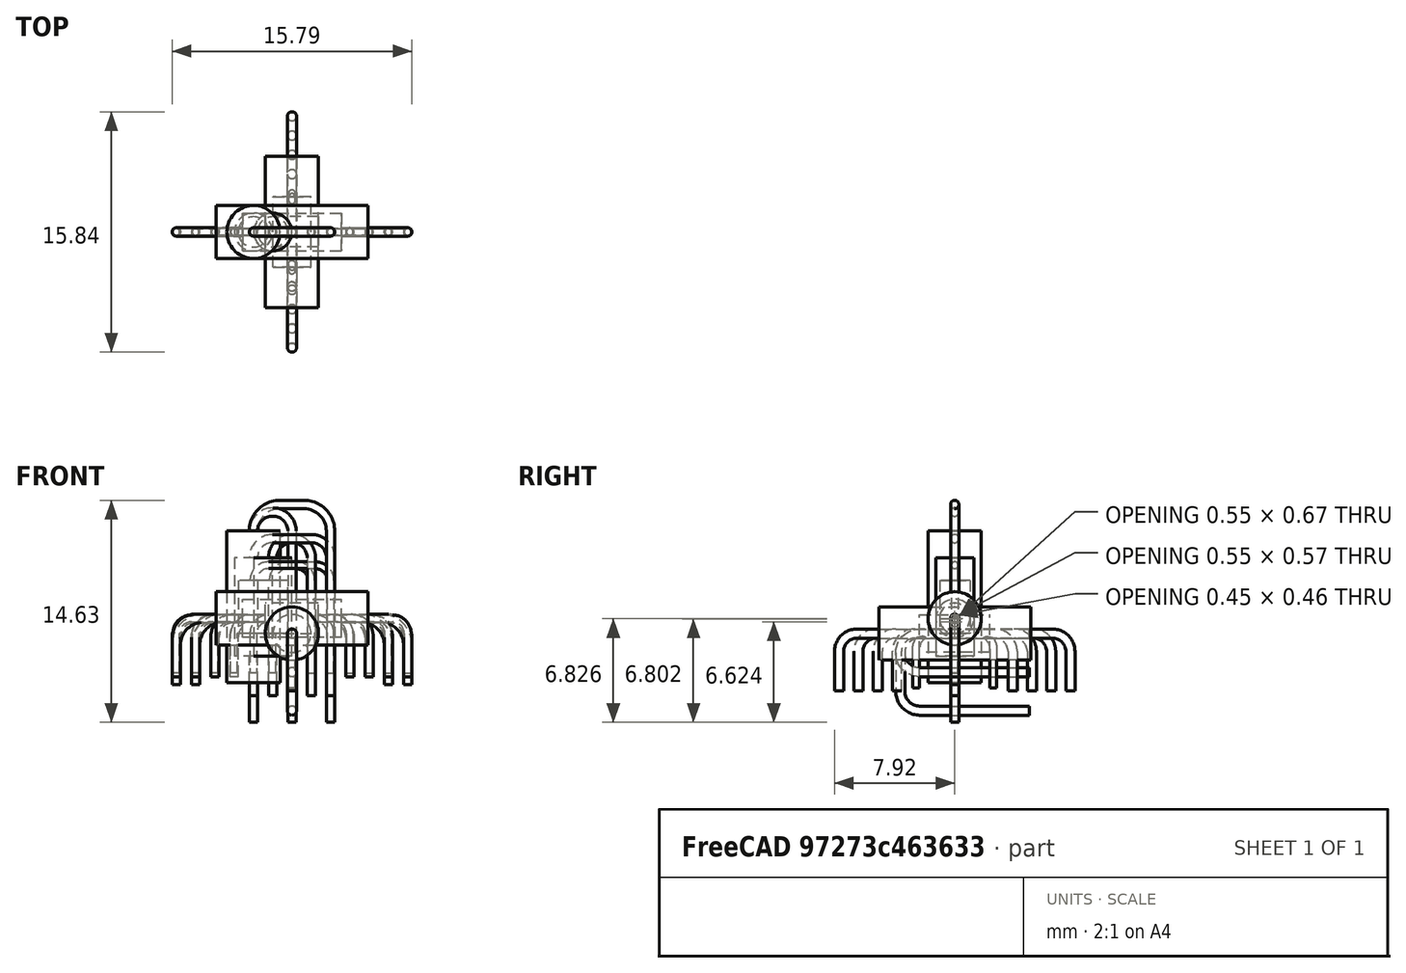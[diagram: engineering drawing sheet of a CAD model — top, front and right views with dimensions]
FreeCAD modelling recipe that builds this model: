
FCSTD DOCUMENT  (FreeCAD 0.19R17069 (Git))
Label: Generic Resistors
License: All rights reserved
LicenseURL: http://en.wikipedia.org/wiki/All_rights_reserved
objects: Sketcher::SketchObject×143, PartDesign::Body×94, PartDesign::AdditivePipe×49, PartDesign::Pad×45, Part::MultiFuse×43, App::DocumentObjectGroup×9, PartDesign::FeatureBase×1
note: 469 computed .brp shape members not serialized (recipe doc carries the construction recipe); baked Part::Feature solids carry a one-line shape summary decoded from their .brp

FEATURE [Sketcher::SketchObject] Sketch
  AttachmentOffset = pos=(0,0,0) rot=(0,0,1;-1.5708rad)
  MapMode = 5
  Placement = pos=(0,0,0) rot=(-0.57735,-0.57735,0.57735;4.18879rad)
  Support = -> [XZ_Plane]
  expr: Constraints[1] = 1.25
  sketch-geometry (1):
    g0: Circle CenterX=0 CenterY=0 CenterZ=0 NormalX=0 NormalY=0 NormalZ=1 AngleXU=0 Radius=1.25
  constraints (2):
    c: Coincident(g0,g-1)
    c: Radius(g0) = 1.25
FEATURE [PartDesign::Pad] Pad
  Length = 4.63
  Length2 = 100
  Midplane = true
  Placement = pos=(0,0,0) rot=(1,0,0;1.5708rad)
  Profile = -> Sketch
  Type = 0
  expr: Length = (4.06 + 5.2) / 2
FEATURE [PartDesign::Body] Body  label="Body_1/4W"
  Group = -> [Sketch,Pad]
  Origin = -> Origin
  Tip = -> Pad
FEATURE [Sketcher::SketchObject] Sketch002
  MapMode = 5
  Placement = pos=(0,0,0) rot=(0.57735,0.57735,0.57735;2.0944rad)
  Support = -> [YZ_Plane002]
  expr: Constraints[11] = (2.03 + 2.72) / 2 / 2
  expr: Constraints[10] = 3 * 2.54
  sketch-geometry (5):
    g0: LineSegment StartX=-2.6225 StartY=0 StartZ=0 EndX=2.6225 EndY=0 EndZ=0
    g1: LineSegment StartX=-3.81 StartY=-1.1875 StartZ=0 EndX=-3.81 EndY=-3.7875 EndZ=0
    g2: LineSegment StartX=3.81 StartY=-1.1875 StartZ=0 EndX=3.81 EndY=-3.7875 EndZ=0
    g3: ArcOfCircle CenterX=-2.6225 CenterY=-1.1875 CenterZ=0 NormalX=0 NormalY=0 NormalZ=1 AngleXU=0 Radius=1.1875 StartAngle=1.5708 EndAngle=3.14159
    g4: ArcOfCircle CenterX=2.6225 CenterY=-1.1875 CenterZ=0 NormalX=0 NormalY=0 NormalZ=1 AngleXU=0 Radius=1.1875 StartAngle=0 EndAngle=1.5708
  constraints (13):
    c: Vertical(g1)
    c: Vertical(g2)
    c: Equal(g2,g1)
    c: Tangent(g0,g3) = 1.5708
    c: Tangent(g1,g3) = -1.5708
    c: Tangent(g0,g4) = 1.5708
    c: Tangent(g2,g4) = 1.5708
    c: Symmetric(g0,g0,g-2)
    c: Equal(g4,g3)
    c: PointOnObject(g0,g-1)
    c: DistanceX(g1,g2) = 7.62
    c: DistanceY(g1,g0) = 1.1875
    c: DistanceY(g1,g1) = 2.6
FEATURE [Sketcher::SketchObject] Sketch003
  AttachmentOffset = pos=(0,0,0) rot=(0,0,1;-1.5708rad)
  MapMode = 5
  Placement = pos=(0,0,0) rot=(-0.57735,-0.57735,0.57735;4.18879rad)
  Support = -> [XZ_Plane002]
  expr: Constraints[1] = 0.3
  sketch-geometry (1):
    g0: Circle CenterX=0 CenterY=0 CenterZ=0 NormalX=0 NormalY=0 NormalZ=1 AngleXU=0 Radius=0.3
  constraints (2):
    c: Coincident(g0,g-1)
    c: Radius(g0) = 0.3
FEATURE [PartDesign::AdditivePipe] AdditivePipe
  AuxilleryCurvelinear = true
  AuxillerySpineTangent = false
  Binormal = (0,0,0)
  Mode = 0
  Placement = pos=(0,0,0) rot=(1,0,0;1.5708rad)
  Profile = -> Sketch003
  Refine = true
  Spine = -> Sketch002
  SpineTangent = false
  Transformation = 0
  Transition = 0
FEATURE [PartDesign::Body] Body002  label="Leads_P7.62"
  Group = -> [Sketch002,Sketch003,AdditivePipe]
  Origin = -> Origin002
  Tip = -> AdditivePipe
FEATURE [Sketcher::SketchObject] Sketch004
  MapMode = 5
  Placement = pos=(0,0,0) rot=(0.57735,0.57735,0.57735;2.0944rad)
  Support = -> [YZ_Plane003]
  expr: Constraints[11] = (2.03 + 2.72) / 2 / 2
  expr: Constraints[10] = 4 * 2.54
  sketch-geometry (5):
    g0: LineSegment StartX=-3.8925 StartY=-4.323e-13 StartZ=0 EndX=3.8925 EndY=-4.323e-13 EndZ=0
    g1: LineSegment StartX=-5.08 StartY=-1.1875 StartZ=0 EndX=-5.08 EndY=-3.7875 EndZ=0
    g2: LineSegment StartX=5.08 StartY=-1.1875 StartZ=0 EndX=5.08 EndY=-3.7875 EndZ=0
    g3: ArcOfCircle CenterX=-3.8925 CenterY=-1.1875 CenterZ=0 NormalX=0 NormalY=0 NormalZ=1 AngleXU=0 Radius=1.1875 StartAngle=1.5708 EndAngle=3.14159
    g4: ArcOfCircle CenterX=3.8925 CenterY=-1.1875 CenterZ=0 NormalX=0 NormalY=0 NormalZ=1 AngleXU=0 Radius=1.1875 StartAngle=-3.3777e-12 EndAngle=1.5708
  constraints (13):
    c: Vertical(g1)
    c: Vertical(g2)
    c: Equal(g2,g1)
    c: Tangent(g0,g3) = 1.5708
    c: Tangent(g1,g3) = -1.5708
    c: Tangent(g0,g4) = 1.5708
    c: Tangent(g2,g4) = 1.5708
    c: Symmetric(g0,g0,g-2)
    c: Equal(g4,g3)
    c: PointOnObject(g0,g-1)
    c: DistanceX(g1,g2) = 10.16
    c: DistanceY(g1,g0) = 1.1875
    c: DistanceY(g1,g1) = 2.6
FEATURE [Sketcher::SketchObject] Sketch005
  AttachmentOffset = pos=(0,0,0) rot=(0,0,1;-1.5708rad)
  MapMode = 5
  Placement = pos=(0,0,0) rot=(-0.57735,-0.57735,0.57735;4.18879rad)
  Support = -> [XZ_Plane003]
  expr: Constraints[1] = 0.3
  sketch-geometry (1):
    g0: Circle CenterX=0 CenterY=0 CenterZ=0 NormalX=0 NormalY=0 NormalZ=1 AngleXU=0 Radius=0.3
  constraints (2):
    c: Coincident(g0,g-1)
    c: Radius(g0) = 0.3
FEATURE [PartDesign::AdditivePipe] AdditivePipe001
  AuxilleryCurvelinear = true
  AuxillerySpineTangent = false
  Binormal = (0,0,0)
  Mode = 0
  Placement = pos=(0,0,0) rot=(1,0,0;1.5708rad)
  Profile = -> Sketch005
  Refine = true
  Spine = -> Sketch004
  SpineTangent = false
  Transformation = 0
  Transition = 0
FEATURE [PartDesign::Body] Body003  label="Leads_P10.16"
  Group = -> [Sketch004,Sketch005,AdditivePipe001]
  Origin = -> Origin003
  Tip = -> AdditivePipe001
FEATURE [Sketcher::SketchObject] Sketch006
  MapMode = 5
  Placement = pos=(0,0,0) rot=(0.57735,0.57735,0.57735;2.0944rad)
  Support = -> [YZ_Plane004]
  expr: Constraints[15] = (4.06 + 5.2) / 2 / 2
  expr: Constraints[7] = (4.06 + 5.2) / 2 / 2
  expr: Constraints[3] = 2.54 / 2
  sketch-geometry (7):
    g0: LineSegment StartX=4.915 StartY=0 StartZ=0 EndX=-2.315 EndY=0 EndZ=0
    g1: ArcOfCircle CenterX=-2.315 CenterY=-1.27 CenterZ=0 NormalX=0 NormalY=0 NormalZ=1 AngleXU=0 Radius=1.27 StartAngle=1.5708 EndAngle=4.71239
    g2: LineSegment StartX=-2.315 StartY=-2.54 StartZ=0 EndX=4.915 EndY=-2.54 EndZ=0
    g3: GeomPoint X=2.315 Y=0 Z=0
    g4: GeomPoint X=2.315 Y=-2.54 Z=0
    g5: GeomPoint X=-3.585 Y=-1.27 Z=0
    g6: GeomPoint X=-2.315 Y=0 Z=0
  constraints (17):
    c: PointOnObject(g0,g-1)
    c: PointOnObject(g0,g-1)
    c: Horizontal(g2)
    c: Radius(g1) = 1.27
    c: Tangent(g1,g0) = -1.5708
    c: Tangent(g2,g1) = -1.5708
    c: PointOnObject(g3,g0)
    c: DistanceX(g-1,g3) = 2.315
    c: DistanceX(g3,g0) = 2.6
    c: PointOnObject(g4,g2)
    c: DistanceX(g4,g2) = 2.6
    c: Vertical(g0,g2)
    c: PointOnObject(g5,g1)
    c: Horizontal(g1,g5)
    c: PointOnObject(g6,g0)
    c: DistanceX(g6,g-1) = 2.315
    c: DistanceX(g0,g6) = 0
FEATURE [Sketcher::SketchObject] Sketch007
  AttachmentOffset = pos=(0,0,0) rot=(0,0,1;-1.5708rad)
  MapMode = 5
  Placement = pos=(0,0,0) rot=(-0.57735,-0.57735,0.57735;4.18879rad)
  Support = -> [XZ_Plane004]
  expr: Constraints[1] = 0.3
  sketch-geometry (1):
    g0: Circle CenterX=0 CenterY=0 CenterZ=0 NormalX=0 NormalY=0 NormalZ=1 AngleXU=0 Radius=0.3
  constraints (2):
    c: Coincident(g0,g-1)
    c: Radius(g0) = 0.3
FEATURE [PartDesign::AdditivePipe] AdditivePipe002
  AuxilleryCurvelinear = true
  AuxillerySpineTangent = false
  Binormal = (0,0,0)
  Mode = 0
  Placement = pos=(0,0,0) rot=(1,0,0;1.5708rad)
  Profile = -> Sketch007
  Refine = true
  Spine = -> Sketch006
  SpineTangent = false
  Transformation = 0
  Transition = 0
FEATURE [PartDesign::Body] Body004  label="Leads_Vertical_P2.54"
  Group = -> [Sketch006,Sketch007,AdditivePipe002]
  Origin = -> Origin004
  Tip = -> AdditivePipe002
FEATURE [Sketcher::SketchObject] Sketch008
  MapMode = 5
  Placement = pos=(0,0,0) rot=(0.57735,0.57735,0.57735;2.0944rad)
  Support = -> [YZ_Plane005]
  expr: Constraints[18] = 1.27
  expr: Constraints[9] = (4.06 + 5.2) / 2 / 2
  expr: Constraints[3] = (4.06 + 5.2) / 2 / 2
  sketch-geometry (8):
    g0: LineSegment StartX=4.915 StartY=0 StartZ=0 EndX=-2.315 EndY=0 EndZ=0
    g1: LineSegment StartX=-2.315 StartY=-5.08 StartZ=0 EndX=4.915 EndY=-5.08 EndZ=0
    g2: GeomPoint X=2.315 Y=0 Z=0
    g3: GeomPoint X=2.315 Y=-5.08 Z=0
    g4: GeomPoint X=-2.315 Y=0 Z=0
    g5: LineSegment StartX=-3.585 StartY=-1.27 StartZ=0 EndX=-3.585 EndY=-3.81 EndZ=0
    g6: ArcOfCircle CenterX=-2.315 CenterY=-1.27 CenterZ=0 NormalX=0 NormalY=0 NormalZ=1 AngleXU=0 Radius=1.27 StartAngle=1.5708 EndAngle=3.14159
    g7: ArcOfCircle CenterX=-2.315 CenterY=-3.81 CenterZ=0 NormalX=0 NormalY=0 NormalZ=1 AngleXU=0 Radius=1.27 StartAngle=3.14159 EndAngle=4.71239
  constraints (20):
    c: PointOnObject(g0,g-1)
    c: Horizontal(g1)
    c: PointOnObject(g2,g0)
    c: DistanceX(g-1,g2) = 2.315
    c: DistanceX(g2,g0) = 2.6
    c: PointOnObject(g3,g1)
    c: DistanceX(g3,g1) = 2.6
    c: Vertical(g0,g1)
    c: PointOnObject(g4,g0)
    c: DistanceX(g4,g-1) = 2.315
    c: Vertical(g5)
    c: Tangent(g0,g6) = -1.5708
    c: Tangent(g5,g6) = -1.5708
    c: Tangent(g1,g7) = -1.5708
    c: Tangent(g5,g7) = -1.5708
    c: DistanceY(g1,g0) = 5.08
    c: PointOnObject(g0,g-1)
    c: Equal(g7,g6)
    c: Radius(g6) = 1.27
    c: DistanceX(g0,g4) = 0
FEATURE [Sketcher::SketchObject] Sketch009
  AttachmentOffset = pos=(0,0,0) rot=(0,0,1;-1.5708rad)
  MapMode = 5
  Placement = pos=(0,0,0) rot=(-0.57735,-0.57735,0.57735;4.18879rad)
  Support = -> [XZ_Plane005]
  expr: Constraints[1] = 0.3
  sketch-geometry (1):
    g0: Circle CenterX=0 CenterY=0 CenterZ=0 NormalX=0 NormalY=0 NormalZ=1 AngleXU=0 Radius=0.3
  constraints (2):
    c: Coincident(g0,g-1)
    c: Radius(g0) = 0.3
FEATURE [PartDesign::AdditivePipe] AdditivePipe003
  AuxilleryCurvelinear = true
  AuxillerySpineTangent = false
  Binormal = (0,0,0)
  Mode = 0
  Placement = pos=(0,0,0) rot=(1,0,0;1.5708rad)
  Profile = -> Sketch009
  Refine = true
  Spine = -> Sketch008
  SpineTangent = false
  Transformation = 0
  Transition = 0
FEATURE [PartDesign::Body] Body005  label="Leads_Vertical_P5.08"
  Group = -> [Sketch008,Sketch009,AdditivePipe003]
  Origin = -> Origin005
  Tip = -> AdditivePipe003
FEATURE [Sketcher::SketchObject] Sketch010
  AttachmentOffset = pos=(0,0,0) rot=(0,0,1;-1.5708rad)
  MapMode = 5
  Placement = pos=(0,0,0) rot=(-0.57735,-0.57735,0.57735;4.18879rad)
  Support = -> [XZ_Plane006]
  expr: Constraints[1] = 2 / 2
  sketch-geometry (1):
    g0: Circle CenterX=0 CenterY=0 CenterZ=0 NormalX=0 NormalY=0 NormalZ=1 AngleXU=0 Radius=1
  constraints (2):
    c: Coincident(g0,g-1)
    c: Radius(g0) = 1
FEATURE [PartDesign::Pad] Pad001
  Length = 3.5
  Length2 = 100
  Midplane = true
  Placement = pos=(0,0,0) rot=(1,0,0;1.5708rad)
  Profile = -> Sketch010
  Type = 0
  expr: Length = 3.5
FEATURE [PartDesign::Body] Body006  label="1/8W_Body"
  Group = -> [Sketch010,Pad001]
  Origin = -> Origin006
  Tip = -> Pad001
FEATURE [Sketcher::SketchObject] Sketch011
  AttachmentOffset = pos=(0,0,0) rot=(0,0,1;-1.5708rad)
  MapMode = 5
  Placement = pos=(0,0,0) rot=(-0.57735,-0.57735,0.57735;4.18879rad)
  Support = -> [XZ_Plane007]
  expr: Constraints[1] = 1.75
  sketch-geometry (1):
    g0: Circle CenterX=0 CenterY=0 CenterZ=0 NormalX=0 NormalY=0 NormalZ=1 AngleXU=0 Radius=1.75
  constraints (2):
    c: Coincident(g0,g-1)
    c: Radius(g0) = 1.75
FEATURE [PartDesign::Pad] Pad002
  Length = 10
  Length2 = 100
  Midplane = true
  Placement = pos=(0,0,0) rot=(1,0,0;1.5708rad)
  Profile = -> Sketch011
  Type = 0
  expr: Length = 10
FEATURE [PartDesign::Body] Body007  label="Body_1/2W"
  Group = -> [Sketch011,Pad002]
  Origin = -> Origin007
  Tip = -> Pad002
FEATURE [Sketcher::SketchObject] Sketch012
  MapMode = 5
  Placement = pos=(0,0,0) rot=(0.57735,0.57735,0.57735;2.0944rad)
  Support = -> [YZ_Plane008]
  expr: Constraints[11] = (2.03 + 2.72) / 2 / 2
  expr: Constraints[10] = 12.7
  sketch-geometry (5):
    g0: LineSegment StartX=-5.1625 StartY=-4.323e-13 StartZ=0 EndX=5.1625 EndY=-4.323e-13 EndZ=0
    g1: LineSegment StartX=-6.35 StartY=-1.1875 StartZ=0 EndX=-6.35 EndY=-3.7875 EndZ=0
    g2: LineSegment StartX=6.35 StartY=-1.1875 StartZ=0 EndX=6.35 EndY=-3.7875 EndZ=0
    g3: ArcOfCircle CenterX=-5.1625 CenterY=-1.1875 CenterZ=0 NormalX=0 NormalY=0 NormalZ=1 AngleXU=0 Radius=1.1875 StartAngle=1.5708 EndAngle=3.14159
    g4: ArcOfCircle CenterX=5.1625 CenterY=-1.1875 CenterZ=0 NormalX=0 NormalY=0 NormalZ=1 AngleXU=0 Radius=1.1875 StartAngle=-3.3777e-12 EndAngle=1.5708
  constraints (13):
    c: Vertical(g1)
    c: Vertical(g2)
    c: Equal(g2,g1)
    c: Tangent(g0,g3) = 1.5708
    c: Tangent(g1,g3) = -1.5708
    c: Tangent(g0,g4) = 1.5708
    c: Tangent(g2,g4) = 1.5708
    c: Symmetric(g0,g0,g-2)
    c: Equal(g4,g3)
    c: PointOnObject(g0,g-1)
    c: DistanceX(g1,g2) = 12.7
    c: DistanceY(g1,g0) = 1.1875
    c: DistanceY(g1,g1) = 2.6
FEATURE [Sketcher::SketchObject] Sketch013
  AttachmentOffset = pos=(0,0,0) rot=(0,0,1;-1.5708rad)
  MapMode = 5
  Placement = pos=(0,0,0) rot=(-0.57735,-0.57735,0.57735;4.18879rad)
  Support = -> [XZ_Plane008]
  expr: Constraints[1] = 0.3
  sketch-geometry (1):
    g0: Circle CenterX=0 CenterY=0 CenterZ=0 NormalX=0 NormalY=0 NormalZ=1 AngleXU=0 Radius=0.3
  constraints (2):
    c: Coincident(g0,g-1)
    c: Radius(g0) = 0.3
FEATURE [PartDesign::AdditivePipe] AdditivePipe004
  AuxilleryCurvelinear = true
  AuxillerySpineTangent = false
  Binormal = (0,0,0)
  Mode = 0
  Placement = pos=(0,0,0) rot=(1,0,0;1.5708rad)
  Profile = -> Sketch013
  Refine = true
  Spine = -> Sketch012
  SpineTangent = false
  Transformation = 0
  Transition = 0
FEATURE [PartDesign::Body] Body008  label="Leads_P12.7"
  Group = -> [Sketch012,Sketch013,AdditivePipe004]
  Origin = -> Origin008
  Tip = -> AdditivePipe004
FEATURE [Sketcher::SketchObject] Sketch014
  AttachmentOffset = pos=(0,0,0) rot=(0,0,1;-1.5708rad)
  MapMode = 5
  Placement = pos=(0,0,0) rot=(-0.57735,-0.57735,0.57735;4.18879rad)
  Support = -> [XZ_Plane009]
  expr: Constraints[1] = 0.3
  sketch-geometry (1):
    g0: Circle CenterX=0 CenterY=0 CenterZ=0 NormalX=0 NormalY=0 NormalZ=1 AngleXU=0 Radius=0.3
  constraints (2):
    c: Coincident(g0,g-1)
    c: Radius(g0) = 0.3
FEATURE [Sketcher::SketchObject] Sketch015
  MapMode = 5
  Placement = pos=(0,0,0) rot=(0.57735,0.57735,0.57735;2.0944rad)
  Support = -> [YZ_Plane009]
  expr: Constraints[11] = (2.03 + 2.72) / 2 / 2
  expr: Constraints[10] = 15.24
  sketch-geometry (5):
    g0: LineSegment StartX=-6.4325 StartY=-4.323e-13 StartZ=0 EndX=6.4325 EndY=-4.323e-13 EndZ=0
    g1: LineSegment StartX=-7.62 StartY=-1.1875 StartZ=0 EndX=-7.62 EndY=-3.7875 EndZ=0
    g2: LineSegment StartX=7.62 StartY=-1.1875 StartZ=0 EndX=7.62 EndY=-3.7875 EndZ=0
    g3: ArcOfCircle CenterX=-6.4325 CenterY=-1.1875 CenterZ=0 NormalX=0 NormalY=0 NormalZ=1 AngleXU=0 Radius=1.1875 StartAngle=1.5708 EndAngle=3.14159
    g4: ArcOfCircle CenterX=6.4325 CenterY=-1.1875 CenterZ=0 NormalX=0 NormalY=0 NormalZ=1 AngleXU=0 Radius=1.1875 StartAngle=-3.3777e-12 EndAngle=1.5708
  constraints (13):
    c: Vertical(g1)
    c: Vertical(g2)
    c: Equal(g2,g1)
    c: Tangent(g0,g3) = 1.5708
    c: Tangent(g1,g3) = -1.5708
    c: Tangent(g0,g4) = 1.5708
    c: Tangent(g2,g4) = 1.5708
    c: Symmetric(g0,g0,g-2)
    c: Equal(g4,g3)
    c: PointOnObject(g0,g-1)
    c: DistanceX(g1,g2) = 15.24
    c: DistanceY(g1,g0) = 1.1875
    c: DistanceY(g1,g1) = 2.6
FEATURE [Sketcher::SketchObject] Sketch018
  MapMode = 5
  Placement = pos=(0,0,0) rot=(0.57735,0.57735,0.57735;2.0944rad)
  Support = -> [YZ_Plane012]
  expr: Constraints[11] = 2 / 2
  expr: Constraints[10] = 4 * 2.54
  sketch-geometry (5):
    g0: LineSegment StartX=-4.08 StartY=0 StartZ=0 EndX=4.08 EndY=0 EndZ=0
    g1: LineSegment StartX=-5.08 StartY=-1 StartZ=0 EndX=-5.08 EndY=-3.6 EndZ=0
    g2: LineSegment StartX=5.08 StartY=-1 StartZ=0 EndX=5.08 EndY=-3.6 EndZ=0
    g3: ArcOfCircle CenterX=-4.08 CenterY=-1 CenterZ=0 NormalX=0 NormalY=0 NormalZ=1 AngleXU=0 Radius=1 StartAngle=1.5708 EndAngle=3.14159
    g4: ArcOfCircle CenterX=4.08 CenterY=-1 CenterZ=0 NormalX=0 NormalY=0 NormalZ=1 AngleXU=0 Radius=1 StartAngle=0 EndAngle=1.5708
  constraints (13):
    c: Vertical(g1)
    c: Vertical(g2)
    c: Equal(g2,g1)
    c: Tangent(g0,g3) = 1.5708
    c: Tangent(g1,g3) = -1.5708
    c: Tangent(g0,g4) = 1.5708
    c: Tangent(g2,g4) = 1.5708
    c: Symmetric(g0,g0,g-2)
    c: Equal(g4,g3)
    c: PointOnObject(g0,g-1)
    c: DistanceX(g1,g2) = 10.16
    c: DistanceY(g1,g0) = 1
    c: DistanceY(g1,g1) = 2.6
FEATURE [Sketcher::SketchObject] Sketch019
  AttachmentOffset = pos=(0,0,0) rot=(0,0,1;-1.5708rad)
  MapMode = 5
  Placement = pos=(0,0,0) rot=(-0.57735,-0.57735,0.57735;4.18879rad)
  Support = -> [XZ_Plane010]
  expr: Constraints[1] = 0.45 / 2
  sketch-geometry (1):
    g0: Circle CenterX=0 CenterY=0 CenterZ=0 NormalX=0 NormalY=0 NormalZ=1 AngleXU=0 Radius=0.225
  constraints (2):
    c: Coincident(g0,g-1)
    c: Radius(g0) = 0.225
FEATURE [PartDesign::AdditivePipe] AdditivePipe011
  AuxilleryCurvelinear = true
  AuxillerySpineTangent = false
  Binormal = (0,0,0)
  Mode = 0
  Placement = pos=(0,0,0) rot=(1,0,0;1.5708rad)
  Profile = -> Sketch019
  Refine = true
  Spine = -> Sketch018
  SpineTangent = false
  Transformation = 0
  Transition = 0
FEATURE [PartDesign::Body] Body012  label="1/8W_10.16_H"
  Group = -> [Sketch018,Sketch019,AdditivePipe011]
  Origin = -> Origin011
  Tip = -> AdditivePipe011
FEATURE [Sketcher::SketchObject] Sketch020
  MapMode = 5
  Placement = pos=(0,0,0) rot=(0.57735,0.57735,0.57735;2.0944rad)
  Support = -> [YZ_Plane011]
  expr: Constraints[24] = 2.54
  expr: Constraints[15] = 2 / 2
  expr: Constraints[10] = 3.5 / 2
  expr: Constraints[4] = 3.5 / 2
  sketch-geometry (9):
    g0: LineSegment StartX=4.35 StartY=0 StartZ=0 EndX=-1.75 EndY=1e-16 EndZ=0
    g1: LineSegment StartX=-1.75 StartY=-2.54 StartZ=0 EndX=4.35 EndY=-2.54 EndZ=0
    g2: GeomPoint X=1.75 Y=0 Z=0
    g3: GeomPoint X=1.75 Y=-2.54 Z=0
    g4: GeomPoint X=-2.75 Y=-1 Z=0
    g5: GeomPoint X=-1.75 Y=0 Z=0
    g6: ArcOfCircle CenterX=-1.75 CenterY=-1 CenterZ=0 NormalX=0 NormalY=0 NormalZ=1 AngleXU=0 Radius=1 StartAngle=1.5708 EndAngle=3.14159
    g7: LineSegment StartX=-2.75 StartY=-1 StartZ=0 EndX=-2.75 EndY=-1.54 EndZ=0
    g8: ArcOfCircle CenterX=-1.75 CenterY=-1.54 CenterZ=0 NormalX=0 NormalY=0 NormalZ=1 AngleXU=0 Radius=1 StartAngle=3.14159 EndAngle=4.71239
  constraints (25):
    c: PointOnObject(g0,g-1)
    c: PointOnObject(g0,g-1)
    c: Horizontal(g1)
    c: PointOnObject(g2,g0)
    c: DistanceX(g-1,g2) = 1.75
    c: DistanceX(g2,g0) = 2.6
    c: PointOnObject(g3,g1)
    c: DistanceX(g3,g1) = 2.6
    c: Vertical(g0,g1)
    c: PointOnObject(g5,g0)
    c: DistanceX(g5,g-1) = 1.75
    c: DistanceX(g0,g5) = 0
    c: Coincident(g6,g0)
    c: Coincident(g6,g4)
    c: Horizontal(g6,g4)
    c: Radius(g6) = 1
    c: Vertical(g6,g0)
    c: Coincident(g7,g4)
    c: Vertical(g7)
    c: Coincident(g8,g7)
    c: Coincident(g8,g1)
    c: Equal(g8,g6)
    c: Horizontal(g8,g7)
    c: Vertical(g8,g1)
    c: DistanceY(g1,g0) = 2.54
FEATURE [Sketcher::SketchObject] Sketch021
  AttachmentOffset = pos=(0,0,0) rot=(0,0,1;-1.5708rad)
  MapMode = 5
  Placement = pos=(0,0,0) rot=(-0.57735,-0.57735,0.57735;4.18879rad)
  Support = -> [XZ_Plane011]
  expr: Constraints[1] = 0.45 / 2
  sketch-geometry (1):
    g0: Circle CenterX=0 CenterY=0 CenterZ=0 NormalX=0 NormalY=0 NormalZ=1 AngleXU=0 Radius=0.225
  constraints (2):
    c: Coincident(g0,g-1)
    c: Radius(g0) = 0.225
FEATURE [PartDesign::AdditivePipe] AdditivePipe008
  AuxilleryCurvelinear = true
  AuxillerySpineTangent = false
  Binormal = (0,0,0)
  Mode = 0
  Placement = pos=(0,0,0) rot=(1,0,0;1.5708rad)
  Profile = -> Sketch021
  Refine = true
  Spine = -> Sketch020
  SpineTangent = false
  Transformation = 0
  Transition = 0
FEATURE [PartDesign::Body] Body010  label="1/8W_2.54_V"
  Group = -> [Sketch020,Sketch021,AdditivePipe008]
  Origin = -> Origin012
  Tip = -> AdditivePipe008
FEATURE [Sketcher::SketchObject] Sketch022
  MapMode = 5
  Placement = pos=(0,0,0) rot=(0.57735,0.57735,0.57735;2.0944rad)
  Support = -> [YZ_Plane013]
  expr: Constraints[18] = 2 / 2
  expr: Constraints[9] = 3.5 / 2
  expr: Constraints[3] = 3.5 / 2
  sketch-geometry (8):
    g0: LineSegment StartX=4.35 StartY=0 StartZ=0 EndX=-1.75 EndY=0 EndZ=0
    g1: LineSegment StartX=-1.75 StartY=-5.08 StartZ=0 EndX=4.35 EndY=-5.08 EndZ=0
    g2: GeomPoint X=1.75 Y=0 Z=0
    g3: GeomPoint X=1.75 Y=-5.08 Z=0
    g4: GeomPoint X=-1.75 Y=0 Z=0
    g5: LineSegment StartX=-2.75 StartY=-1 StartZ=0 EndX=-2.75 EndY=-4.08 EndZ=0
    g6: ArcOfCircle CenterX=-1.75 CenterY=-1 CenterZ=0 NormalX=0 NormalY=0 NormalZ=1 AngleXU=0 Radius=1 StartAngle=1.5708 EndAngle=3.14159
    g7: ArcOfCircle CenterX=-1.75 CenterY=-4.08 CenterZ=0 NormalX=0 NormalY=0 NormalZ=1 AngleXU=0 Radius=1 StartAngle=3.14159 EndAngle=4.71239
  constraints (20):
    c: PointOnObject(g0,g-1)
    c: Horizontal(g1)
    c: PointOnObject(g2,g0)
    c: DistanceX(g-1,g2) = 1.75
    c: DistanceX(g2,g0) = 2.6
    c: PointOnObject(g3,g1)
    c: DistanceX(g3,g1) = 2.6
    c: Vertical(g0,g1)
    c: PointOnObject(g4,g0)
    c: DistanceX(g4,g-1) = 1.75
    c: Vertical(g5)
    c: Tangent(g0,g6) = -1.5708
    c: Tangent(g5,g6) = -1.5708
    c: Tangent(g1,g7) = -1.5708
    c: Tangent(g5,g7) = -1.5708
    c: DistanceY(g1,g0) = 5.08
    c: PointOnObject(g0,g-1)
    c: Equal(g7,g6)
    c: Radius(g6) = 1
    c: DistanceX(g0,g4) = 0
FEATURE [Sketcher::SketchObject] Sketch023
  AttachmentOffset = pos=(0,0,0) rot=(0,0,1;-1.5708rad)
  MapMode = 5
  Placement = pos=(0,0,0) rot=(-0.57735,-0.57735,0.57735;4.18879rad)
  Support = -> [XZ_Plane013]
  expr: Constraints[1] = 0.45 / 2
  sketch-geometry (1):
    g0: Circle CenterX=0 CenterY=0 CenterZ=0 NormalX=0 NormalY=0 NormalZ=1 AngleXU=0 Radius=0.225
  constraints (2):
    c: Coincident(g0,g-1)
    c: Radius(g0) = 0.225
FEATURE [PartDesign::AdditivePipe] AdditivePipe007
  AuxilleryCurvelinear = true
  AuxillerySpineTangent = false
  Binormal = (0,0,0)
  Mode = 0
  Placement = pos=(0,0,0) rot=(1,0,0;1.5708rad)
  Profile = -> Sketch023
  Refine = true
  Spine = -> Sketch022
  SpineTangent = false
  Transformation = 0
  Transition = 0
FEATURE [PartDesign::Body] Body013  label="1/8W_5.08_V"
  Group = -> [Sketch022,Sketch023,AdditivePipe007]
  Origin = -> Origin013
  Tip = -> AdditivePipe007
FEATURE [Sketcher::SketchObject] Sketch024
  MapMode = 5
  Placement = pos=(0,0,0) rot=(0.57735,0.57735,0.57735;2.0944rad)
  Support = -> [YZ_Plane014]
  expr: Constraints[11] = 2 / 2
  expr: Constraints[10] = 12.7
  sketch-geometry (5):
    g0: LineSegment StartX=-5.35 StartY=0 StartZ=0 EndX=5.35 EndY=0 EndZ=0
    g1: LineSegment StartX=-6.35 StartY=-1 StartZ=0 EndX=-6.35 EndY=-3.6 EndZ=0
    g2: LineSegment StartX=6.35 StartY=-1 StartZ=0 EndX=6.35 EndY=-3.6 EndZ=0
    g3: ArcOfCircle CenterX=-5.35 CenterY=-1 CenterZ=0 NormalX=0 NormalY=0 NormalZ=1 AngleXU=0 Radius=1 StartAngle=1.5708 EndAngle=3.14159
    g4: ArcOfCircle CenterX=5.35 CenterY=-1 CenterZ=0 NormalX=0 NormalY=0 NormalZ=1 AngleXU=0 Radius=1 StartAngle=0 EndAngle=1.5708
  constraints (13):
    c: Vertical(g1)
    c: Vertical(g2)
    c: Equal(g2,g1)
    c: Tangent(g0,g3) = 1.5708
    c: Tangent(g1,g3) = -1.5708
    c: Tangent(g0,g4) = 1.5708
    c: Tangent(g2,g4) = 1.5708
    c: Symmetric(g0,g0,g-2)
    c: Equal(g4,g3)
    c: PointOnObject(g0,g-1)
    c: DistanceX(g1,g2) = 12.7
    c: DistanceY(g1,g0) = 1
    c: DistanceY(g1,g1) = 2.6
FEATURE [Sketcher::SketchObject] Sketch025
  AttachmentOffset = pos=(0,0,0) rot=(0,0,1;-1.5708rad)
  MapMode = 5
  Placement = pos=(0,0,0) rot=(-0.57735,-0.57735,0.57735;4.18879rad)
  Support = -> [XZ_Plane014]
  expr: Constraints[1] = 0.45 / 2
  sketch-geometry (1):
    g0: Circle CenterX=0 CenterY=0 CenterZ=0 NormalX=0 NormalY=0 NormalZ=1 AngleXU=0 Radius=0.225
  constraints (2):
    c: Coincident(g0,g-1)
    c: Radius(g0) = 0.225
FEATURE [PartDesign::AdditivePipe] AdditivePipe010
  AuxilleryCurvelinear = true
  AuxillerySpineTangent = false
  Binormal = (0,0,0)
  Mode = 0
  Placement = pos=(0,0,0) rot=(1,0,0;1.5708rad)
  Profile = -> Sketch025
  Refine = true
  Spine = -> Sketch024
  SpineTangent = false
  Transformation = 0
  Transition = 0
FEATURE [PartDesign::Body] Body014  label="1/8W_12.70_H"
  Group = -> [Sketch024,Sketch025,AdditivePipe010]
  Origin = -> Origin014
  Tip = -> AdditivePipe010
FEATURE [Sketcher::SketchObject] Sketch026
  AttachmentOffset = pos=(0,0,0) rot=(0,0,1;-1.5708rad)
  MapMode = 5
  Placement = pos=(0,0,0) rot=(-0.57735,-0.57735,0.57735;4.18879rad)
  Support = -> [XZ_Plane015]
  expr: Constraints[1] = 0.45 / 2
  sketch-geometry (1):
    g0: Circle CenterX=0 CenterY=0 CenterZ=0 NormalX=0 NormalY=0 NormalZ=1 AngleXU=0 Radius=0.225
  constraints (2):
    c: Coincident(g0,g-1)
    c: Radius(g0) = 0.225
FEATURE [Sketcher::SketchObject] Sketch027
  MapMode = 5
  Placement = pos=(0,0,0) rot=(0.57735,0.57735,0.57735;2.0944rad)
  Support = -> [YZ_Plane015]
  expr: Constraints[11] = 2 / 2
  expr: Constraints[10] = 15.24
  sketch-geometry (5):
    g0: LineSegment StartX=-6.62 StartY=0 StartZ=0 EndX=6.62 EndY=0 EndZ=0
    g1: LineSegment StartX=-7.62 StartY=-1 StartZ=0 EndX=-7.62 EndY=-3.6 EndZ=0
    g2: LineSegment StartX=7.62 StartY=-1 StartZ=0 EndX=7.62 EndY=-3.6 EndZ=0
    g3: ArcOfCircle CenterX=-6.62 CenterY=-1 CenterZ=0 NormalX=0 NormalY=0 NormalZ=1 AngleXU=0 Radius=1 StartAngle=1.5708 EndAngle=3.14159
    g4: ArcOfCircle CenterX=6.62 CenterY=-1 CenterZ=0 NormalX=0 NormalY=0 NormalZ=1 AngleXU=0 Radius=1 StartAngle=0 EndAngle=1.5708
  constraints (13):
    c: Vertical(g1)
    c: Vertical(g2)
    c: Equal(g2,g1)
    c: Tangent(g0,g3) = 1.5708
    c: Tangent(g1,g3) = -1.5708
    c: Tangent(g0,g4) = 1.5708
    c: Tangent(g2,g4) = 1.5708
    c: Symmetric(g0,g0,g-2)
    c: Equal(g4,g3)
    c: PointOnObject(g0,g-1)
    c: DistanceX(g1,g2) = 15.24
    c: DistanceY(g1,g0) = 1
    c: DistanceY(g1,g1) = 2.6
FEATURE [PartDesign::AdditivePipe] AdditivePipe009
  AuxilleryCurvelinear = true
  AuxillerySpineTangent = false
  Binormal = (0,0,0)
  Mode = 0
  Placement = pos=(0,0,0) rot=(1,0,0;1.5708rad)
  Profile = -> Sketch026
  Refine = true
  Spine = -> Sketch027
  SpineTangent = false
  Transformation = 0
  Transition = 0
FEATURE [PartDesign::Body] Body015  label="1/8W_15.24_H"
  Group = -> [Sketch027,Sketch026,AdditivePipe009]
  Origin = -> Origin015
  Tip = -> AdditivePipe009
FEATURE [Sketcher::SketchObject] Sketch028
  MapMode = 5
  Placement = pos=(0,0,0) rot=(0.57735,0.57735,0.57735;2.0944rad)
  Support = -> [YZ_Plane016]
  expr: Constraints[11] = 2 / 2
  expr: Constraints[10] = 3 * 2.54
  sketch-geometry (5):
    g0: LineSegment StartX=-2.81 StartY=0 StartZ=0 EndX=2.81 EndY=0 EndZ=0
    g1: LineSegment StartX=-3.81 StartY=-1 StartZ=0 EndX=-3.81 EndY=-3.6 EndZ=0
    g2: LineSegment StartX=3.81 StartY=-1 StartZ=0 EndX=3.81 EndY=-3.6 EndZ=0
    g3: ArcOfCircle CenterX=-2.81 CenterY=-1 CenterZ=0 NormalX=0 NormalY=0 NormalZ=1 AngleXU=0 Radius=1 StartAngle=1.5708 EndAngle=3.14159
    g4: ArcOfCircle CenterX=2.81 CenterY=-1 CenterZ=0 NormalX=0 NormalY=0 NormalZ=1 AngleXU=0 Radius=1 StartAngle=0 EndAngle=1.5708
  constraints (13):
    c: Vertical(g1)
    c: Vertical(g2)
    c: Equal(g2,g1)
    c: Tangent(g0,g3) = 1.5708
    c: Tangent(g1,g3) = -1.5708
    c: Tangent(g0,g4) = 1.5708
    c: Tangent(g2,g4) = 1.5708
    c: Symmetric(g0,g0,g-2)
    c: Equal(g4,g3)
    c: PointOnObject(g0,g-1)
    c: DistanceX(g1,g2) = 7.62
    c: DistanceY(g1,g0) = 1
    c: DistanceY(g1,g1) = 2.6
FEATURE [Sketcher::SketchObject] Sketch029
  AttachmentOffset = pos=(0,0,0) rot=(0,0,1;-1.5708rad)
  MapMode = 5
  Placement = pos=(0,0,0) rot=(-0.57735,-0.57735,0.57735;4.18879rad)
  Support = -> [XZ_Plane016]
  expr: Constraints[1] = 0.45 / 2
  sketch-geometry (1):
    g0: Circle CenterX=0 CenterY=0 CenterZ=0 NormalX=0 NormalY=0 NormalZ=1 AngleXU=0 Radius=0.225
  constraints (2):
    c: Coincident(g0,g-1)
    c: Radius(g0) = 0.225
FEATURE [PartDesign::AdditivePipe] AdditivePipe012
  AuxilleryCurvelinear = true
  AuxillerySpineTangent = false
  Binormal = (0,0,0)
  Mode = 0
  Placement = pos=(0,0,0) rot=(1,0,0;1.5708rad)
  Profile = -> Sketch029
  Refine = true
  Spine = -> Sketch028
  SpineTangent = false
  Transformation = 0
  Transition = 0
FEATURE [PartDesign::Body] Body016  label="1/8W_7.62_H"
  Group = -> [Sketch028,Sketch029,AdditivePipe012]
  Origin = -> Origin016
  Tip = -> AdditivePipe012
FEATURE [Sketcher::SketchObject] Sketch030
  AttachmentOffset = pos=(0,0,0) rot=(0,0,1;-1.5708rad)
  MapMode = 5
  Placement = pos=(0,0,0) rot=(-0.57735,-0.57735,0.57735;4.18879rad)
  Support = -> [XZ_Plane017]
  expr: Constraints[1] = 0.45 / 2
  sketch-geometry (1):
    g0: Circle CenterX=0 CenterY=0 CenterZ=0 NormalX=0 NormalY=0 NormalZ=1 AngleXU=0 Radius=0.225
  constraints (2):
    c: Coincident(g0,g-1)
    c: Radius(g0) = 0.225
FEATURE [Sketcher::SketchObject] Sketch031
  MapMode = 5
  Placement = pos=(0,0,0) rot=(0.57735,0.57735,0.57735;2.0944rad)
  Support = -> [YZ_Plane017]
  expr: Constraints[11] = 2 / 2
  expr: Constraints[10] = 5.08
  sketch-geometry (5):
    g0: LineSegment StartX=-1.54 StartY=-1e-16 StartZ=0 EndX=1.54 EndY=-1e-16 EndZ=0
    g1: LineSegment StartX=-2.54 StartY=-1 StartZ=0 EndX=-2.54 EndY=-3.6 EndZ=0
    g2: LineSegment StartX=2.54 StartY=-1 StartZ=0 EndX=2.54 EndY=-3.6 EndZ=0
    g3: ArcOfCircle CenterX=-1.54 CenterY=-1 CenterZ=0 NormalX=0 NormalY=0 NormalZ=1 AngleXU=0 Radius=1 StartAngle=1.5708 EndAngle=3.14159
    g4: ArcOfCircle CenterX=1.54 CenterY=-1 CenterZ=0 NormalX=0 NormalY=0 NormalZ=1 AngleXU=0 Radius=1 StartAngle=7e-16 EndAngle=1.5708
  constraints (13):
    c: Vertical(g1)
    c: Vertical(g2)
    c: Equal(g2,g1)
    c: Tangent(g0,g3) = 1.5708
    c: Tangent(g1,g3) = -1.5708
    c: Tangent(g0,g4) = 1.5708
    c: Tangent(g2,g4) = 1.5708
    c: Symmetric(g0,g0,g-2)
    c: Equal(g4,g3)
    c: PointOnObject(g0,g-1)
    c: DistanceX(g1,g2) = 5.08
    c: DistanceY(g1,g0) = 1
    c: DistanceY(g1,g1) = 2.6
FEATURE [PartDesign::AdditivePipe] AdditivePipe013
  AuxilleryCurvelinear = true
  AuxillerySpineTangent = false
  Binormal = (0,0,0)
  Mode = 0
  Placement = pos=(0,0,0) rot=(1,0,0;1.5708rad)
  Profile = -> Sketch030
  Refine = true
  Spine = -> Sketch031
  SpineTangent = false
  Transformation = 0
  Transition = 0
FEATURE [PartDesign::Body] Body017  label="1/8W_5.08_H"
  Group = -> [Sketch031,Sketch030,AdditivePipe013]
  Origin = -> Origin017
  Tip = -> AdditivePipe013
FEATURE [PartDesign::FeatureBase] BaseFeature
  BaseFeature = -> Body017
FEATURE [PartDesign::AdditivePipe] AdditivePipe005
  AuxilleryCurvelinear = true
  AuxillerySpineTangent = false
  BaseFeature = -> BaseFeature
  Binormal = (0,0,0)
  Mode = 0
  Profile = -> Sketch014
  Refine = true
  Spine = -> Sketch015
  SpineTangent = false
  Transformation = 0
  Transition = 0
FEATURE [PartDesign::Body] Body009  label="Leads_P15.24"
  BaseFeature = -> Body017
  Group = -> [BaseFeature,Sketch015,Sketch014,AdditivePipe005]
  Origin = -> Origin009
  Tip = -> AdditivePipe005
FEATURE [App::DocumentObjectGroup] Group001  label="Old"
  Group = -> [Body,Body002,Body003,Body004,Body005,Body007,Body008,Body009]
FEATURE [Sketcher::SketchObject] Sketch032
  AttachmentOffset = pos=(0,0,0) rot=(0,0,1;-1.5708rad)
  MapMode = 5
  Placement = pos=(0,0,0) rot=(-0.57735,-0.57735,0.57735;4.18879rad)
  Support = -> [XZ_Plane018]
  expr: Constraints[1] = 2 / 2
  sketch-geometry (1):
    g0: Circle CenterX=0 CenterY=0 CenterZ=0 NormalX=0 NormalY=0 NormalZ=1 AngleXU=0 Radius=1
  constraints (2):
    c: Coincident(g0,g-1)
    c: Radius(g0) = 1
FEATURE [PartDesign::Pad] Pad003
  Length = 3.5
  Length2 = 100
  Midplane = true
  Placement = pos=(0,0,0) rot=(1,0,0;1.5708rad)
  Profile = -> Sketch032
  Type = 0
  expr: Length = 3.5
FEATURE [PartDesign::Body] Body018  label="1/8W_Body001"
  Group = -> [Sketch032,Pad003]
  Origin = -> Origin018
  Tip = -> Pad003
FEATURE [Sketcher::SketchObject] Sketch033
  AttachmentOffset = pos=(0,0,0) rot=(0,0,1;-1.5708rad)
  MapMode = 5
  Placement = pos=(0,0,0) rot=(-0.57735,-0.57735,0.57735;4.18879rad)
  Support = -> [XZ_Plane019]
  expr: Constraints[1] = 2 / 2
  sketch-geometry (1):
    g0: Circle CenterX=0 CenterY=0 CenterZ=0 NormalX=0 NormalY=0 NormalZ=1 AngleXU=0 Radius=1
  constraints (2):
    c: Coincident(g0,g-1)
    c: Radius(g0) = 1
FEATURE [PartDesign::Pad] Pad004
  Length = 3.5
  Length2 = 100
  Midplane = true
  Placement = pos=(0,0,0) rot=(1,0,0;1.5708rad)
  Profile = -> Sketch033
  Type = 0
  expr: Length = 3.5
FEATURE [PartDesign::Body] Body019  label="1/8W_Body002"
  Group = -> [Sketch033,Pad004]
  Origin = -> Origin019
  Tip = -> Pad004
FEATURE [Sketcher::SketchObject] Sketch034
  AttachmentOffset = pos=(0,0,0) rot=(0,0,1;-1.5708rad)
  MapMode = 5
  Placement = pos=(0,0,0) rot=(-0.57735,-0.57735,0.57735;4.18879rad)
  Support = -> [XZ_Plane020]
  expr: Constraints[1] = 2 / 2
  sketch-geometry (1):
    g0: Circle CenterX=0 CenterY=0 CenterZ=0 NormalX=0 NormalY=0 NormalZ=1 AngleXU=0 Radius=1
  constraints (2):
    c: Coincident(g0,g-1)
    c: Radius(g0) = 1
FEATURE [PartDesign::Pad] Pad005
  Length = 3.5
  Length2 = 100
  Midplane = true
  Placement = pos=(0,0,0) rot=(1,0,0;1.5708rad)
  Profile = -> Sketch034
  Type = 0
  expr: Length = 3.5
FEATURE [PartDesign::Body] Body020  label="1/8W_Body003"
  Group = -> [Sketch034,Pad005]
  Origin = -> Origin020
  Tip = -> Pad005
FEATURE [Sketcher::SketchObject] Sketch035
  AttachmentOffset = pos=(0,0,0) rot=(0,0,1;-1.5708rad)
  MapMode = 5
  Placement = pos=(0,0,0) rot=(-0.57735,-0.57735,0.57735;4.18879rad)
  Support = -> [XZ_Plane021]
  expr: Constraints[1] = 2 / 2
  sketch-geometry (1):
    g0: Circle CenterX=0 CenterY=0 CenterZ=0 NormalX=0 NormalY=0 NormalZ=1 AngleXU=0 Radius=1
  constraints (2):
    c: Coincident(g0,g-1)
    c: Radius(g0) = 1
FEATURE [PartDesign::Pad] Pad006
  Length = 3.5
  Length2 = 100
  Midplane = true
  Placement = pos=(0,0,0) rot=(1,0,0;1.5708rad)
  Profile = -> Sketch035
  Type = 0
  expr: Length = 3.5
FEATURE [PartDesign::Body] Body021  label="1/8W_Body004"
  Group = -> [Sketch035,Pad006]
  Origin = -> Origin021
  Tip = -> Pad006
FEATURE [Sketcher::SketchObject] Sketch036
  AttachmentOffset = pos=(0,0,0) rot=(0,0,1;-1.5708rad)
  MapMode = 5
  Placement = pos=(0,0,0) rot=(-0.57735,-0.57735,0.57735;4.18879rad)
  Support = -> [XZ_Plane022]
  expr: Constraints[1] = 2 / 2
  sketch-geometry (1):
    g0: Circle CenterX=0 CenterY=0 CenterZ=0 NormalX=0 NormalY=0 NormalZ=1 AngleXU=0 Radius=1
  constraints (2):
    c: Coincident(g0,g-1)
    c: Radius(g0) = 1
FEATURE [PartDesign::Pad] Pad007
  Length = 3.5
  Length2 = 100
  Midplane = true
  Placement = pos=(0,0,0) rot=(1,0,0;1.5708rad)
  Profile = -> Sketch036
  Type = 0
  expr: Length = 3.5
FEATURE [PartDesign::Body] Body022  label="1/8W_Body005"
  Group = -> [Sketch036,Pad007]
  Origin = -> Origin022
  Tip = -> Pad007
FEATURE [Sketcher::SketchObject] Sketch037
  AttachmentOffset = pos=(0,0,0) rot=(0,0,1;-1.5708rad)
  MapMode = 5
  Placement = pos=(0,0,0) rot=(-0.57735,-0.57735,0.57735;4.18879rad)
  Support = -> [XZ_Plane023]
  expr: Constraints[1] = 2 / 2
  sketch-geometry (1):
    g0: Circle CenterX=0 CenterY=0 CenterZ=0 NormalX=0 NormalY=0 NormalZ=1 AngleXU=0 Radius=1
  constraints (2):
    c: Coincident(g0,g-1)
    c: Radius(g0) = 1
FEATURE [PartDesign::Pad] Pad008
  Length = 3.5
  Length2 = 100
  Midplane = true
  Placement = pos=(0,0,0) rot=(1,0,0;1.5708rad)
  Profile = -> Sketch037
  Type = 0
  expr: Length = 3.5
FEATURE [PartDesign::Body] Body023  label="1/8W_Body006"
  Group = -> [Sketch037,Pad008]
  Origin = -> Origin023
  Tip = -> Pad008
FEATURE [Part::MultiFuse] Fusion  label="R_MF12_P2.54_V"
  Placement = pos=(-1.27,1e-15,1.75) rot=(0.57735,0.57735,-0.57735;4.18879rad)
  Shapes = -> [Body006,Body010]
FEATURE [Part::MultiFuse] Fusion001  label="R_MF12_P5.08_V"
  Placement = pos=(-2.54,-1e-16,1.75) rot=(0.57735,0.57735,-0.57735;4.18879rad)
  Shapes = -> [Body018,Body013]
FEATURE [Part::MultiFuse] Fusion002  label="R_MF12_P5.08_H"
  Placement = pos=(0,0,1) rot=(0,0,1;1.5708rad)
  Shapes = -> [Body017,Body019]
FEATURE [Part::MultiFuse] Fusion003  label="R_MF12_P7.62_H"
  Placement = pos=(0,0,1) rot=(0,0,1;4.71239rad)
  Shapes = -> [Body020,Body016]
FEATURE [Part::MultiFuse] Fusion004  label="R_MF12_P10.16_H"
  Placement = pos=(0,0,1) rot=(0,0,1;4.71239rad)
  Shapes = -> [Body021,Body012]
FEATURE [Part::MultiFuse] Fusion005  label="R_MF12_P12.70_H"
  Placement = pos=(0,0,1) rot=(0,0,-1;4.71239rad)
  Shapes = -> [Body022,Body014]
FEATURE [Part::MultiFuse] Fusion006  label="R_MF12_P15.24_H"
  Placement = pos=(0,0,1) rot=(0,0,1;4.71239rad)
  Shapes = -> [Body023,Body015]
FEATURE [App::DocumentObjectGroup] Group  label="1/8W_MF"
  Group = -> [Fusion,Fusion001,Fusion002,Fusion003,Fusion004,Fusion005,Fusion006]
FEATURE [Sketcher::SketchObject] Sketch038
  MapMode = 5
  Placement = pos=(0,0,0) rot=(0.57735,0.57735,0.57735;2.0944rad)
  Support = -> [YZ_Plane026]
  expr: Constraints[11] = 2 / 2
  expr: Constraints[10] = 4 * 2.54
  sketch-geometry (5):
    g0: LineSegment StartX=-4.08 StartY=0 StartZ=0 EndX=4.08 EndY=0 EndZ=0
    g1: LineSegment StartX=-5.08 StartY=-1 StartZ=0 EndX=-5.08 EndY=-3.6 EndZ=0
    g2: LineSegment StartX=5.08 StartY=-1 StartZ=0 EndX=5.08 EndY=-3.6 EndZ=0
    g3: ArcOfCircle CenterX=-4.08 CenterY=-1 CenterZ=0 NormalX=0 NormalY=0 NormalZ=1 AngleXU=0 Radius=1 StartAngle=1.5708 EndAngle=3.14159
    g4: ArcOfCircle CenterX=4.08 CenterY=-1 CenterZ=0 NormalX=0 NormalY=0 NormalZ=1 AngleXU=0 Radius=1 StartAngle=0 EndAngle=1.5708
  constraints (13):
    c: Vertical(g1)
    c: Vertical(g2)
    c: Equal(g2,g1)
    c: Tangent(g0,g3) = 1.5708
    c: Tangent(g1,g3) = -1.5708
    c: Tangent(g0,g4) = 1.5708
    c: Tangent(g2,g4) = 1.5708
    c: Symmetric(g0,g0,g-2)
    c: Equal(g4,g3)
    c: PointOnObject(g0,g-1)
    c: DistanceX(g1,g2) = 10.16
    c: DistanceY(g1,g0) = 1
    c: DistanceY(g1,g1) = 2.6
FEATURE [Sketcher::SketchObject] Sketch039
  AttachmentOffset = pos=(0,0,0) rot=(0,0,1;-1.5708rad)
  MapMode = 5
  Placement = pos=(0,0,0) rot=(-0.57735,-0.57735,0.57735;4.18879rad)
  Support = -> [XZ_Plane026]
  expr: Constraints[1] = 0.45 / 2
  sketch-geometry (1):
    g0: Circle CenterX=0 CenterY=0 CenterZ=0 NormalX=0 NormalY=0 NormalZ=1 AngleXU=0 Radius=0.225
  constraints (2):
    c: Coincident(g0,g-1)
    c: Radius(g0) = 0.225
FEATURE [Sketcher::SketchObject] Sketch040
  MapMode = 5
  Placement = pos=(0,0,0) rot=(0.57735,0.57735,0.57735;2.0944rad)
  Support = -> [YZ_Plane027]
  expr: Constraints[24] = 2.54
  expr: Constraints[15] = 2 / 2
  expr: Constraints[10] = 3.5 / 2
  expr: Constraints[4] = 3.5 / 2
  sketch-geometry (9):
    g0: LineSegment StartX=4.35 StartY=0 StartZ=0 EndX=-1.75 EndY=1e-16 EndZ=0
    g1: LineSegment StartX=-1.75 StartY=-2.54 StartZ=0 EndX=4.35 EndY=-2.54 EndZ=0
    g2: GeomPoint X=1.75 Y=0 Z=0
    g3: GeomPoint X=1.75 Y=-2.54 Z=0
    g4: GeomPoint X=-2.75 Y=-1 Z=0
    g5: GeomPoint X=-1.75 Y=0 Z=0
    g6: ArcOfCircle CenterX=-1.75 CenterY=-1 CenterZ=0 NormalX=0 NormalY=0 NormalZ=1 AngleXU=0 Radius=1 StartAngle=1.5708 EndAngle=3.14159
    g7: LineSegment StartX=-2.75 StartY=-1 StartZ=0 EndX=-2.75 EndY=-1.54 EndZ=0
    g8: ArcOfCircle CenterX=-1.75 CenterY=-1.54 CenterZ=0 NormalX=0 NormalY=0 NormalZ=1 AngleXU=0 Radius=1 StartAngle=3.14159 EndAngle=4.71239
  constraints (25):
    c: PointOnObject(g0,g-1)
    c: PointOnObject(g0,g-1)
    c: Horizontal(g1)
    c: PointOnObject(g2,g0)
    c: DistanceX(g-1,g2) = 1.75
    c: DistanceX(g2,g0) = 2.6
    c: PointOnObject(g3,g1)
    c: DistanceX(g3,g1) = 2.6
    c: Vertical(g0,g1)
    c: PointOnObject(g5,g0)
    c: DistanceX(g5,g-1) = 1.75
    c: DistanceX(g0,g5) = 0
    c: Coincident(g6,g0)
    c: Coincident(g6,g4)
    c: Horizontal(g6,g4)
    c: Radius(g6) = 1
    c: Vertical(g6,g0)
    c: Coincident(g7,g4)
    c: Vertical(g7)
    c: Coincident(g8,g7)
    c: Coincident(g8,g1)
    c: Equal(g8,g6)
    c: Horizontal(g8,g7)
    c: Vertical(g8,g1)
    c: DistanceY(g1,g0) = 2.54
FEATURE [Sketcher::SketchObject] Sketch041
  AttachmentOffset = pos=(0,0,0) rot=(0,0,1;-1.5708rad)
  MapMode = 5
  Placement = pos=(0,0,0) rot=(-0.57735,-0.57735,0.57735;4.18879rad)
  Support = -> [XZ_Plane025]
  expr: Constraints[1] = 2 / 2
  sketch-geometry (1):
    g0: Circle CenterX=0 CenterY=0 CenterZ=0 NormalX=0 NormalY=0 NormalZ=1 AngleXU=0 Radius=1
  constraints (2):
    c: Coincident(g0,g-1)
    c: Radius(g0) = 1
FEATURE [PartDesign::Pad] Pad014
  Length = 3.5
  Length2 = 100
  Midplane = true
  Placement = pos=(0,0,0) rot=(1,0,0;1.5708rad)
  Profile = -> Sketch041
  Type = 0
  expr: Length = 3.5
FEATURE [PartDesign::Body] Body026  label="1/8W_Body007"
  Group = -> [Sketch041,Pad014]
  Origin = -> Origin024
  Tip = -> Pad014
FEATURE [PartDesign::AdditivePipe] AdditivePipe014
  AuxilleryCurvelinear = true
  AuxillerySpineTangent = false
  Binormal = (0,0,0)
  Mode = 0
  Placement = pos=(0,0,0) rot=(1,0,0;1.5708rad)
  Profile = -> Sketch039
  Refine = true
  Spine = -> Sketch038
  SpineTangent = false
  Transformation = 0
  Transition = 0
FEATURE [PartDesign::Body] Body025  label="1/8W_10.16_H001"
  Group = -> [Sketch038,Sketch039,AdditivePipe014]
  Origin = -> Origin032
  Tip = -> AdditivePipe014
FEATURE [Sketcher::SketchObject] Sketch042
  AttachmentOffset = pos=(0,0,0) rot=(0,0,1;-1.5708rad)
  MapMode = 5
  Placement = pos=(0,0,0) rot=(-0.57735,-0.57735,0.57735;4.18879rad)
  Support = -> [XZ_Plane024]
  expr: Constraints[1] = 0.45 / 2
  sketch-geometry (1):
    g0: Circle CenterX=0 CenterY=0 CenterZ=0 NormalX=0 NormalY=0 NormalZ=1 AngleXU=0 Radius=0.225
  constraints (2):
    c: Coincident(g0,g-1)
    c: Radius(g0) = 0.225
FEATURE [Sketcher::SketchObject] Sketch043
  AttachmentOffset = pos=(0,0,0) rot=(0,0,1;-1.5708rad)
  MapMode = 5
  Placement = pos=(0,0,0) rot=(-0.57735,-0.57735,0.57735;4.18879rad)
  Support = -> [XZ_Plane028]
  expr: Constraints[1] = 0.45 / 2
  sketch-geometry (1):
    g0: Circle CenterX=0 CenterY=0 CenterZ=0 NormalX=0 NormalY=0 NormalZ=1 AngleXU=0 Radius=0.225
  constraints (2):
    c: Coincident(g0,g-1)
    c: Radius(g0) = 0.225
FEATURE [Sketcher::SketchObject] Sketch044
  AttachmentOffset = pos=(0,0,0) rot=(0,0,1;-1.5708rad)
  MapMode = 5
  Placement = pos=(0,0,0) rot=(-0.57735,-0.57735,0.57735;4.18879rad)
  Support = -> [XZ_Plane032]
  expr: Constraints[1] = 2 / 2
  sketch-geometry (1):
    g0: Circle CenterX=0 CenterY=0 CenterZ=0 NormalX=0 NormalY=0 NormalZ=1 AngleXU=0 Radius=1
  constraints (2):
    c: Coincident(g0,g-1)
    c: Radius(g0) = 1
FEATURE [PartDesign::Pad] Pad015
  Length = 3.5
  Length2 = 100
  Midplane = true
  Placement = pos=(0,0,0) rot=(1,0,0;1.5708rad)
  Profile = -> Sketch044
  Type = 0
  expr: Length = 3.5
FEATURE [Sketcher::SketchObject] Sketch045
  AttachmentOffset = pos=(0,0,0) rot=(0,0,1;-1.5708rad)
  MapMode = 5
  Placement = pos=(0,0,0) rot=(-0.57735,-0.57735,0.57735;4.18879rad)
  Support = -> [XZ_Plane027]
  expr: Constraints[1] = 0.45 / 2
  sketch-geometry (1):
    g0: Circle CenterX=0 CenterY=0 CenterZ=0 NormalX=0 NormalY=0 NormalZ=1 AngleXU=0 Radius=0.225
  constraints (2):
    c: Coincident(g0,g-1)
    c: Radius(g0) = 0.225
FEATURE [PartDesign::AdditivePipe] AdditivePipe015
  AuxilleryCurvelinear = true
  AuxillerySpineTangent = false
  Binormal = (0,0,0)
  Mode = 0
  Placement = pos=(0,0,0) rot=(1,0,0;1.5708rad)
  Profile = -> Sketch045
  Refine = true
  Spine = -> Sketch040
  SpineTangent = false
  Transformation = 0
  Transition = 0
FEATURE [PartDesign::Body] Body024  label="1/8W_2.54_V001"
  Group = -> [Sketch040,Sketch045,AdditivePipe015]
  Origin = -> Origin031
  Tip = -> AdditivePipe015
FEATURE [Part::MultiFuse] Fusion007  label="R_CF12_P2.54_V"
  Placement = pos=(-1.27,1e-15,1.75) rot=(0.57735,0.57735,-0.57735;4.18879rad)
  Shapes = -> [Body026,Body024]
FEATURE [Sketcher::SketchObject] Sketch046
  MapMode = 5
  Placement = pos=(0,0,0) rot=(0.57735,0.57735,0.57735;2.0944rad)
  Support = -> [YZ_Plane025]
  expr: Constraints[18] = 2 / 2
  expr: Constraints[9] = 3.5 / 2
  expr: Constraints[3] = 3.5 / 2
  sketch-geometry (8):
    g0: LineSegment StartX=4.35 StartY=0 StartZ=0 EndX=-1.75 EndY=0 EndZ=0
    g1: LineSegment StartX=-1.75 StartY=-5.08 StartZ=0 EndX=4.35 EndY=-5.08 EndZ=0
    g2: GeomPoint X=1.75 Y=0 Z=0
    g3: GeomPoint X=1.75 Y=-5.08 Z=0
    g4: GeomPoint X=-1.75 Y=0 Z=0
    g5: LineSegment StartX=-2.75 StartY=-1 StartZ=0 EndX=-2.75 EndY=-4.08 EndZ=0
    g6: ArcOfCircle CenterX=-1.75 CenterY=-1 CenterZ=0 NormalX=0 NormalY=0 NormalZ=1 AngleXU=0 Radius=1 StartAngle=1.5708 EndAngle=3.14159
    g7: ArcOfCircle CenterX=-1.75 CenterY=-4.08 CenterZ=0 NormalX=0 NormalY=0 NormalZ=1 AngleXU=0 Radius=1 StartAngle=3.14159 EndAngle=4.71239
  constraints (20):
    c: PointOnObject(g0,g-1)
    c: Horizontal(g1)
    c: PointOnObject(g2,g0)
    c: DistanceX(g-1,g2) = 1.75
    c: DistanceX(g2,g0) = 2.6
    c: PointOnObject(g3,g1)
    c: DistanceX(g3,g1) = 2.6
    c: Vertical(g0,g1)
    c: PointOnObject(g4,g0)
    c: DistanceX(g4,g-1) = 1.75
    c: Vertical(g5)
    c: Tangent(g0,g6) = -1.5708
    c: Tangent(g5,g6) = -1.5708
    c: Tangent(g1,g7) = -1.5708
    c: Tangent(g5,g7) = -1.5708
    c: DistanceY(g1,g0) = 5.08
    c: PointOnObject(g0,g-1)
    c: Equal(g7,g6)
    c: Radius(g6) = 1
    c: DistanceX(g0,g4) = 0
FEATURE [PartDesign::AdditivePipe] AdditivePipe018
  AuxilleryCurvelinear = true
  AuxillerySpineTangent = false
  Binormal = (0,0,0)
  Mode = 0
  Placement = pos=(0,0,0) rot=(1,0,0;1.5708rad)
  Profile = -> Sketch042
  Refine = true
  Spine = -> Sketch046
  SpineTangent = false
  Transformation = 0
  Transition = 0
FEATURE [PartDesign::Body] Body030  label="1/8W_5.08_V001"
  Group = -> [Sketch046,Sketch042,AdditivePipe018]
  Origin = -> Origin033
  Tip = -> AdditivePipe018
FEATURE [Sketcher::SketchObject] Sketch047
  MapMode = 5
  Placement = pos=(0,0,0) rot=(0.57735,0.57735,0.57735;2.0944rad)
  Support = -> [YZ_Plane028]
  expr: Constraints[11] = 2 / 2
  expr: Constraints[10] = 12.7
  sketch-geometry (5):
    g0: LineSegment StartX=-5.35 StartY=0 StartZ=0 EndX=5.35 EndY=0 EndZ=0
    g1: LineSegment StartX=-6.35 StartY=-1 StartZ=0 EndX=-6.35 EndY=-3.6 EndZ=0
    g2: LineSegment StartX=6.35 StartY=-1 StartZ=0 EndX=6.35 EndY=-3.6 EndZ=0
    g3: ArcOfCircle CenterX=-5.35 CenterY=-1 CenterZ=0 NormalX=0 NormalY=0 NormalZ=1 AngleXU=0 Radius=1 StartAngle=1.5708 EndAngle=3.14159
    g4: ArcOfCircle CenterX=5.35 CenterY=-1 CenterZ=0 NormalX=0 NormalY=0 NormalZ=1 AngleXU=0 Radius=1 StartAngle=0 EndAngle=1.5708
  constraints (13):
    c: Vertical(g1)
    c: Vertical(g2)
    c: Equal(g2,g1)
    c: Tangent(g0,g3) = 1.5708
    c: Tangent(g1,g3) = -1.5708
    c: Tangent(g0,g4) = 1.5708
    c: Tangent(g2,g4) = 1.5708
    c: Symmetric(g0,g0,g-2)
    c: Equal(g4,g3)
    c: PointOnObject(g0,g-1)
    c: DistanceX(g1,g2) = 12.7
    c: DistanceY(g1,g0) = 1
    c: DistanceY(g1,g1) = 2.6
FEATURE [Sketcher::SketchObject] Sketch048
  MapMode = 5
  Placement = pos=(0,0,0) rot=(0.57735,0.57735,0.57735;2.0944rad)
  Support = -> [YZ_Plane029]
  expr: Constraints[11] = 2 / 2
  expr: Constraints[10] = 15.24
  sketch-geometry (5):
    g0: LineSegment StartX=-6.62 StartY=0 StartZ=0 EndX=6.62 EndY=0 EndZ=0
    g1: LineSegment StartX=-7.62 StartY=-1 StartZ=0 EndX=-7.62 EndY=-3.6 EndZ=0
    g2: LineSegment StartX=7.62 StartY=-1 StartZ=0 EndX=7.62 EndY=-3.6 EndZ=0
    g3: ArcOfCircle CenterX=-6.62 CenterY=-1 CenterZ=0 NormalX=0 NormalY=0 NormalZ=1 AngleXU=0 Radius=1 StartAngle=1.5708 EndAngle=3.14159
    g4: ArcOfCircle CenterX=6.62 CenterY=-1 CenterZ=0 NormalX=0 NormalY=0 NormalZ=1 AngleXU=0 Radius=1 StartAngle=0 EndAngle=1.5708
  constraints (13):
    c: Vertical(g1)
    c: Vertical(g2)
    c: Equal(g2,g1)
    c: Tangent(g0,g3) = 1.5708
    c: Tangent(g1,g3) = -1.5708
    c: Tangent(g0,g4) = 1.5708
    c: Tangent(g2,g4) = 1.5708
    c: Symmetric(g0,g0,g-2)
    c: Equal(g4,g3)
    c: PointOnObject(g0,g-1)
    c: DistanceX(g1,g2) = 15.24
    c: DistanceY(g1,g0) = 1
    c: DistanceY(g1,g1) = 2.6
FEATURE [PartDesign::AdditivePipe] AdditivePipe016
  AuxilleryCurvelinear = true
  AuxillerySpineTangent = false
  Binormal = (0,0,0)
  Mode = 0
  Placement = pos=(0,0,0) rot=(1,0,0;1.5708rad)
  Profile = -> Sketch043
  Refine = true
  Spine = -> Sketch048
  SpineTangent = false
  Transformation = 0
  Transition = 0
FEATURE [PartDesign::Body] Body029  label="1/8W_15.24_H001"
  Group = -> [Sketch048,Sketch043,AdditivePipe016]
  Origin = -> Origin037
  Tip = -> AdditivePipe016
FEATURE [Sketcher::SketchObject] Sketch049
  AttachmentOffset = pos=(0,0,0) rot=(0,0,1;-1.5708rad)
  MapMode = 5
  Placement = pos=(0,0,0) rot=(-0.57735,-0.57735,0.57735;4.18879rad)
  Support = -> [XZ_Plane029]
  expr: Constraints[1] = 0.45 / 2
  sketch-geometry (1):
    g0: Circle CenterX=0 CenterY=0 CenterZ=0 NormalX=0 NormalY=0 NormalZ=1 AngleXU=0 Radius=0.225
  constraints (2):
    c: Coincident(g0,g-1)
    c: Radius(g0) = 0.225
FEATURE [PartDesign::AdditivePipe] AdditivePipe017
  AuxilleryCurvelinear = true
  AuxillerySpineTangent = false
  Binormal = (0,0,0)
  Mode = 0
  Placement = pos=(0,0,0) rot=(1,0,0;1.5708rad)
  Profile = -> Sketch049
  Refine = true
  Spine = -> Sketch047
  SpineTangent = false
  Transformation = 0
  Transition = 0
FEATURE [PartDesign::Body] Body028  label="1/8W_12.70_H001"
  Group = -> [Sketch047,Sketch049,AdditivePipe017]
  Origin = -> Origin034
  Tip = -> AdditivePipe017
FEATURE [Sketcher::SketchObject] Sketch050
  AttachmentOffset = pos=(0,0,0) rot=(0,0,1;-1.5708rad)
  MapMode = 5
  Placement = pos=(0,0,0) rot=(-0.57735,-0.57735,0.57735;4.18879rad)
  Support = -> [XZ_Plane034]
  expr: Constraints[1] = 2 / 2
  sketch-geometry (1):
    g0: Circle CenterX=0 CenterY=0 CenterZ=0 NormalX=0 NormalY=0 NormalZ=1 AngleXU=0 Radius=1
  constraints (2):
    c: Coincident(g0,g-1)
    c: Radius(g0) = 1
FEATURE [PartDesign::Pad] Pad012
  Length = 3.5
  Length2 = 100
  Midplane = true
  Placement = pos=(0,0,0) rot=(1,0,0;1.5708rad)
  Profile = -> Sketch050
  Type = 0
  expr: Length = 3.5
FEATURE [Sketcher::SketchObject] Sketch051
  AttachmentOffset = pos=(0,0,0) rot=(0,0,1;-1.5708rad)
  MapMode = 5
  Placement = pos=(0,0,0) rot=(-0.57735,-0.57735,0.57735;4.18879rad)
  Support = -> [XZ_Plane036]
  expr: Constraints[1] = 2 / 2
  sketch-geometry (1):
    g0: Circle CenterX=0 CenterY=0 CenterZ=0 NormalX=0 NormalY=0 NormalZ=1 AngleXU=0 Radius=1
  constraints (2):
    c: Coincident(g0,g-1)
    c: Radius(g0) = 1
FEATURE [PartDesign::Pad] Pad011
  Length = 3.5
  Length2 = 100
  Midplane = true
  Placement = pos=(0,0,0) rot=(1,0,0;1.5708rad)
  Profile = -> Sketch051
  Type = 0
  expr: Length = 3.5
FEATURE [Sketcher::SketchObject] Sketch052
  AttachmentOffset = pos=(0,0,0) rot=(0,0,1;-1.5708rad)
  MapMode = 5
  Placement = pos=(0,0,0) rot=(-0.57735,-0.57735,0.57735;4.18879rad)
  Support = -> [XZ_Plane030]
  expr: Constraints[1] = 0.45 / 2
  sketch-geometry (1):
    g0: Circle CenterX=0 CenterY=0 CenterZ=0 NormalX=0 NormalY=0 NormalZ=1 AngleXU=0 Radius=0.225
  constraints (2):
    c: Coincident(g0,g-1)
    c: Radius(g0) = 0.225
FEATURE [Sketcher::SketchObject] Sketch053
  AttachmentOffset = pos=(0,0,0) rot=(0,0,1;-1.5708rad)
  MapMode = 5
  Placement = pos=(0,0,0) rot=(-0.57735,-0.57735,0.57735;4.18879rad)
  Support = -> [XZ_Plane033]
  expr: Constraints[1] = 2 / 2
  sketch-geometry (1):
    g0: Circle CenterX=0 CenterY=0 CenterZ=0 NormalX=0 NormalY=0 NormalZ=1 AngleXU=0 Radius=1
  constraints (2):
    c: Coincident(g0,g-1)
    c: Radius(g0) = 1
FEATURE [PartDesign::Pad] Pad013
  Length = 3.5
  Length2 = 100
  Midplane = true
  Placement = pos=(0,0,0) rot=(1,0,0;1.5708rad)
  Profile = -> Sketch053
  Type = 0
  expr: Length = 3.5
FEATURE [Sketcher::SketchObject] Sketch054
  AttachmentOffset = pos=(0,0,0) rot=(0,0,1;-1.5708rad)
  MapMode = 5
  Placement = pos=(0,0,0) rot=(-0.57735,-0.57735,0.57735;4.18879rad)
  Support = -> [XZ_Plane037]
  expr: Constraints[1] = 2 / 2
  sketch-geometry (1):
    g0: Circle CenterX=0 CenterY=0 CenterZ=0 NormalX=0 NormalY=0 NormalZ=1 AngleXU=0 Radius=1
  constraints (2):
    c: Coincident(g0,g-1)
    c: Radius(g0) = 1
FEATURE [PartDesign::Pad] Pad009
  Length = 3.5
  Length2 = 100
  Midplane = true
  Placement = pos=(0,0,0) rot=(1,0,0;1.5708rad)
  Profile = -> Sketch054
  Type = 0
  expr: Length = 3.5
FEATURE [Sketcher::SketchObject] Sketch055
  AttachmentOffset = pos=(0,0,0) rot=(0,0,1;-1.5708rad)
  MapMode = 5
  Placement = pos=(0,0,0) rot=(-0.57735,-0.57735,0.57735;4.18879rad)
  Support = -> [XZ_Plane035]
  expr: Constraints[1] = 2 / 2
  sketch-geometry (1):
    g0: Circle CenterX=0 CenterY=0 CenterZ=0 NormalX=0 NormalY=0 NormalZ=1 AngleXU=0 Radius=1
  constraints (2):
    c: Coincident(g0,g-1)
    c: Radius(g0) = 1
FEATURE [PartDesign::Pad] Pad010
  Length = 3.5
  Length2 = 100
  Midplane = true
  Placement = pos=(0,0,0) rot=(1,0,0;1.5708rad)
  Profile = -> Sketch055
  Type = 0
  expr: Length = 3.5
FEATURE [PartDesign::Body] Body027  label="1/8W_Body008"
  Group = -> [Sketch055,Pad010]
  Origin = -> Origin030
  Tip = -> Pad010
FEATURE [Sketcher::SketchObject] Sketch056
  AttachmentOffset = pos=(0,0,0) rot=(0,0,1;-1.5708rad)
  MapMode = 5
  Placement = pos=(0,0,0) rot=(-0.57735,-0.57735,0.57735;4.18879rad)
  Support = -> [XZ_Plane031]
  expr: Constraints[1] = 0.45 / 2
  sketch-geometry (1):
    g0: Circle CenterX=0 CenterY=0 CenterZ=0 NormalX=0 NormalY=0 NormalZ=1 AngleXU=0 Radius=0.225
  constraints (2):
    c: Coincident(g0,g-1)
    c: Radius(g0) = 0.225
FEATURE [Sketcher::SketchObject] Sketch057
  MapMode = 5
  Placement = pos=(0,0,0) rot=(0.57735,0.57735,0.57735;2.0944rad)
  Support = -> [YZ_Plane031]
  expr: Constraints[11] = 2 / 2
  expr: Constraints[10] = 5.08
  sketch-geometry (5):
    g0: LineSegment StartX=-1.54 StartY=-1e-16 StartZ=0 EndX=1.54 EndY=-1e-16 EndZ=0
    g1: LineSegment StartX=-2.54 StartY=-1 StartZ=0 EndX=-2.54 EndY=-3.6 EndZ=0
    g2: LineSegment StartX=2.54 StartY=-1 StartZ=0 EndX=2.54 EndY=-3.6 EndZ=0
    g3: ArcOfCircle CenterX=-1.54 CenterY=-1 CenterZ=0 NormalX=0 NormalY=0 NormalZ=1 AngleXU=0 Radius=1 StartAngle=1.5708 EndAngle=3.14159
    g4: ArcOfCircle CenterX=1.54 CenterY=-1 CenterZ=0 NormalX=0 NormalY=0 NormalZ=1 AngleXU=0 Radius=1 StartAngle=7e-16 EndAngle=1.5708
  constraints (13):
    c: Vertical(g1)
    c: Vertical(g2)
    c: Equal(g2,g1)
    c: Tangent(g0,g3) = 1.5708
    c: Tangent(g1,g3) = -1.5708
    c: Tangent(g0,g4) = 1.5708
    c: Tangent(g2,g4) = 1.5708
    c: Symmetric(g0,g0,g-2)
    c: Equal(g4,g3)
    c: PointOnObject(g0,g-1)
    c: DistanceX(g1,g2) = 5.08
    c: DistanceY(g1,g0) = 1
    c: DistanceY(g1,g1) = 2.6
FEATURE [PartDesign::AdditivePipe] AdditivePipe020
  AuxilleryCurvelinear = true
  AuxillerySpineTangent = false
  Binormal = (0,0,0)
  Mode = 0
  Placement = pos=(0,0,0) rot=(1,0,0;1.5708rad)
  Profile = -> Sketch052
  Refine = true
  Spine = -> Sketch057
  SpineTangent = false
  Transformation = 0
  Transition = 0
FEATURE [Sketcher::SketchObject] Sketch058
  MapMode = 5
  Placement = pos=(0,0,0) rot=(0.57735,0.57735,0.57735;2.0944rad)
  Support = -> [YZ_Plane033]
  expr: Constraints[11] = 2 / 2
  expr: Constraints[10] = 3 * 2.54
  sketch-geometry (5):
    g0: LineSegment StartX=-2.81 StartY=0 StartZ=0 EndX=2.81 EndY=0 EndZ=0
    g1: LineSegment StartX=-3.81 StartY=-1 StartZ=0 EndX=-3.81 EndY=-3.6 EndZ=0
    g2: LineSegment StartX=3.81 StartY=-1 StartZ=0 EndX=3.81 EndY=-3.6 EndZ=0
    g3: ArcOfCircle CenterX=-2.81 CenterY=-1 CenterZ=0 NormalX=0 NormalY=0 NormalZ=1 AngleXU=0 Radius=1 StartAngle=1.5708 EndAngle=3.14159
    g4: ArcOfCircle CenterX=2.81 CenterY=-1 CenterZ=0 NormalX=0 NormalY=0 NormalZ=1 AngleXU=0 Radius=1 StartAngle=0 EndAngle=1.5708
  constraints (13):
    c: Vertical(g1)
    c: Vertical(g2)
    c: Equal(g2,g1)
    c: Tangent(g0,g3) = 1.5708
    c: Tangent(g1,g3) = -1.5708
    c: Tangent(g0,g4) = 1.5708
    c: Tangent(g2,g4) = 1.5708
    c: Symmetric(g0,g0,g-2)
    c: Equal(g4,g3)
    c: PointOnObject(g0,g-1)
    c: DistanceX(g1,g2) = 7.62
    c: DistanceY(g1,g0) = 1
    c: DistanceY(g1,g1) = 2.6
FEATURE [PartDesign::AdditivePipe] AdditivePipe019
  AuxilleryCurvelinear = true
  AuxillerySpineTangent = false
  Binormal = (0,0,0)
  Mode = 0
  Placement = pos=(0,0,0) rot=(1,0,0;1.5708rad)
  Profile = -> Sketch056
  Refine = true
  Spine = -> Sketch058
  SpineTangent = false
  Transformation = 0
  Transition = 0
FEATURE [PartDesign::Body] Body031  label="1/8W_Body009"
  Group = -> [Sketch051,Pad011]
  Origin = -> Origin025
  Tip = -> Pad011
FEATURE [PartDesign::Body] Body032  label="1/8W_5.08_H001"
  Group = -> [Sketch057,Sketch052,AdditivePipe020]
  Origin = -> Origin035
  Tip = -> AdditivePipe020
FEATURE [PartDesign::Body] Body033  label="1/8W_Body010"
  Group = -> [Sketch050,Pad012]
  Origin = -> Origin028
  Tip = -> Pad012
FEATURE [PartDesign::Body] Body034  label="1/8W_Body011"
  Group = -> [Sketch044,Pad015]
  Origin = -> Origin027
  Tip = -> Pad015
FEATURE [Part::MultiFuse] Fusion010  label="R_CF12_P5.08_V"
  Placement = pos=(-2.54,0,1.75) rot=(0.57735,0.57735,-0.57735;4.18879rad)
  Shapes = -> [Body034,Body030]
FEATURE [PartDesign::Body] Body035  label="1/8W_Body012"
  Group = -> [Sketch053,Pad013]
  Origin = -> Origin029
  Tip = -> Pad013
FEATURE [Part::MultiFuse] Fusion008  label="R_CF12_P5.08_H"
  Placement = pos=(0,0,1) rot=(0,0,1;1.5708rad)
  Shapes = -> [Body032,Body035]
FEATURE [PartDesign::Body] Body036  label="1/8W_7.62_H001"
  Group = -> [Sketch058,Sketch056,AdditivePipe019]
  Origin = -> Origin036
  Tip = -> AdditivePipe019
FEATURE [Part::MultiFuse] Fusion009  label="R_CF12_P7.62_H"
  Placement = pos=(0,0,1) rot=(0,0,-1;1.5708rad)
  Shapes = -> [Body033,Body036]
FEATURE [PartDesign::Body] Body037  label="1/8W_Body013"
  Group = -> [Sketch054,Pad009]
  Origin = -> Origin026
  Tip = -> Pad009
FEATURE [Part::MultiFuse] Fusion011  label="R_CF12_P15.24_H"
  Placement = pos=(0,0,1) rot=(0,0,-1;1.5708rad)
  Shapes = -> [Body037,Body029]
FEATURE [Part::MultiFuse] Fusion012  label="R_CF12_P12.70_H"
  Placement = pos=(0,0,1) rot=(0,0,1;1.5708rad)
  Shapes = -> [Body031,Body028]
FEATURE [Part::MultiFuse] Fusion013  label="R_CF12_P10.16_H"
  Placement = pos=(0,0,1) rot=(0,0,-1;1.5708rad)
  Shapes = -> [Body027,Body025]
FEATURE [App::DocumentObjectGroup] Group002  label="1/8W_CF"
  Group = -> [Fusion007,Fusion010,Fusion008,Fusion009,Fusion013,Fusion012,Fusion011]
FEATURE [Sketcher::SketchObject] Sketch059
  MapMode = 5
  Placement = pos=(0,0,0) rot=(0.57735,0.57735,0.57735;2.0944rad)
  Support = -> [YZ_Plane040]
  expr: Constraints[11] = 2.5 / 2
  expr: Constraints[10] = 4 * 2.54
  sketch-geometry (5):
    g0: LineSegment StartX=-3.83 StartY=-4e-16 StartZ=0 EndX=3.83 EndY=-1.3e-15 EndZ=0
    g1: LineSegment StartX=-5.08 StartY=-1.25 StartZ=0 EndX=-5.08 EndY=-3.85 EndZ=0
    g2: LineSegment StartX=5.08 StartY=-1.25 StartZ=0 EndX=5.08 EndY=-3.85 EndZ=0
    g3: ArcOfCircle CenterX=-3.83 CenterY=-1.25 CenterZ=0 NormalX=0 NormalY=0 NormalZ=1 AngleXU=0 Radius=1.25 StartAngle=1.5708 EndAngle=3.14159
    g4: ArcOfCircle CenterX=3.83 CenterY=-1.25 CenterZ=0 NormalX=0 NormalY=0 NormalZ=1 AngleXU=0 Radius=1.25 StartAngle=0 EndAngle=1.5708
  constraints (13):
    c: Vertical(g1)
    c: Vertical(g2)
    c: Equal(g2,g1)
    c: Tangent(g0,g3) = 1.5708
    c: Tangent(g1,g3) = -1.5708
    c: Tangent(g0,g4) = 1.5708
    c: Tangent(g2,g4) = 1.5708
    c: Symmetric(g0,g0,g-2)
    c: Equal(g4,g3)
    c: PointOnObject(g0,g-1)
    c: DistanceX(g1,g2) = 10.16
    c: DistanceY(g1,g0) = 1.25
    c: DistanceY(g1,g1) = 2.6
FEATURE [Sketcher::SketchObject] Sketch060
  AttachmentOffset = pos=(0,0,0) rot=(0,0,1;-1.5708rad)
  MapMode = 5
  Placement = pos=(0,0,0) rot=(-0.57735,-0.57735,0.57735;4.18879rad)
  Support = -> [XZ_Plane040]
  expr: Constraints[1] = 0.55 / 2
  sketch-geometry (1):
    g0: Circle CenterX=0 CenterY=0 CenterZ=0 NormalX=0 NormalY=0 NormalZ=1 AngleXU=0 Radius=0.275
  constraints (2):
    c: Coincident(g0,g-1)
    c: Radius(g0) = 0.275
FEATURE [Sketcher::SketchObject] Sketch061
  MapMode = 5
  Placement = pos=(0,0,0) rot=(0.57735,0.57735,0.57735;2.0944rad)
  Support = -> [YZ_Plane041]
  expr: Constraints[24] = 2.54
  expr: Constraints[15] = 2.5 / 2
  expr: Constraints[10] = 6.5 / 2
  expr: Constraints[4] = 6.5 / 2
  sketch-geometry (9):
    g0: LineSegment StartX=5.85 StartY=0 StartZ=0 EndX=-3.25 EndY=0 EndZ=0
    g1: LineSegment StartX=-3.25 StartY=-2.54 StartZ=0 EndX=5.85 EndY=-2.54 EndZ=0
    g2: GeomPoint X=3.25 Y=0 Z=0
    g3: GeomPoint X=3.25 Y=-2.54 Z=0
    g4: GeomPoint X=-4.5 Y=-1.25 Z=0
    g5: GeomPoint X=-3.25 Y=0 Z=0
    g6: ArcOfCircle CenterX=-3.25 CenterY=-1.25 CenterZ=0 NormalX=0 NormalY=0 NormalZ=1 AngleXU=0 Radius=1.25 StartAngle=1.5708 EndAngle=3.14159
    g7: LineSegment StartX=-4.5 StartY=-1.25 StartZ=0 EndX=-4.5 EndY=-1.29 EndZ=0
    g8: ArcOfCircle CenterX=-3.25 CenterY=-1.29 CenterZ=0 NormalX=0 NormalY=0 NormalZ=1 AngleXU=0 Radius=1.25 StartAngle=3.14159 EndAngle=4.71239
  constraints (25):
    c: PointOnObject(g0,g-1)
    c: PointOnObject(g0,g-1)
    c: Horizontal(g1)
    c: PointOnObject(g2,g0)
    c: DistanceX(g-1,g2) = 3.25
    c: DistanceX(g2,g0) = 2.6
    c: PointOnObject(g3,g1)
    c: DistanceX(g3,g1) = 2.6
    c: Vertical(g0,g1)
    c: PointOnObject(g5,g0)
    c: DistanceX(g5,g-1) = 3.25
    c: DistanceX(g0,g5) = 0
    c: Coincident(g6,g0)
    c: Coincident(g6,g4)
    c: Horizontal(g6,g4)
    c: Radius(g6) = 1.25
    c: Vertical(g6,g0)
    c: Coincident(g7,g4)
    c: Vertical(g7)
    c: Coincident(g8,g7)
    c: Coincident(g8,g1)
    c: Equal(g8,g6)
    c: Horizontal(g8,g7)
    c: Vertical(g8,g1)
    c: DistanceY(g1,g0) = 2.54
FEATURE [Sketcher::SketchObject] Sketch062
  AttachmentOffset = pos=(0,0,0) rot=(0,0,1;-1.5708rad)
  MapMode = 5
  Placement = pos=(0,0,0) rot=(-0.57735,-0.57735,0.57735;4.18879rad)
  Support = -> [XZ_Plane039]
  expr: Constraints[1] = 2.5 / 2
  sketch-geometry (1):
    g0: Circle CenterX=0 CenterY=0 CenterZ=0 NormalX=0 NormalY=0 NormalZ=1 AngleXU=0 Radius=1.25
  constraints (2):
    c: Coincident(g0,g-1)
    c: Radius(g0) = 1.25
FEATURE [PartDesign::Pad] Pad021
  Length = 6.5
  Length2 = 100
  Midplane = true
  Placement = pos=(0,0,0) rot=(1,0,0;1.5708rad)
  Profile = -> Sketch062
  Type = 0
  expr: Length = 6.5
FEATURE [PartDesign::Body] Body040  label="1/8W_Body014"
  Group = -> [Sketch062,Pad021]
  Origin = -> Origin038
  Tip = -> Pad021
FEATURE [PartDesign::AdditivePipe] AdditivePipe021
  AuxilleryCurvelinear = true
  AuxillerySpineTangent = false
  Binormal = (0,0,0)
  Mode = 0
  Placement = pos=(0,0,0) rot=(1,0,0;1.5708rad)
  Profile = -> Sketch060
  Refine = true
  Spine = -> Sketch059
  SpineTangent = false
  Transformation = 0
  Transition = 0
FEATURE [PartDesign::Body] Body039  label="1/8W_10.16_H002"
  Group = -> [Sketch059,Sketch060,AdditivePipe021]
  Origin = -> Origin046
  Tip = -> AdditivePipe021
FEATURE [Sketcher::SketchObject] Sketch063
  AttachmentOffset = pos=(0,0,0) rot=(0,0,1;-1.5708rad)
  MapMode = 5
  Placement = pos=(0,0,0) rot=(-0.57735,-0.57735,0.57735;4.18879rad)
  Support = -> [XZ_Plane038]
  expr: Constraints[1] = 0.55 / 2
  sketch-geometry (1):
    g0: Circle CenterX=0 CenterY=0 CenterZ=0 NormalX=0 NormalY=0 NormalZ=1 AngleXU=0 Radius=0.275
  constraints (2):
    c: Coincident(g0,g-1)
    c: Radius(g0) = 0.275
FEATURE [Sketcher::SketchObject] Sketch064
  AttachmentOffset = pos=(0,0,0) rot=(0,0,1;-1.5708rad)
  MapMode = 5
  Placement = pos=(0,0,0) rot=(-0.57735,-0.57735,0.57735;4.18879rad)
  Support = -> [XZ_Plane042]
  expr: Constraints[1] = 0.55 / 2
  sketch-geometry (1):
    g0: Circle CenterX=0 CenterY=0 CenterZ=0 NormalX=0 NormalY=0 NormalZ=1 AngleXU=0 Radius=0.275
  constraints (2):
    c: Coincident(g0,g-1)
    c: Radius(g0) = 0.275
FEATURE [Sketcher::SketchObject] Sketch065
  AttachmentOffset = pos=(0,0,0) rot=(0,0,1;-1.5708rad)
  MapMode = 5
  Placement = pos=(0,0,0) rot=(-0.57735,-0.57735,0.57735;4.18879rad)
  Support = -> [XZ_Plane046]
  expr: Constraints[1] = 2.5 / 2
  sketch-geometry (1):
    g0: Circle CenterX=0 CenterY=0 CenterZ=0 NormalX=0 NormalY=0 NormalZ=1 AngleXU=0 Radius=1.25
  constraints (2):
    c: Coincident(g0,g-1)
    c: Radius(g0) = 1.25
FEATURE [PartDesign::Pad] Pad022
  Length = 6.5
  Length2 = 100
  Midplane = true
  Placement = pos=(0,0,0) rot=(1,0,0;1.5708rad)
  Profile = -> Sketch065
  Type = 0
  expr: Length = 6.5
FEATURE [Sketcher::SketchObject] Sketch066
  AttachmentOffset = pos=(0,0,0) rot=(0,0,1;-1.5708rad)
  MapMode = 5
  Placement = pos=(0,0,0) rot=(-0.57735,-0.57735,0.57735;4.18879rad)
  Support = -> [XZ_Plane041]
  expr: Constraints[1] = 0.55 / 2
  sketch-geometry (1):
    g0: Circle CenterX=0 CenterY=0 CenterZ=0 NormalX=0 NormalY=0 NormalZ=1 AngleXU=0 Radius=0.275
  constraints (2):
    c: Coincident(g0,g-1)
    c: Radius(g0) = 0.275
FEATURE [PartDesign::AdditivePipe] AdditivePipe022
  AuxilleryCurvelinear = true
  AuxillerySpineTangent = false
  Binormal = (0,0,0)
  Mode = 0
  Placement = pos=(0,0,0) rot=(1,0,0;1.5708rad)
  Profile = -> Sketch066
  Refine = true
  Spine = -> Sketch061
  SpineTangent = false
  Transformation = 0
  Transition = 0
FEATURE [PartDesign::Body] Body038  label="1/8W_2.54_V002"
  Group = -> [Sketch061,Sketch066,AdditivePipe022]
  Origin = -> Origin045
  Tip = -> AdditivePipe022
FEATURE [Part::MultiFuse] Fusion014  label="R_MF25_P2.54_V"
  Placement = pos=(-1.27,1e-15,1.75) rot=(0.57735,0.57735,-0.57735;4.18879rad)
  Shapes = -> [Body040,Body038]
FEATURE [Sketcher::SketchObject] Sketch067
  MapMode = 5
  Placement = pos=(0,0,0) rot=(0.57735,0.57735,0.57735;2.0944rad)
  Support = -> [YZ_Plane039]
  expr: Constraints[18] = 2.5 / 2
  expr: Constraints[9] = 6.5 / 2
  expr: Constraints[3] = 6.5 / 2
  sketch-geometry (8):
    g0: LineSegment StartX=5.85 StartY=0 StartZ=0 EndX=-3.25 EndY=-5.28144e-11 EndZ=0
    g1: LineSegment StartX=-3.25 StartY=-5.08 StartZ=0 EndX=5.85 EndY=-5.08 EndZ=0
    g2: GeomPoint X=3.25 Y=0 Z=0
    g3: GeomPoint X=3.25 Y=-5.08 Z=0
    g4: GeomPoint X=-3.25 Y=0 Z=0
    g5: LineSegment StartX=-4.5 StartY=-1.25 StartZ=0 EndX=-4.5 EndY=-3.83 EndZ=0
    g6: ArcOfCircle CenterX=-3.25 CenterY=-1.25 CenterZ=0 NormalX=0 NormalY=0 NormalZ=1 AngleXU=0 Radius=1.25 StartAngle=1.5708 EndAngle=3.14159
    g7: ArcOfCircle CenterX=-3.25 CenterY=-3.83 CenterZ=0 NormalX=0 NormalY=0 NormalZ=1 AngleXU=0 Radius=1.25 StartAngle=3.14159 EndAngle=4.71239
  constraints (20):
    c: PointOnObject(g0,g-1)
    c: Horizontal(g1)
    c: PointOnObject(g2,g0)
    c: DistanceX(g-1,g2) = 3.25
    c: DistanceX(g2,g0) = 2.6
    c: PointOnObject(g3,g1)
    c: DistanceX(g3,g1) = 2.6
    c: Vertical(g0,g1)
    c: PointOnObject(g4,g0)
    c: DistanceX(g4,g-1) = 3.25
    c: Vertical(g5)
    c: Tangent(g0,g6) = -1.5708
    c: Tangent(g5,g6) = -1.5708
    c: Tangent(g1,g7) = -1.5708
    c: Tangent(g5,g7) = -1.5708
    c: DistanceY(g1,g0) = 5.08
    c: PointOnObject(g0,g-1)
    c: Equal(g7,g6)
    c: Radius(g6) = 1.25
    c: DistanceX(g0,g4) = 0
FEATURE [PartDesign::AdditivePipe] AdditivePipe025
  AuxilleryCurvelinear = true
  AuxillerySpineTangent = false
  Binormal = (0,0,0)
  Mode = 0
  Placement = pos=(0,0,0) rot=(1,0,0;1.5708rad)
  Profile = -> Sketch063
  Refine = true
  Spine = -> Sketch067
  SpineTangent = false
  Transformation = 0
  Transition = 0
FEATURE [PartDesign::Body] Body044  label="1/8W_5.08_V002"
  Group = -> [Sketch067,Sketch063,AdditivePipe025]
  Origin = -> Origin047
  Tip = -> AdditivePipe025
FEATURE [Sketcher::SketchObject] Sketch068
  MapMode = 5
  Placement = pos=(0,0,0) rot=(0.57735,0.57735,0.57735;2.0944rad)
  Support = -> [YZ_Plane042]
  expr: Constraints[11] = 2.5 / 2
  expr: Constraints[10] = 12.7
  sketch-geometry (5):
    g0: LineSegment StartX=-5.1 StartY=-2e-16 StartZ=0 EndX=5.1 EndY=-7e-16 EndZ=0
    g1: LineSegment StartX=-6.35 StartY=-1.25 StartZ=0 EndX=-6.35 EndY=-3.85 EndZ=0
    g2: LineSegment StartX=6.35 StartY=-1.25 StartZ=0 EndX=6.35 EndY=-3.85 EndZ=0
    g3: ArcOfCircle CenterX=-5.1 CenterY=-1.25 CenterZ=0 NormalX=0 NormalY=0 NormalZ=1 AngleXU=0 Radius=1.25 StartAngle=1.5708 EndAngle=3.14159
    g4: ArcOfCircle CenterX=5.1 CenterY=-1.25 CenterZ=0 NormalX=0 NormalY=0 NormalZ=1 AngleXU=0 Radius=1.25 StartAngle=0 EndAngle=1.5708
  constraints (13):
    c: Vertical(g1)
    c: Vertical(g2)
    c: Equal(g2,g1)
    c: Tangent(g0,g3) = 1.5708
    c: Tangent(g1,g3) = -1.5708
    c: Tangent(g0,g4) = 1.5708
    c: Tangent(g2,g4) = 1.5708
    c: Symmetric(g0,g0,g-2)
    c: Equal(g4,g3)
    c: PointOnObject(g0,g-1)
    c: DistanceX(g1,g2) = 12.7
    c: DistanceY(g1,g0) = 1.25
    c: DistanceY(g1,g1) = 2.6
FEATURE [Sketcher::SketchObject] Sketch069
  MapMode = 5
  Placement = pos=(0,0,0) rot=(0.57735,0.57735,0.57735;2.0944rad)
  Support = -> [YZ_Plane043]
  expr: Constraints[11] = 2.5 / 2
  expr: Constraints[10] = 15.24
  sketch-geometry (5):
    g0: LineSegment StartX=-6.37 StartY=0 StartZ=0 EndX=6.37 EndY=-4e-16 EndZ=0
    g1: LineSegment StartX=-7.62 StartY=-1.25 StartZ=0 EndX=-7.62 EndY=-3.85 EndZ=0
    g2: LineSegment StartX=7.62 StartY=-1.25 StartZ=0 EndX=7.62 EndY=-3.85 EndZ=0
    g3: ArcOfCircle CenterX=-6.37 CenterY=-1.25 CenterZ=0 NormalX=0 NormalY=0 NormalZ=1 AngleXU=0 Radius=1.25 StartAngle=1.5708 EndAngle=3.14159
    g4: ArcOfCircle CenterX=6.37 CenterY=-1.25 CenterZ=0 NormalX=0 NormalY=0 NormalZ=1 AngleXU=0 Radius=1.25 StartAngle=0 EndAngle=1.5708
  constraints (13):
    c: Vertical(g1)
    c: Vertical(g2)
    c: Equal(g2,g1)
    c: Tangent(g0,g3) = 1.5708
    c: Tangent(g1,g3) = -1.5708
    c: Tangent(g0,g4) = 1.5708
    c: Tangent(g2,g4) = 1.5708
    c: Symmetric(g0,g0,g-2)
    c: Equal(g4,g3)
    c: PointOnObject(g0,g-1)
    c: DistanceX(g1,g2) = 15.24
    c: DistanceY(g1,g0) = 1.25
    c: DistanceY(g1,g1) = 2.6
FEATURE [PartDesign::AdditivePipe] AdditivePipe023
  AuxilleryCurvelinear = true
  AuxillerySpineTangent = false
  Binormal = (0,0,0)
  Mode = 0
  Placement = pos=(0,0,0) rot=(1,0,0;1.5708rad)
  Profile = -> Sketch064
  Refine = true
  Spine = -> Sketch069
  SpineTangent = false
  Transformation = 0
  Transition = 0
FEATURE [PartDesign::Body] Body043  label="1/8W_15.24_H002"
  Group = -> [Sketch069,Sketch064,AdditivePipe023]
  Origin = -> Origin051
  Tip = -> AdditivePipe023
FEATURE [Sketcher::SketchObject] Sketch070
  AttachmentOffset = pos=(0,0,0) rot=(0,0,1;-1.5708rad)
  MapMode = 5
  Placement = pos=(0,0,0) rot=(-0.57735,-0.57735,0.57735;4.18879rad)
  Support = -> [XZ_Plane043]
  expr: Constraints[1] = 0.55 / 2
  sketch-geometry (1):
    g0: Circle CenterX=0 CenterY=0 CenterZ=0 NormalX=0 NormalY=0 NormalZ=1 AngleXU=0 Radius=0.275
  constraints (2):
    c: Coincident(g0,g-1)
    c: Radius(g0) = 0.275
FEATURE [PartDesign::AdditivePipe] AdditivePipe024
  AuxilleryCurvelinear = true
  AuxillerySpineTangent = false
  Binormal = (0,0,0)
  Mode = 0
  Placement = pos=(0,0,0) rot=(1,0,0;1.5708rad)
  Profile = -> Sketch070
  Refine = true
  Spine = -> Sketch068
  SpineTangent = false
  Transformation = 0
  Transition = 0
FEATURE [PartDesign::Body] Body042  label="1/8W_12.70_H002"
  Group = -> [Sketch068,Sketch070,AdditivePipe024]
  Origin = -> Origin048
  Tip = -> AdditivePipe024
FEATURE [Sketcher::SketchObject] Sketch071
  AttachmentOffset = pos=(0,0,0) rot=(0,0,1;-1.5708rad)
  MapMode = 5
  Placement = pos=(0,0,0) rot=(-0.57735,-0.57735,0.57735;4.18879rad)
  Support = -> [XZ_Plane048]
  expr: Constraints[1] = 2.5 / 2
  sketch-geometry (1):
    g0: Circle CenterX=0 CenterY=0 CenterZ=0 NormalX=0 NormalY=0 NormalZ=1 AngleXU=0 Radius=1.25
  constraints (2):
    c: Coincident(g0,g-1)
    c: Radius(g0) = 1.25
FEATURE [PartDesign::Pad] Pad019
  Length = 6.5
  Length2 = 100
  Midplane = true
  Placement = pos=(0,0,0) rot=(1,0,0;1.5708rad)
  Profile = -> Sketch071
  Type = 0
  expr: Length = 6.5
FEATURE [Sketcher::SketchObject] Sketch072
  AttachmentOffset = pos=(0,0,0) rot=(0,0,1;-1.5708rad)
  MapMode = 5
  Placement = pos=(0,0,0) rot=(-0.57735,-0.57735,0.57735;4.18879rad)
  Support = -> [XZ_Plane050]
  expr: Constraints[1] = 2.5 / 2
  sketch-geometry (1):
    g0: Circle CenterX=0 CenterY=0 CenterZ=0 NormalX=0 NormalY=0 NormalZ=1 AngleXU=0 Radius=1.25
  constraints (2):
    c: Coincident(g0,g-1)
    c: Radius(g0) = 1.25
FEATURE [PartDesign::Pad] Pad018
  Length = 6.5
  Length2 = 100
  Midplane = true
  Placement = pos=(0,0,0) rot=(1,0,0;1.5708rad)
  Profile = -> Sketch072
  Type = 0
  expr: Length = 6.5
FEATURE [Sketcher::SketchObject] Sketch075
  AttachmentOffset = pos=(0,0,0) rot=(0,0,1;-1.5708rad)
  MapMode = 5
  Placement = pos=(0,0,0) rot=(-0.57735,-0.57735,0.57735;4.18879rad)
  Support = -> [XZ_Plane051]
  expr: Constraints[1] = 2.5 / 2
  sketch-geometry (1):
    g0: Circle CenterX=0 CenterY=0 CenterZ=0 NormalX=0 NormalY=0 NormalZ=1 AngleXU=0 Radius=1.25
  constraints (2):
    c: Coincident(g0,g-1)
    c: Radius(g0) = 1.25
FEATURE [PartDesign::Pad] Pad016
  Length = 6.5
  Length2 = 100
  Midplane = true
  Placement = pos=(0,0,0) rot=(1,0,0;1.5708rad)
  Profile = -> Sketch075
  Type = 0
  expr: Length = 6.5
FEATURE [Sketcher::SketchObject] Sketch076
  AttachmentOffset = pos=(0,0,0) rot=(0,0,1;-1.5708rad)
  MapMode = 5
  Placement = pos=(0,0,0) rot=(-0.57735,-0.57735,0.57735;4.18879rad)
  Support = -> [XZ_Plane049]
  expr: Constraints[1] = 2.5 / 2
  sketch-geometry (1):
    g0: Circle CenterX=0 CenterY=0 CenterZ=0 NormalX=0 NormalY=0 NormalZ=1 AngleXU=0 Radius=1.25
  constraints (2):
    c: Coincident(g0,g-1)
    c: Radius(g0) = 1.25
FEATURE [PartDesign::Pad] Pad017
  Length = 6.5
  Length2 = 100
  Midplane = true
  Placement = pos=(0,0,0) rot=(1,0,0;1.5708rad)
  Profile = -> Sketch076
  Type = 0
  expr: Length = 6.5
FEATURE [PartDesign::Body] Body041  label="1/8W_Body015"
  Group = -> [Sketch076,Pad017]
  Origin = -> Origin044
  Tip = -> Pad017
FEATURE [Sketcher::SketchObject] Sketch077
  AttachmentOffset = pos=(0,0,0) rot=(0,0,1;-1.5708rad)
  MapMode = 5
  Placement = pos=(0,0,0) rot=(-0.57735,-0.57735,0.57735;4.18879rad)
  Support = -> [XZ_Plane045]
  expr: Constraints[1] = 0.55 / 2
  sketch-geometry (1):
    g0: Circle CenterX=0 CenterY=0 CenterZ=0 NormalX=0 NormalY=0 NormalZ=1 AngleXU=0 Radius=0.275
  constraints (2):
    c: Coincident(g0,g-1)
    c: Radius(g0) = 0.275
FEATURE [Sketcher::SketchObject] Sketch079
  MapMode = 5
  Placement = pos=(0,0,0) rot=(0.57735,0.57735,0.57735;2.0944rad)
  Support = -> [YZ_Plane047]
  expr: Constraints[11] = 2.5 / 2
  expr: Constraints[10] = 3 * 2.54
  sketch-geometry (5):
    g0: LineSegment StartX=-2.56 StartY=-9e-16 StartZ=0 EndX=2.56 EndY=-2.4e-15 EndZ=0
    g1: LineSegment StartX=-3.81 StartY=-1.25 StartZ=0 EndX=-3.81 EndY=-3.85 EndZ=0
    g2: LineSegment StartX=3.81 StartY=-1.25 StartZ=0 EndX=3.81 EndY=-3.85 EndZ=0
    g3: ArcOfCircle CenterX=-2.56 CenterY=-1.25 CenterZ=0 NormalX=0 NormalY=0 NormalZ=1 AngleXU=0 Radius=1.25 StartAngle=1.5708 EndAngle=3.14159
    g4: ArcOfCircle CenterX=2.56 CenterY=-1.25 CenterZ=0 NormalX=0 NormalY=0 NormalZ=1 AngleXU=0 Radius=1.25 StartAngle=0 EndAngle=1.5708
  constraints (13):
    c: Vertical(g1)
    c: Vertical(g2)
    c: Equal(g2,g1)
    c: Tangent(g0,g3) = 1.5708
    c: Tangent(g1,g3) = -1.5708
    c: Tangent(g0,g4) = 1.5708
    c: Tangent(g2,g4) = 1.5708
    c: Symmetric(g0,g0,g-2)
    c: Equal(g4,g3)
    c: PointOnObject(g0,g-1)
    c: DistanceX(g1,g2) = 7.62
    c: DistanceY(g1,g0) = 1.25
    c: DistanceY(g1,g1) = 2.6
FEATURE [PartDesign::AdditivePipe] AdditivePipe026
  AuxilleryCurvelinear = true
  AuxillerySpineTangent = false
  Binormal = (0,0,0)
  Mode = 0
  Placement = pos=(0,0,0) rot=(1,0,0;1.5708rad)
  Profile = -> Sketch077
  Refine = true
  Spine = -> Sketch079
  SpineTangent = false
  Transformation = 0
  Transition = 0
FEATURE [PartDesign::Body] Body045  label="1/8W_Body016"
  Group = -> [Sketch072,Pad018]
  Origin = -> Origin039
  Tip = -> Pad018
FEATURE [PartDesign::Body] Body047  label="1/8W_Body017"
  Group = -> [Sketch071,Pad019]
  Origin = -> Origin042
  Tip = -> Pad019
FEATURE [PartDesign::Body] Body048  label="1/8W_Body018"
  Group = -> [Sketch065,Pad022]
  Origin = -> Origin041
  Tip = -> Pad022
FEATURE [Part::MultiFuse] Fusion017  label="R_MF25_P5.08_V"
  Placement = pos=(-2.54,0,1.75) rot=(0.57735,0.57735,-0.57735;4.18879rad)
  Shapes = -> [Body048,Body044]
FEATURE [PartDesign::Body] Body050  label="1/8W_7.62_H002"
  Group = -> [Sketch079,Sketch077,AdditivePipe026]
  Origin = -> Origin050
  Tip = -> AdditivePipe026
FEATURE [Part::MultiFuse] Fusion016  label="R_MF25_P7.62_H"
  Placement = pos=(0,0,1) rot=(0,0,-1;1.5708rad)
  Shapes = -> [Body047,Body050]
FEATURE [PartDesign::Body] Body051  label="1/8W_Body020"
  Group = -> [Sketch075,Pad016]
  Origin = -> Origin040
  Tip = -> Pad016
FEATURE [Part::MultiFuse] Fusion018  label="R_MF25_P15.24_H"
  Placement = pos=(0,0,1) rot=(0,0,-1;1.5708rad)
  Shapes = -> [Body051,Body043]
FEATURE [Part::MultiFuse] Fusion019  label="R_MF25_P12.70_H"
  Placement = pos=(0,0,1) rot=(0,0,1;1.5708rad)
  Shapes = -> [Body045,Body042]
FEATURE [Part::MultiFuse] Fusion020  label="R_MF25_P10.16_H"
  Placement = pos=(0,0,1) rot=(0,0,-1;1.5708rad)
  Shapes = -> [Body041,Body039]
FEATURE [App::DocumentObjectGroup] Group003  label="1/4W_MF"
  Group = -> [Fusion014,Fusion017,Fusion016,Fusion020,Fusion019,Fusion018]
FEATURE [Sketcher::SketchObject] Sketch080
  MapMode = 5
  Placement = pos=(0,0,0) rot=(0.57735,0.57735,0.57735;2.0944rad)
  Support = -> [YZ_Plane055]
  expr: Constraints[11] = 2.5 / 2
  expr: Constraints[10] = 3 * 2.54
  sketch-geometry (5):
    g0: LineSegment StartX=-2.56 StartY=-9e-16 StartZ=0 EndX=2.56 EndY=-2.4e-15 EndZ=0
    g1: LineSegment StartX=-3.81 StartY=-1.25 StartZ=0 EndX=-3.81 EndY=-3.85 EndZ=0
    g2: LineSegment StartX=3.81 StartY=-1.25 StartZ=0 EndX=3.81 EndY=-3.85 EndZ=0
    g3: ArcOfCircle CenterX=-2.56 CenterY=-1.25 CenterZ=0 NormalX=0 NormalY=0 NormalZ=1 AngleXU=0 Radius=1.25 StartAngle=1.5708 EndAngle=3.14159
    g4: ArcOfCircle CenterX=2.56 CenterY=-1.25 CenterZ=0 NormalX=0 NormalY=0 NormalZ=1 AngleXU=0 Radius=1.25 StartAngle=0 EndAngle=1.5708
  constraints (13):
    c: Vertical(g1)
    c: Vertical(g2)
    c: Equal(g2,g1)
    c: Tangent(g0,g3) = 1.5708
    c: Tangent(g1,g3) = -1.5708
    c: Tangent(g0,g4) = 1.5708
    c: Tangent(g2,g4) = 1.5708
    c: Symmetric(g0,g0,g-2)
    c: Equal(g4,g3)
    c: PointOnObject(g0,g-1)
    c: DistanceX(g1,g2) = 7.62
    c: DistanceY(g1,g0) = 1.25
    c: DistanceY(g1,g1) = 2.6
FEATURE [Sketcher::SketchObject] Sketch081
  MapMode = 5
  Placement = pos=(0,0,0) rot=(0.57735,0.57735,0.57735;2.0944rad)
  Support = -> [YZ_Plane054]
  expr: Constraints[24] = 2.54
  expr: Constraints[15] = 2.5 / 2
  expr: Constraints[10] = 6.5 / 2
  expr: Constraints[4] = 6.5 / 2
  sketch-geometry (9):
    g0: LineSegment StartX=5.85 StartY=0 StartZ=0 EndX=-3.25 EndY=0 EndZ=0
    g1: LineSegment StartX=-3.25 StartY=-2.54 StartZ=0 EndX=5.85 EndY=-2.54 EndZ=0
    g2: GeomPoint X=3.25 Y=0 Z=0
    g3: GeomPoint X=3.25 Y=-2.54 Z=0
    g4: GeomPoint X=-4.5 Y=-1.25 Z=0
    g5: GeomPoint X=-3.25 Y=0 Z=0
    g6: ArcOfCircle CenterX=-3.25 CenterY=-1.25 CenterZ=0 NormalX=0 NormalY=0 NormalZ=1 AngleXU=0 Radius=1.25 StartAngle=1.5708 EndAngle=3.14159
    g7: LineSegment StartX=-4.5 StartY=-1.25 StartZ=0 EndX=-4.5 EndY=-1.29 EndZ=0
    g8: ArcOfCircle CenterX=-3.25 CenterY=-1.29 CenterZ=0 NormalX=0 NormalY=0 NormalZ=1 AngleXU=0 Radius=1.25 StartAngle=3.14159 EndAngle=4.71239
  constraints (25):
    c: PointOnObject(g0,g-1)
    c: PointOnObject(g0,g-1)
    c: Horizontal(g1)
    c: PointOnObject(g2,g0)
    c: DistanceX(g-1,g2) = 3.25
    c: DistanceX(g2,g0) = 2.6
    c: PointOnObject(g3,g1)
    c: DistanceX(g3,g1) = 2.6
    c: Vertical(g0,g1)
    c: PointOnObject(g5,g0)
    c: DistanceX(g5,g-1) = 3.25
    c: DistanceX(g0,g5) = 0
    c: Coincident(g6,g0)
    c: Coincident(g6,g4)
    c: Horizontal(g6,g4)
    c: Radius(g6) = 1.25
    c: Vertical(g6,g0)
    c: Coincident(g7,g4)
    c: Vertical(g7)
    c: Coincident(g8,g7)
    c: Coincident(g8,g1)
    c: Equal(g8,g6)
    c: Horizontal(g8,g7)
    c: Vertical(g8,g1)
    c: DistanceY(g1,g0) = 2.54
FEATURE [Sketcher::SketchObject] Sketch082
  AttachmentOffset = pos=(0,0,0) rot=(0,0,1;-1.5708rad)
  MapMode = 5
  Placement = pos=(0,0,0) rot=(-0.57735,-0.57735,0.57735;4.18879rad)
  Support = -> [XZ_Plane056]
  expr: Constraints[1] = 0.55 / 2
  sketch-geometry (1):
    g0: Circle CenterX=0 CenterY=0 CenterZ=0 NormalX=0 NormalY=0 NormalZ=1 AngleXU=0 Radius=0.275
  constraints (2):
    c: Coincident(g0,g-1)
    c: Radius(g0) = 0.275
FEATURE [PartDesign::AdditivePipe] AdditivePipe027
  AuxilleryCurvelinear = true
  AuxillerySpineTangent = false
  Binormal = (0,0,0)
  Mode = 0
  Placement = pos=(0,0,0) rot=(1,0,0;1.5708rad)
  Profile = -> Sketch082
  Refine = true
  Spine = -> Sketch081
  SpineTangent = false
  Transformation = 0
  Transition = 0
FEATURE [Sketcher::SketchObject] Sketch083
  MapMode = 5
  Placement = pos=(0,0,0) rot=(0.57735,0.57735,0.57735;2.0944rad)
  Support = -> [YZ_Plane059]
  expr: Constraints[11] = 2.5 / 2
  expr: Constraints[10] = 15.24
  sketch-geometry (5):
    g0: LineSegment StartX=-6.37 StartY=0 StartZ=0 EndX=6.37 EndY=-4e-16 EndZ=0
    g1: LineSegment StartX=-7.62 StartY=-1.25 StartZ=0 EndX=-7.62 EndY=-3.85 EndZ=0
    g2: LineSegment StartX=7.62 StartY=-1.25 StartZ=0 EndX=7.62 EndY=-3.85 EndZ=0
    g3: ArcOfCircle CenterX=-6.37 CenterY=-1.25 CenterZ=0 NormalX=0 NormalY=0 NormalZ=1 AngleXU=0 Radius=1.25 StartAngle=1.5708 EndAngle=3.14159
    g4: ArcOfCircle CenterX=6.37 CenterY=-1.25 CenterZ=0 NormalX=0 NormalY=0 NormalZ=1 AngleXU=0 Radius=1.25 StartAngle=0 EndAngle=1.5708
  constraints (13):
    c: Vertical(g1)
    c: Vertical(g2)
    c: Equal(g2,g1)
    c: Tangent(g0,g3) = 1.5708
    c: Tangent(g1,g3) = -1.5708
    c: Tangent(g0,g4) = 1.5708
    c: Tangent(g2,g4) = 1.5708
    c: Symmetric(g0,g0,g-2)
    c: Equal(g4,g3)
    c: PointOnObject(g0,g-1)
    c: DistanceX(g1,g2) = 15.24
    c: DistanceY(g1,g0) = 1.25
    c: DistanceY(g1,g1) = 2.6
FEATURE [Sketcher::SketchObject] Sketch084
  MapMode = 5
  Placement = pos=(0,0,0) rot=(0.57735,0.57735,0.57735;2.0944rad)
  Support = -> [YZ_Plane057]
  expr: Constraints[11] = 2.5 / 2
  expr: Constraints[10] = 12.7
  sketch-geometry (5):
    g0: LineSegment StartX=-5.1 StartY=-2e-16 StartZ=0 EndX=5.1 EndY=-7e-16 EndZ=0
    g1: LineSegment StartX=-6.35 StartY=-1.25 StartZ=0 EndX=-6.35 EndY=-3.85 EndZ=0
    g2: LineSegment StartX=6.35 StartY=-1.25 StartZ=0 EndX=6.35 EndY=-3.85 EndZ=0
    g3: ArcOfCircle CenterX=-5.1 CenterY=-1.25 CenterZ=0 NormalX=0 NormalY=0 NormalZ=1 AngleXU=0 Radius=1.25 StartAngle=1.5708 EndAngle=3.14159
    g4: ArcOfCircle CenterX=5.1 CenterY=-1.25 CenterZ=0 NormalX=0 NormalY=0 NormalZ=1 AngleXU=0 Radius=1.25 StartAngle=0 EndAngle=1.5708
  constraints (13):
    c: Vertical(g1)
    c: Vertical(g2)
    c: Equal(g2,g1)
    c: Tangent(g0,g3) = 1.5708
    c: Tangent(g1,g3) = -1.5708
    c: Tangent(g0,g4) = 1.5708
    c: Tangent(g2,g4) = 1.5708
    c: Symmetric(g0,g0,g-2)
    c: Equal(g4,g3)
    c: PointOnObject(g0,g-1)
    c: DistanceX(g1,g2) = 12.7
    c: DistanceY(g1,g0) = 1.25
    c: DistanceY(g1,g1) = 2.6
FEATURE [Sketcher::SketchObject] Sketch085
  AttachmentOffset = pos=(0,0,0) rot=(0,0,1;-1.5708rad)
  MapMode = 5
  Placement = pos=(0,0,0) rot=(-0.57735,-0.57735,0.57735;4.18879rad)
  Support = -> [XZ_Plane053]
  expr: Constraints[1] = 0.55 / 2
  sketch-geometry (1):
    g0: Circle CenterX=0 CenterY=0 CenterZ=0 NormalX=0 NormalY=0 NormalZ=1 AngleXU=0 Radius=0.275
  constraints (2):
    c: Coincident(g0,g-1)
    c: Radius(g0) = 0.275
FEATURE [Sketcher::SketchObject] Sketch086
  AttachmentOffset = pos=(0,0,0) rot=(0,0,1;-1.5708rad)
  MapMode = 5
  Placement = pos=(0,0,0) rot=(-0.57735,-0.57735,0.57735;4.18879rad)
  Support = -> [XZ_Plane052]
  expr: Constraints[1] = 2.5 / 2
  sketch-geometry (1):
    g0: Circle CenterX=0 CenterY=0 CenterZ=0 NormalX=0 NormalY=0 NormalZ=1 AngleXU=0 Radius=1.25
  constraints (2):
    c: Coincident(g0,g-1)
    c: Radius(g0) = 1.25
FEATURE [PartDesign::Pad] Pad027
  Length = 6.5
  Length2 = 100
  Midplane = true
  Placement = pos=(0,0,0) rot=(1,0,0;1.5708rad)
  Profile = -> Sketch086
  Type = 0
  expr: Length = 6.5
FEATURE [Sketcher::SketchObject] Sketch087
  AttachmentOffset = pos=(0,0,0) rot=(0,0,1;-1.5708rad)
  MapMode = 5
  Placement = pos=(0,0,0) rot=(-0.57735,-0.57735,0.57735;4.18879rad)
  Support = -> [XZ_Plane059]
  expr: Constraints[1] = 0.55 / 2
  sketch-geometry (1):
    g0: Circle CenterX=0 CenterY=0 CenterZ=0 NormalX=0 NormalY=0 NormalZ=1 AngleXU=0 Radius=0.275
  constraints (2):
    c: Coincident(g0,g-1)
    c: Radius(g0) = 0.275
FEATURE [Sketcher::SketchObject] Sketch088
  MapMode = 5
  Placement = pos=(0,0,0) rot=(0.57735,0.57735,0.57735;2.0944rad)
  Support = -> [YZ_Plane060]
  expr: Constraints[11] = 2.5 / 2
  expr: Constraints[10] = 4 * 2.54
  sketch-geometry (5):
    g0: LineSegment StartX=-3.83 StartY=0 StartZ=0 EndX=3.83 EndY=-1.3e-15 EndZ=0
    g1: LineSegment StartX=-5.08 StartY=-1.25 StartZ=0 EndX=-5.08 EndY=-3.85 EndZ=0
    g2: LineSegment StartX=5.08 StartY=-1.25 StartZ=0 EndX=5.08 EndY=-3.85 EndZ=0
    g3: ArcOfCircle CenterX=-3.83 CenterY=-1.25 CenterZ=0 NormalX=0 NormalY=0 NormalZ=1 AngleXU=0 Radius=1.25 StartAngle=1.5708 EndAngle=3.14159
    g4: ArcOfCircle CenterX=3.83 CenterY=-1.25 CenterZ=0 NormalX=0 NormalY=0 NormalZ=1 AngleXU=0 Radius=1.25 StartAngle=0 EndAngle=1.5708
  constraints (13):
    c: Vertical(g1)
    c: Vertical(g2)
    c: Equal(g2,g1)
    c: Tangent(g0,g3) = 1.5708
    c: Tangent(g1,g3) = -1.5708
    c: Tangent(g0,g4) = 1.5708
    c: Tangent(g2,g4) = 1.5708
    c: Symmetric(g0,g0,g-2)
    c: Equal(g4,g3)
    c: PointOnObject(g0,g-1)
    c: DistanceX(g1,g2) = 10.16
    c: DistanceY(g1,g0) = 1.25
    c: DistanceY(g1,g1) = 2.6
FEATURE [PartDesign::AdditivePipe] AdditivePipe030
  AuxilleryCurvelinear = true
  AuxillerySpineTangent = false
  Binormal = (0,0,0)
  Mode = 0
  Placement = pos=(0,0,0) rot=(1,0,0;1.5708rad)
  Profile = -> Sketch087
  Refine = true
  Spine = -> Sketch088
  SpineTangent = false
  Transformation = 0
  Transition = 0
FEATURE [Sketcher::SketchObject] Sketch089
  AttachmentOffset = pos=(0,0,0) rot=(0,0,1;-1.5708rad)
  MapMode = 5
  Placement = pos=(0,0,0) rot=(-0.57735,-0.57735,0.57735;4.18879rad)
  Support = -> [XZ_Plane061]
  expr: Constraints[1] = 2.5 / 2
  sketch-geometry (1):
    g0: Circle CenterX=0 CenterY=0 CenterZ=0 NormalX=0 NormalY=0 NormalZ=1 AngleXU=0 Radius=1.25
  constraints (2):
    c: Coincident(g0,g-1)
    c: Radius(g0) = 1.25
FEATURE [PartDesign::Pad] Pad023
  Length = 6.5
  Length2 = 100
  Midplane = true
  Placement = pos=(0,0,0) rot=(1,0,0;1.5708rad)
  Profile = -> Sketch089
  Type = 0
  expr: Length = 6.5
FEATURE [Sketcher::SketchObject] Sketch090
  AttachmentOffset = pos=(0,0,0) rot=(0,0,1;-1.5708rad)
  MapMode = 5
  Placement = pos=(0,0,0) rot=(-0.57735,-0.57735,0.57735;4.18879rad)
  Support = -> [XZ_Plane057]
  expr: Constraints[1] = 0.55 / 2
  sketch-geometry (1):
    g0: Circle CenterX=0 CenterY=0 CenterZ=0 NormalX=0 NormalY=0 NormalZ=1 AngleXU=0 Radius=0.275
  constraints (2):
    c: Coincident(g0,g-1)
    c: Radius(g0) = 0.275
FEATURE [PartDesign::AdditivePipe] AdditivePipe031
  AuxilleryCurvelinear = true
  AuxillerySpineTangent = false
  Binormal = (0,0,0)
  Mode = 0
  Placement = pos=(0,0,0) rot=(1,0,0;1.5708rad)
  Profile = -> Sketch090
  Refine = true
  Spine = -> Sketch083
  SpineTangent = false
  Transformation = 0
  Transition = 0
FEATURE [PartDesign::Body] Body054  label="1/8W_15.24_H003"
  Group = -> [Sketch083,Sketch090,AdditivePipe031]
  Origin = -> Origin063
  Tip = -> AdditivePipe031
FEATURE [Sketcher::SketchObject] Sketch091
  MapMode = 5
  Placement = pos=(0,0,0) rot=(0.57735,0.57735,0.57735;2.0944rad)
  Support = -> [YZ_Plane053]
  expr: Constraints[18] = 2.5 / 2
  expr: Constraints[9] = 6.5 / 2
  expr: Constraints[3] = 6.5 / 2
  sketch-geometry (8):
    g0: LineSegment StartX=5.85 StartY=0 StartZ=0 EndX=-3.25 EndY=0 EndZ=0
    g1: LineSegment StartX=-3.25 StartY=-5.08 StartZ=0 EndX=5.85 EndY=-5.08 EndZ=0
    g2: GeomPoint X=3.25 Y=0 Z=0
    g3: GeomPoint X=3.25 Y=-5.08 Z=0
    g4: GeomPoint X=-3.25 Y=0 Z=0
    g5: LineSegment StartX=-4.5 StartY=-1.25 StartZ=0 EndX=-4.5 EndY=-3.83 EndZ=0
    g6: ArcOfCircle CenterX=-3.25 CenterY=-1.25 CenterZ=0 NormalX=0 NormalY=0 NormalZ=1 AngleXU=0 Radius=1.25 StartAngle=1.5708 EndAngle=3.14159
    g7: ArcOfCircle CenterX=-3.25 CenterY=-3.83 CenterZ=0 NormalX=0 NormalY=0 NormalZ=1 AngleXU=0 Radius=1.25 StartAngle=3.14159 EndAngle=4.71239
  constraints (20):
    c: PointOnObject(g0,g-1)
    c: Horizontal(g1)
    c: PointOnObject(g2,g0)
    c: DistanceX(g-1,g2) = 3.25
    c: DistanceX(g2,g0) = 2.6
    c: PointOnObject(g3,g1)
    c: DistanceX(g3,g1) = 2.6
    c: Vertical(g0,g1)
    c: PointOnObject(g4,g0)
    c: DistanceX(g4,g-1) = 3.25
    c: Vertical(g5)
    c: Tangent(g0,g6) = -1.5708
    c: Tangent(g5,g6) = -1.5708
    c: Tangent(g1,g7) = -1.5708
    c: Tangent(g5,g7) = -1.5708
    c: DistanceY(g1,g0) = 5.08
    c: PointOnObject(g0,g-1)
    c: Equal(g7,g6)
    c: Radius(g6) = 1.25
    c: DistanceX(g0,g4) = 0
FEATURE [PartDesign::AdditivePipe] AdditivePipe032
  AuxilleryCurvelinear = true
  AuxillerySpineTangent = false
  Binormal = (0,0,0)
  Mode = 0
  Placement = pos=(0,0,0) rot=(1,0,0;1.5708rad)
  Profile = -> Sketch085
  Refine = true
  Spine = -> Sketch091
  SpineTangent = false
  Transformation = 0
  Transition = 0
FEATURE [PartDesign::Body] Body052  label="1/8W_5.08_V003"
  Group = -> [Sketch091,Sketch085,AdditivePipe032]
  Origin = -> Origin058
  Tip = -> AdditivePipe032
FEATURE [Sketcher::SketchObject] Sketch092
  AttachmentOffset = pos=(0,0,0) rot=(0,0,1;-1.5708rad)
  MapMode = 5
  Placement = pos=(0,0,0) rot=(-0.57735,-0.57735,0.57735;4.18879rad)
  Support = -> [XZ_Plane055]
  expr: Constraints[1] = 2.5 / 2
  sketch-geometry (1):
    g0: Circle CenterX=0 CenterY=0 CenterZ=0 NormalX=0 NormalY=0 NormalZ=1 AngleXU=0 Radius=1.25
  constraints (2):
    c: Coincident(g0,g-1)
    c: Radius(g0) = 1.25
FEATURE [PartDesign::Pad] Pad028
  Length = 6.5
  Length2 = 100
  Midplane = true
  Placement = pos=(0,0,0) rot=(1,0,0;1.5708rad)
  Profile = -> Sketch092
  Type = 0
  expr: Length = 6.5
FEATURE [Sketcher::SketchObject] Sketch093
  AttachmentOffset = pos=(0,0,0) rot=(0,0,1;-1.5708rad)
  MapMode = 5
  Placement = pos=(0,0,0) rot=(-0.57735,-0.57735,0.57735;4.18879rad)
  Support = -> [XZ_Plane063]
  expr: Constraints[1] = 2.5 / 2
  sketch-geometry (1):
    g0: Circle CenterX=0 CenterY=0 CenterZ=0 NormalX=0 NormalY=0 NormalZ=1 AngleXU=0 Radius=1.25
  constraints (2):
    c: Coincident(g0,g-1)
    c: Radius(g0) = 1.25
FEATURE [PartDesign::Pad] Pad025
  Length = 6.5
  Length2 = 100
  Midplane = true
  Placement = pos=(0,0,0) rot=(1,0,0;1.5708rad)
  Profile = -> Sketch093
  Type = 0
  expr: Length = 6.5
FEATURE [Sketcher::SketchObject] Sketch094
  AttachmentOffset = pos=(0,0,0) rot=(0,0,1;-1.5708rad)
  MapMode = 5
  Placement = pos=(0,0,0) rot=(-0.57735,-0.57735,0.57735;4.18879rad)
  Support = -> [XZ_Plane060]
  expr: Constraints[1] = 0.55 / 2
  sketch-geometry (1):
    g0: Circle CenterX=0 CenterY=0 CenterZ=0 NormalX=0 NormalY=0 NormalZ=1 AngleXU=0 Radius=0.275
  constraints (2):
    c: Coincident(g0,g-1)
    c: Radius(g0) = 0.275
FEATURE [PartDesign::AdditivePipe] AdditivePipe029
  AuxilleryCurvelinear = true
  AuxillerySpineTangent = false
  Binormal = (0,0,0)
  Mode = 0
  Placement = pos=(0,0,0) rot=(1,0,0;1.5708rad)
  Profile = -> Sketch094
  Refine = true
  Spine = -> Sketch080
  SpineTangent = false
  Transformation = 0
  Transition = 0
FEATURE [Sketcher::SketchObject] Sketch095
  AttachmentOffset = pos=(0,0,0) rot=(0,0,1;-1.5708rad)
  MapMode = 5
  Placement = pos=(0,0,0) rot=(-0.57735,-0.57735,0.57735;4.18879rad)
  Support = -> [XZ_Plane062]
  expr: Constraints[1] = 2.5 / 2
  sketch-geometry (1):
    g0: Circle CenterX=0 CenterY=0 CenterZ=0 NormalX=0 NormalY=0 NormalZ=1 AngleXU=0 Radius=1.25
  constraints (2):
    c: Coincident(g0,g-1)
    c: Radius(g0) = 1.25
FEATURE [PartDesign::Pad] Pad024
  Length = 6.5
  Length2 = 100
  Midplane = true
  Placement = pos=(0,0,0) rot=(1,0,0;1.5708rad)
  Profile = -> Sketch095
  Type = 0
  expr: Length = 6.5
FEATURE [Sketcher::SketchObject] Sketch096
  AttachmentOffset = pos=(0,0,0) rot=(0,0,1;-1.5708rad)
  MapMode = 5
  Placement = pos=(0,0,0) rot=(-0.57735,-0.57735,0.57735;4.18879rad)
  Support = -> [XZ_Plane054]
  expr: Constraints[1] = 0.55 / 2
  sketch-geometry (1):
    g0: Circle CenterX=0 CenterY=0 CenterZ=0 NormalX=0 NormalY=0 NormalZ=1 AngleXU=0 Radius=0.275
  constraints (2):
    c: Coincident(g0,g-1)
    c: Radius(g0) = 0.275
FEATURE [PartDesign::AdditivePipe] AdditivePipe028
  AuxilleryCurvelinear = true
  AuxillerySpineTangent = false
  Binormal = (0,0,0)
  Mode = 0
  Placement = pos=(0,0,0) rot=(1,0,0;1.5708rad)
  Profile = -> Sketch096
  Refine = true
  Spine = -> Sketch084
  SpineTangent = false
  Transformation = 0
  Transition = 0
FEATURE [PartDesign::Body] Body053  label="1/8W_12.70_H003"
  Group = -> [Sketch084,Sketch096,AdditivePipe028]
  Origin = -> Origin059
  Tip = -> AdditivePipe028
FEATURE [Sketcher::SketchObject] Sketch097
  AttachmentOffset = pos=(0,0,0) rot=(0,0,1;-1.5708rad)
  MapMode = 5
  Placement = pos=(0,0,0) rot=(-0.57735,-0.57735,0.57735;4.18879rad)
  Support = -> [XZ_Plane058]
  expr: Constraints[1] = 2.5 / 2
  sketch-geometry (1):
    g0: Circle CenterX=0 CenterY=0 CenterZ=0 NormalX=0 NormalY=0 NormalZ=1 AngleXU=0 Radius=1.25
  constraints (2):
    c: Coincident(g0,g-1)
    c: Radius(g0) = 1.25
FEATURE [PartDesign::Pad] Pad026
  Length = 6.5
  Length2 = 100
  Midplane = true
  Placement = pos=(0,0,0) rot=(1,0,0;1.5708rad)
  Profile = -> Sketch097
  Type = 0
  expr: Length = 6.5
FEATURE [PartDesign::Body] Body055  label="1/8W_Body021"
  Group = -> [Sketch093,Pad025]
  Origin = -> Origin053
  Tip = -> Pad025
FEATURE [Part::MultiFuse] Fusion022  label="R_CF25_P12.70_H"
  Placement = pos=(0,0,1) rot=(0,0,1;1.5708rad)
  Shapes = -> [Body055,Body053]
FEATURE [PartDesign::Body] Body056  label="1/8W_7.62_H003"
  Group = -> [Sketch080,Sketch094,AdditivePipe029]
  Origin = -> Origin062
  Tip = -> AdditivePipe029
FEATURE [PartDesign::Body] Body057  label="1/8W_Body022"
  Group = -> [Sketch095,Pad024]
  Origin = -> Origin056
  Tip = -> Pad024
FEATURE [Part::MultiFuse] Fusion023  label="R_CF25_P15.24_H"
  Placement = pos=(0,0,1) rot=(0,0,-1;1.5708rad)
  Shapes = -> [Body057,Body054]
FEATURE [PartDesign::Body] Body058  label="1/8W_Body023"
  Group = -> [Sketch092,Pad028]
  Origin = -> Origin055
  Tip = -> Pad028
FEATURE [PartDesign::Body] Body059  label="1/8W_Body024"
  Group = -> [Sketch089,Pad023]
  Origin = -> Origin052
  Tip = -> Pad023
FEATURE [Part::MultiFuse] Fusion025  label="R_CF25_P5.08_V"
  Placement = pos=(-2.54,0,1.75) rot=(0.57735,0.57735,-0.57735;4.18879rad)
  Shapes = -> [Body059,Body052]
FEATURE [Part::MultiFuse] Fusion026  label="R_CF25_P7.62_H"
  Placement = pos=(0,0,1) rot=(0,0,-1;1.5708rad)
  Shapes = -> [Body058,Body056]
FEATURE [PartDesign::Body] Body060  label="1/8W_2.54_V003"
  Group = -> [Sketch081,Sketch082,AdditivePipe027]
  Origin = -> Origin057
  Tip = -> AdditivePipe027
FEATURE [PartDesign::Body] Body061  label="1/8W_10.16_H003"
  Group = -> [Sketch088,Sketch087,AdditivePipe030]
  Origin = -> Origin060
  Tip = -> AdditivePipe030
FEATURE [PartDesign::Body] Body062  label="1/8W_Body025"
  Group = -> [Sketch086,Pad027]
  Origin = -> Origin054
  Tip = -> Pad027
FEATURE [Part::MultiFuse] Fusion024  label="R_CF25_P2.54_V"
  Placement = pos=(-1.27,1e-15,1.75) rot=(0.57735,0.57735,-0.57735;4.18879rad)
  Shapes = -> [Body062,Body060]
FEATURE [PartDesign::Body] Body063  label="1/8W_Body026"
  Group = -> [Sketch097,Pad026]
  Origin = -> Origin061
  Tip = -> Pad026
FEATURE [Part::MultiFuse] Fusion021  label="R_CF25_P10.16_H"
  Placement = pos=(0,0,1) rot=(0,0,-1;1.5708rad)
  Shapes = -> [Body063,Body061]
FEATURE [App::DocumentObjectGroup] Group004  label="1/4W_CF"
  Group = -> [Fusion024,Fusion025,Fusion026,Fusion021,Fusion022,Fusion023]
FEATURE [Sketcher::SketchObject] Sketch101
  MapMode = 5
  Placement = pos=(0,0,0) rot=(0.57735,0.57735,0.57735;2.0944rad)
  Support = -> [YZ_Plane071]
  expr: Constraints[11] = 3.5 / 2
  expr: Constraints[10] = 15.24
  sketch-geometry (5):
    g0: LineSegment StartX=-5.87 StartY=-5.4e-14 StartZ=0 EndX=5.87 EndY=-6.51e-14 EndZ=0
    g1: LineSegment StartX=-7.62 StartY=-1.75 StartZ=0 EndX=-7.62 EndY=-4.35 EndZ=0
    g2: LineSegment StartX=7.62 StartY=-1.75 StartZ=0 EndX=7.62 EndY=-4.35 EndZ=0
    g3: ArcOfCircle CenterX=-5.87 CenterY=-1.75 CenterZ=0 NormalX=0 NormalY=0 NormalZ=1 AngleXU=0 Radius=1.75 StartAngle=1.5708 EndAngle=3.14159
    g4: ArcOfCircle CenterX=5.87 CenterY=-1.75 CenterZ=0 NormalX=0 NormalY=0 NormalZ=1 AngleXU=0 Radius=1.75 StartAngle=-6.93e-14 EndAngle=1.5708
  constraints (13):
    c: Vertical(g1)
    c: Vertical(g2)
    c: Equal(g2,g1)
    c: Tangent(g0,g3) = 1.5708
    c: Tangent(g1,g3) = -1.5708
    c: Tangent(g0,g4) = 1.5708
    c: Tangent(g2,g4) = 1.5708
    c: Symmetric(g0,g0,g-2)
    c: Equal(g4,g3)
    c: PointOnObject(g0,g-1)
    c: DistanceX(g1,g2) = 15.24
    c: DistanceY(g1,g0) = 1.75
    c: DistanceY(g1,g1) = 2.6
FEATURE [Sketcher::SketchObject] Sketch102
  MapMode = 5
  Placement = pos=(0,0,0) rot=(0.57735,0.57735,0.57735;2.0944rad)
  Support = -> [YZ_Plane069]
  expr: Constraints[11] = 3.5 / 2
  expr: Constraints[10] = 12.7
  sketch-geometry (5):
    g0: LineSegment StartX=-4.6 StartY=0 StartZ=0 EndX=4.6 EndY=0 EndZ=0
    g1: LineSegment StartX=-6.35 StartY=-1.75 StartZ=0 EndX=-6.35 EndY=-4.35 EndZ=0
    g2: LineSegment StartX=6.35 StartY=-1.75 StartZ=0 EndX=6.35 EndY=-4.35 EndZ=0
    g3: ArcOfCircle CenterX=-4.6 CenterY=-1.75 CenterZ=0 NormalX=0 NormalY=0 NormalZ=1 AngleXU=0 Radius=1.75 StartAngle=1.5708 EndAngle=3.14159
    g4: ArcOfCircle CenterX=4.6 CenterY=-1.75 CenterZ=0 NormalX=0 NormalY=0 NormalZ=1 AngleXU=0 Radius=1.75 StartAngle=-1.084e-13 EndAngle=1.5708
  constraints (13):
    c: Vertical(g1)
    c: Vertical(g2)
    c: Equal(g2,g1)
    c: Tangent(g0,g3) = 1.5708
    c: Tangent(g1,g3) = -1.5708
    c: Tangent(g0,g4) = 1.5708
    c: Tangent(g2,g4) = 1.5708
    c: Symmetric(g0,g0,g-2)
    c: Equal(g4,g3)
    c: PointOnObject(g0,g-1)
    c: DistanceX(g1,g2) = 12.7
    c: DistanceY(g1,g0) = 1.75
    c: DistanceY(g1,g1) = 2.6
FEATURE [Sketcher::SketchObject] Sketch103
  AttachmentOffset = pos=(0,0,0) rot=(0,0,1;-1.5708rad)
  MapMode = 5
  Placement = pos=(0,0,0) rot=(-0.57735,-0.57735,0.57735;4.18879rad)
  Support = -> [XZ_Plane065]
  expr: Constraints[1] = 0.55 / 2
  sketch-geometry (1):
    g0: Circle CenterX=0 CenterY=0 CenterZ=0 NormalX=0 NormalY=0 NormalZ=1 AngleXU=0 Radius=0.275
  constraints (2):
    c: Coincident(g0,g-1)
    c: Radius(g0) = 0.275
FEATURE [Sketcher::SketchObject] Sketch107
  AttachmentOffset = pos=(0,0,0) rot=(0,0,1;-1.5708rad)
  MapMode = 5
  Placement = pos=(0,0,0) rot=(-0.57735,-0.57735,0.57735;4.18879rad)
  Support = -> [XZ_Plane073]
  expr: Constraints[1] = 3.5 / 2
  sketch-geometry (1):
    g0: Circle CenterX=0 CenterY=0 CenterZ=0 NormalX=0 NormalY=0 NormalZ=1 AngleXU=0 Radius=1.75
  constraints (2):
    c: Coincident(g0,g-1)
    c: Radius(g0) = 1.75
FEATURE [PartDesign::Pad] Pad029
  Length = 10
  Length2 = 100
  Midplane = true
  Placement = pos=(0,0,0) rot=(1,0,0;1.5708rad)
  Profile = -> Sketch107
  Type = 0
  expr: Length = 10
FEATURE [Sketcher::SketchObject] Sketch108
  AttachmentOffset = pos=(0,0,0) rot=(0,0,1;-1.5708rad)
  MapMode = 5
  Placement = pos=(0,0,0) rot=(-0.57735,-0.57735,0.57735;4.18879rad)
  Support = -> [XZ_Plane069]
  expr: Constraints[1] = 0.55 / 2
  sketch-geometry (1):
    g0: Circle CenterX=0 CenterY=0 CenterZ=0 NormalX=0 NormalY=0 NormalZ=1 AngleXU=0 Radius=0.275
  constraints (2):
    c: Coincident(g0,g-1)
    c: Radius(g0) = 0.275
FEATURE [PartDesign::AdditivePipe] AdditivePipe037
  AuxilleryCurvelinear = true
  AuxillerySpineTangent = false
  Binormal = (0,0,0)
  Mode = 0
  Placement = pos=(0,0,0) rot=(1,0,0;1.5708rad)
  Profile = -> Sketch108
  Refine = true
  Spine = -> Sketch101
  SpineTangent = false
  Transformation = 0
  Transition = 0
FEATURE [PartDesign::Body] Body066  label="1/8W_15.24_H004"
  Group = -> [Sketch101,Sketch108,AdditivePipe037]
  Origin = -> Origin075
  Tip = -> AdditivePipe037
FEATURE [Sketcher::SketchObject] Sketch109
  MapMode = 5
  Placement = pos=(0,0,0) rot=(0.57735,0.57735,0.57735;2.0944rad)
  Support = -> [YZ_Plane065]
  expr: Constraints[18] = 3.5 / 2
  expr: Constraints[9] = 10 / 2
  expr: Constraints[3] = 10 / 2
  sketch-geometry (8):
    g0: LineSegment StartX=7.6 StartY=0 StartZ=0 EndX=-5 EndY=0 EndZ=0
    g1: LineSegment StartX=-5 StartY=-5.08 StartZ=0 EndX=7.6 EndY=-5.08 EndZ=0
    g2: GeomPoint X=5 Y=0 Z=0
    g3: GeomPoint X=5 Y=-5.08 Z=0
    g4: GeomPoint X=-5 Y=0 Z=0
    g5: LineSegment StartX=-6.75 StartY=-1.75 StartZ=0 EndX=-6.75 EndY=-3.33 EndZ=0
    g6: ArcOfCircle CenterX=-5 CenterY=-1.75 CenterZ=0 NormalX=0 NormalY=0 NormalZ=1 AngleXU=0 Radius=1.75 StartAngle=1.5708 EndAngle=3.14159
    g7: ArcOfCircle CenterX=-5 CenterY=-3.33 CenterZ=0 NormalX=0 NormalY=0 NormalZ=1 AngleXU=0 Radius=1.75 StartAngle=3.14159 EndAngle=4.71239
  constraints (20):
    c: PointOnObject(g0,g-1)
    c: Horizontal(g1)
    c: PointOnObject(g2,g0)
    c: DistanceX(g-1,g2) = 5
    c: DistanceX(g2,g0) = 2.6
    c: PointOnObject(g3,g1)
    c: DistanceX(g3,g1) = 2.6
    c: Vertical(g0,g1)
    c: PointOnObject(g4,g0)
    c: DistanceX(g4,g-1) = 5
    c: Vertical(g5)
    c: Tangent(g0,g6) = -1.5708
    c: Tangent(g5,g6) = -1.5708
    c: Tangent(g1,g7) = -1.5708
    c: Tangent(g5,g7) = -1.5708
    c: DistanceY(g1,g0) = 5.08
    c: PointOnObject(g0,g-1)
    c: Equal(g7,g6)
    c: Radius(g6) = 1.75
    c: DistanceX(g0,g4) = 0
FEATURE [PartDesign::AdditivePipe] AdditivePipe038
  AuxilleryCurvelinear = true
  AuxillerySpineTangent = false
  Binormal = (0,0,0)
  Mode = 0
  Placement = pos=(0,0,0) rot=(1,0,0;1.5708rad)
  Profile = -> Sketch103
  Refine = true
  Spine = -> Sketch109
  SpineTangent = false
  Transformation = 0
  Transition = 0
FEATURE [PartDesign::Body] Body064  label="1/8W_5.08_V004"
  Group = -> [Sketch109,Sketch103,AdditivePipe038]
  Origin = -> Origin070
  Tip = -> AdditivePipe038
FEATURE [Sketcher::SketchObject] Sketch111
  AttachmentOffset = pos=(0,0,0) rot=(0,0,1;-1.5708rad)
  MapMode = 5
  Placement = pos=(0,0,0) rot=(-0.57735,-0.57735,0.57735;4.18879rad)
  Support = -> [XZ_Plane075]
  expr: Constraints[1] = 3.5 / 2
  sketch-geometry (1):
    g0: Circle CenterX=0 CenterY=0 CenterZ=0 NormalX=0 NormalY=0 NormalZ=1 AngleXU=0 Radius=1.75
  constraints (2):
    c: Coincident(g0,g-1)
    c: Radius(g0) = 1.75
FEATURE [PartDesign::Pad] Pad031
  Length = 10
  Length2 = 100
  Midplane = true
  Placement = pos=(0,0,0) rot=(1,0,0;1.5708rad)
  Profile = -> Sketch111
  Type = 0
  expr: Length = 10
FEATURE [Sketcher::SketchObject] Sketch113
  AttachmentOffset = pos=(0,0,0) rot=(0,0,1;-1.5708rad)
  MapMode = 5
  Placement = pos=(0,0,0) rot=(-0.57735,-0.57735,0.57735;4.18879rad)
  Support = -> [XZ_Plane074]
  expr: Constraints[1] = 3.5 / 2
  sketch-geometry (1):
    g0: Circle CenterX=0 CenterY=0 CenterZ=0 NormalX=0 NormalY=0 NormalZ=1 AngleXU=0 Radius=1.75
  constraints (2):
    c: Coincident(g0,g-1)
    c: Radius(g0) = 1.75
FEATURE [PartDesign::Pad] Pad030
  Length = 10
  Length2 = 100
  Midplane = true
  Placement = pos=(0,0,0) rot=(1,0,0;1.5708rad)
  Profile = -> Sketch113
  Type = 0
  expr: Length = 10
FEATURE [Sketcher::SketchObject] Sketch114
  AttachmentOffset = pos=(0,0,0) rot=(0,0,1;-1.5708rad)
  MapMode = 5
  Placement = pos=(0,0,0) rot=(-0.57735,-0.57735,0.57735;4.18879rad)
  Support = -> [XZ_Plane066]
  expr: Constraints[1] = 0.55 / 2
  sketch-geometry (1):
    g0: Circle CenterX=0 CenterY=0 CenterZ=0 NormalX=0 NormalY=0 NormalZ=1 AngleXU=0 Radius=0.275
  constraints (2):
    c: Coincident(g0,g-1)
    c: Radius(g0) = 0.275
FEATURE [PartDesign::AdditivePipe] AdditivePipe034
  AuxilleryCurvelinear = true
  AuxillerySpineTangent = false
  Binormal = (0,0,0)
  Mode = 0
  Placement = pos=(0,0,0) rot=(1,0,0;1.5708rad)
  Profile = -> Sketch114
  Refine = true
  Spine = -> Sketch102
  SpineTangent = false
  Transformation = 0
  Transition = 0
FEATURE [PartDesign::Body] Body065  label="1/8W_12.70_H004"
  Group = -> [Sketch102,Sketch114,AdditivePipe034]
  Origin = -> Origin071
  Tip = -> AdditivePipe034
FEATURE [PartDesign::Body] Body067  label="1/8W_Body027"
  Group = -> [Sketch111,Pad031]
  Origin = -> Origin065
  Tip = -> Pad031
FEATURE [Part::MultiFuse] Fusion028  label="R_MF50_P12.70_H"
  Placement = pos=(0,0,1) rot=(0,0,1;1.5708rad)
  Shapes = -> [Body067,Body065]
FEATURE [PartDesign::Body] Body069  label="1/8W_Body028"
  Group = -> [Sketch113,Pad030]
  Origin = -> Origin068
  Tip = -> Pad030
FEATURE [Part::MultiFuse] Fusion029  label="R_MF50_P15.24_H"
  Placement = pos=(0,0,1) rot=(0,0,-1;1.5708rad)
  Shapes = -> [Body069,Body066]
FEATURE [PartDesign::Body] Body071  label="1/8W_Body030"
  Group = -> [Sketch107,Pad029]
  Origin = -> Origin064
  Tip = -> Pad029
FEATURE [Part::MultiFuse] Fusion031  label="R_MF50_P5.08_V"
  Placement = pos=(-2.54,0,1.75) rot=(0.57735,0.57735,-0.57735;4.18879rad)
  Shapes = -> [Body071,Body064]
FEATURE [Sketcher::SketchObject] Sketch116
  AttachmentOffset = pos=(0,0,0) rot=(0,0,1;-1.5708rad)
  MapMode = 5
  Placement = pos=(0,0,0) rot=(-0.57735,-0.57735,0.57735;4.18879rad)
  Support = -> [XZ_Plane076]
  expr: Constraints[1] = 0.55 / 2
  sketch-geometry (1):
    g0: Circle CenterX=0 CenterY=0 CenterZ=0 NormalX=0 NormalY=0 NormalZ=1 AngleXU=0 Radius=0.275
  constraints (2):
    c: Coincident(g0,g-1)
    c: Radius(g0) = 0.275
FEATURE [Sketcher::SketchObject] Sketch117
  AttachmentOffset = pos=(0,0,0) rot=(0,0,1;-1.5708rad)
  MapMode = 5
  Placement = pos=(0,0,0) rot=(-0.57735,-0.57735,0.57735;4.18879rad)
  Support = -> [XZ_Plane077]
  expr: Constraints[1] = 3.5 / 2
  sketch-geometry (1):
    g0: Circle CenterX=0 CenterY=0 CenterZ=0 NormalX=0 NormalY=0 NormalZ=1 AngleXU=0 Radius=1.75
  constraints (2):
    c: Coincident(g0,g-1)
    c: Radius(g0) = 1.75
FEATURE [PartDesign::Pad] Pad033
  Length = 10
  Length2 = 100
  Midplane = true
  Placement = pos=(0,0,0) rot=(1,0,0;1.5708rad)
  Profile = -> Sketch117
  Type = 0
  expr: Length = 10
FEATURE [Sketcher::SketchObject] Sketch118
  MapMode = 5
  Placement = pos=(0,0,0) rot=(0.57735,0.57735,0.57735;2.0944rad)
  Support = -> [YZ_Plane077]
  expr: Constraints[18] = 2.5 / 2
  expr: Constraints[9] = 10 / 2
  expr: Constraints[3] = 10 / 2
  sketch-geometry (8):
    g0: LineSegment StartX=7.6 StartY=0 StartZ=0 EndX=-5 EndY=0 EndZ=0
    g1: LineSegment StartX=-5 StartY=-2.54 StartZ=0 EndX=7.6 EndY=-2.54 EndZ=0
    g2: GeomPoint X=5 Y=-7e-16 Z=0
    g3: GeomPoint X=5 Y=-2.54 Z=0
    g4: GeomPoint X=-5 Y=0 Z=0
    g5: LineSegment StartX=-6.25 StartY=-1.25 StartZ=0 EndX=-6.25 EndY=-1.29 EndZ=0
    g6: ArcOfCircle CenterX=-5 CenterY=-1.25 CenterZ=0 NormalX=0 NormalY=0 NormalZ=1 AngleXU=0 Radius=1.25 StartAngle=1.5708 EndAngle=3.14159
    g7: ArcOfCircle CenterX=-5 CenterY=-1.29 CenterZ=0 NormalX=0 NormalY=0 NormalZ=1 AngleXU=0 Radius=1.25 StartAngle=3.14159 EndAngle=4.71239
  constraints (20):
    c: PointOnObject(g0,g-1)
    c: Horizontal(g1)
    c: PointOnObject(g2,g0)
    c: DistanceX(g-1,g2) = 5
    c: DistanceX(g2,g0) = 2.6
    c: PointOnObject(g3,g1)
    c: DistanceX(g3,g1) = 2.6
    c: Vertical(g0,g1)
    c: PointOnObject(g4,g0)
    c: DistanceX(g4,g-1) = 5
    c: Vertical(g5)
    c: Tangent(g0,g6) = -1.5708
    c: Tangent(g5,g6) = -1.5708
    c: Tangent(g1,g7) = -1.5708
    c: Tangent(g5,g7) = -1.5708
    c: DistanceY(g1,g0) = 2.54
    c: PointOnObject(g0,g-1)
    c: Equal(g7,g6)
    c: Radius(g6) = 1.25
    c: DistanceX(g0,g4) = 0
FEATURE [PartDesign::Body] Body077  label="1/8W_Body033"
  Group = -> [Sketch117,Pad033]
  Origin = -> Origin077
  Tip = -> Pad033
FEATURE [PartDesign::AdditivePipe] AdditivePipe039
  AuxilleryCurvelinear = true
  AuxillerySpineTangent = false
  Binormal = (0,0,0)
  Mode = 0
  Placement = pos=(0,0,0) rot=(1,0,0;1.5708rad)
  Profile = -> Sketch116
  Refine = true
  Spine = -> Sketch118
  SpineTangent = false
  Transformation = 0
  Transition = 0
FEATURE [PartDesign::Body] Body076  label="1/8W_5.08_V005"
  Group = -> [Sketch118,Sketch116,AdditivePipe039]
  Origin = -> Origin076
  Tip = -> AdditivePipe039
FEATURE [Part::MultiFuse] Fusion032  label="R_MF50_P2.54_V"
  Placement = pos=(-2.54,0,1.75) rot=(0.57735,0.57735,-0.57735;4.18879rad)
  Shapes = -> [Body077,Body076]
FEATURE [App::DocumentObjectGroup] Group005  label="1/2W_MF"
  Group = -> [Fusion031,Fusion028,Fusion029,Fusion032]
FEATURE [Sketcher::SketchObject] Sketch119
  MapMode = 5
  Placement = pos=(0,0,0) rot=(0.57735,0.57735,0.57735;2.0944rad)
  Support = -> [YZ_Plane079]
  expr: Constraints[11] = 3.5 / 2
  expr: Constraints[10] = 15.24
  sketch-geometry (5):
    g0: LineSegment StartX=-5.87 StartY=-5.4e-14 StartZ=0 EndX=5.87 EndY=0 EndZ=0
    g1: LineSegment StartX=-7.62 StartY=-1.75 StartZ=0 EndX=-7.62 EndY=-4.35 EndZ=0
    g2: LineSegment StartX=7.62 StartY=-1.75 StartZ=0 EndX=7.62 EndY=-4.35 EndZ=0
    g3: ArcOfCircle CenterX=-5.87 CenterY=-1.75 CenterZ=0 NormalX=0 NormalY=0 NormalZ=1 AngleXU=0 Radius=1.75 StartAngle=1.5708 EndAngle=3.14159
    g4: ArcOfCircle CenterX=5.87 CenterY=-1.75 CenterZ=0 NormalX=0 NormalY=0 NormalZ=1 AngleXU=0 Radius=1.75 StartAngle=-6.93e-14 EndAngle=1.5708
  constraints (13):
    c: Vertical(g1)
    c: Vertical(g2)
    c: Equal(g2,g1)
    c: Tangent(g0,g3) = 1.5708
    c: Tangent(g1,g3) = -1.5708
    c: Tangent(g0,g4) = 1.5708
    c: Tangent(g2,g4) = 1.5708
    c: Symmetric(g0,g0,g-2)
    c: Equal(g4,g3)
    c: PointOnObject(g0,g-1)
    c: DistanceX(g1,g2) = 15.24
    c: DistanceY(g1,g0) = 1.75
    c: DistanceY(g1,g1) = 2.6
FEATURE [Sketcher::SketchObject] Sketch120
  AttachmentOffset = pos=(0,0,0) rot=(0,0,1;-1.5708rad)
  MapMode = 5
  Placement = pos=(0,0,0) rot=(-0.57735,-0.57735,0.57735;4.18879rad)
  Support = -> [XZ_Plane080]
  expr: Constraints[1] = 0.55 / 2
  sketch-geometry (1):
    g0: Circle CenterX=0 CenterY=0 CenterZ=0 NormalX=0 NormalY=0 NormalZ=1 AngleXU=0 Radius=0.275
  constraints (2):
    c: Coincident(g0,g-1)
    c: Radius(g0) = 0.275
FEATURE [Sketcher::SketchObject] Sketch121
  MapMode = 5
  Placement = pos=(0,0,0) rot=(0.57735,0.57735,0.57735;2.0944rad)
  Support = -> [YZ_Plane080]
  expr: Constraints[11] = 3.5 / 2
  expr: Constraints[10] = 12.7
  sketch-geometry (5):
    g0: LineSegment StartX=-4.6 StartY=0 StartZ=0 EndX=4.6 EndY=0 EndZ=0
    g1: LineSegment StartX=-6.35 StartY=-1.75 StartZ=0 EndX=-6.35 EndY=-4.35 EndZ=0
    g2: LineSegment StartX=6.35 StartY=-1.75 StartZ=0 EndX=6.35 EndY=-4.35 EndZ=0
    g3: ArcOfCircle CenterX=-4.6 CenterY=-1.75 CenterZ=0 NormalX=0 NormalY=0 NormalZ=1 AngleXU=0 Radius=1.75 StartAngle=1.5708 EndAngle=3.14159
    g4: ArcOfCircle CenterX=4.6 CenterY=-1.75 CenterZ=0 NormalX=0 NormalY=0 NormalZ=1 AngleXU=0 Radius=1.75 StartAngle=-1.084e-13 EndAngle=1.5708
  constraints (13):
    c: Vertical(g1)
    c: Vertical(g2)
    c: Equal(g2,g1)
    c: Tangent(g0,g3) = 1.5708
    c: Tangent(g1,g3) = -1.5708
    c: Tangent(g0,g4) = 1.5708
    c: Tangent(g2,g4) = 1.5708
    c: Symmetric(g0,g0,g-2)
    c: Equal(g4,g3)
    c: PointOnObject(g0,g-1)
    c: DistanceX(g1,g2) = 12.7
    c: DistanceY(g1,g0) = 1.75
    c: DistanceY(g1,g1) = 2.6
FEATURE [Sketcher::SketchObject] Sketch122
  AttachmentOffset = pos=(0,0,0) rot=(0,0,1;-1.5708rad)
  MapMode = 5
  Placement = pos=(0,0,0) rot=(-0.57735,-0.57735,0.57735;4.18879rad)
  Support = -> [XZ_Plane078]
  expr: Constraints[1] = 0.55 / 2
  sketch-geometry (1):
    g0: Circle CenterX=0 CenterY=0 CenterZ=0 NormalX=0 NormalY=0 NormalZ=1 AngleXU=0 Radius=0.275
  constraints (2):
    c: Coincident(g0,g-1)
    c: Radius(g0) = 0.275
FEATURE [Sketcher::SketchObject] Sketch123
  AttachmentOffset = pos=(0,0,0) rot=(0,0,1;-1.5708rad)
  MapMode = 5
  Placement = pos=(0,0,0) rot=(-0.57735,-0.57735,0.57735;4.18879rad)
  Support = -> [XZ_Plane085]
  expr: Constraints[1] = 3.5 / 2
  sketch-geometry (1):
    g0: Circle CenterX=0 CenterY=0 CenterZ=0 NormalX=0 NormalY=0 NormalZ=1 AngleXU=0 Radius=1.75
  constraints (2):
    c: Coincident(g0,g-1)
    c: Radius(g0) = 1.75
FEATURE [PartDesign::Pad] Pad034
  Length = 10
  Length2 = 100
  Midplane = true
  Placement = pos=(0,0,0) rot=(1,0,0;1.5708rad)
  Profile = -> Sketch123
  Type = 0
  expr: Length = 10
FEATURE [Sketcher::SketchObject] Sketch124
  MapMode = 5
  Placement = pos=(0,0,0) rot=(0.57735,0.57735,0.57735;2.0944rad)
  Support = -> [YZ_Plane081]
  expr: Constraints[18] = 3.5 / 2
  expr: Constraints[9] = 10 / 2
  expr: Constraints[3] = 10 / 2
  sketch-geometry (8):
    g0: LineSegment StartX=7.6 StartY=0 StartZ=0 EndX=-5 EndY=0 EndZ=0
    g1: LineSegment StartX=-5 StartY=-5.08 StartZ=0 EndX=7.6 EndY=-5.08 EndZ=0
    g2: GeomPoint X=5 Y=0 Z=0
    g3: GeomPoint X=5 Y=-5.08 Z=0
    g4: GeomPoint X=-5 Y=0 Z=0
    g5: LineSegment StartX=-6.75 StartY=-1.75 StartZ=0 EndX=-6.75 EndY=-3.33 EndZ=0
    g6: ArcOfCircle CenterX=-5 CenterY=-1.75 CenterZ=0 NormalX=0 NormalY=0 NormalZ=1 AngleXU=0 Radius=1.75 StartAngle=1.5708 EndAngle=3.14159
    g7: ArcOfCircle CenterX=-5 CenterY=-3.33 CenterZ=0 NormalX=0 NormalY=0 NormalZ=1 AngleXU=0 Radius=1.75 StartAngle=3.14159 EndAngle=4.71239
  constraints (20):
    c: PointOnObject(g0,g-1)
    c: Horizontal(g1)
    c: PointOnObject(g2,g0)
    c: DistanceX(g-1,g2) = 5
    c: DistanceX(g2,g0) = 2.6
    c: PointOnObject(g3,g1)
    c: DistanceX(g3,g1) = 2.6
    c: Vertical(g0,g1)
    c: PointOnObject(g4,g0)
    c: DistanceX(g4,g-1) = 5
    c: Vertical(g5)
    c: Tangent(g0,g6) = -1.5708
    c: Tangent(g5,g6) = -1.5708
    c: Tangent(g1,g7) = -1.5708
    c: Tangent(g5,g7) = -1.5708
    c: DistanceY(g1,g0) = 5.08
    c: PointOnObject(g0,g-1)
    c: Equal(g7,g6)
    c: Radius(g6) = 1.75
    c: DistanceX(g0,g4) = 0
FEATURE [Sketcher::SketchObject] Sketch125
  AttachmentOffset = pos=(0,0,0) rot=(0,0,1;-1.5708rad)
  MapMode = 5
  Placement = pos=(0,0,0) rot=(-0.57735,-0.57735,0.57735;4.18879rad)
  Support = -> [XZ_Plane081]
  expr: Constraints[1] = 3.5 / 2
  sketch-geometry (1):
    g0: Circle CenterX=0 CenterY=0 CenterZ=0 NormalX=0 NormalY=0 NormalZ=1 AngleXU=0 Radius=1.75
  constraints (2):
    c: Coincident(g0,g-1)
    c: Radius(g0) = 1.75
FEATURE [PartDesign::Pad] Pad036
  Length = 10
  Length2 = 100
  Midplane = true
  Placement = pos=(0,0,0) rot=(1,0,0;1.5708rad)
  Profile = -> Sketch125
  Type = 0
  expr: Length = 10
FEATURE [PartDesign::Body] Body080  label="1/8W_Body034"
  Group = -> [Sketch125,Pad036]
  Origin = -> Origin084
  Tip = -> Pad036
FEATURE [PartDesign::Body] Body083  label="1/8W_Body036"
  Group = -> [Sketch123,Pad034]
  Origin = -> Origin085
  Tip = -> Pad034
FEATURE [Sketcher::SketchObject] Sketch126
  MapMode = 5
  Placement = pos=(0,0,0) rot=(0.57735,0.57735,0.57735;2.0944rad)
  Support = -> [YZ_Plane083]
  expr: Constraints[18] = 2.5 / 2
  expr: Constraints[9] = 10 / 2
  expr: Constraints[3] = 10 / 2
  sketch-geometry (8):
    g0: LineSegment StartX=7.6 StartY=0 StartZ=0 EndX=-5 EndY=0 EndZ=0
    g1: LineSegment StartX=-5 StartY=-2.54 StartZ=0 EndX=7.6 EndY=-2.54 EndZ=0
    g2: GeomPoint X=5 Y=-7e-16 Z=0
    g3: GeomPoint X=5 Y=-2.54 Z=0
    g4: GeomPoint X=-5 Y=0 Z=0
    g5: LineSegment StartX=-6.25 StartY=-1.25 StartZ=0 EndX=-6.25 EndY=-1.29 EndZ=0
    g6: ArcOfCircle CenterX=-5 CenterY=-1.25 CenterZ=0 NormalX=0 NormalY=0 NormalZ=1 AngleXU=0 Radius=1.25 StartAngle=1.5708 EndAngle=3.14159
    g7: ArcOfCircle CenterX=-5 CenterY=-1.29 CenterZ=0 NormalX=0 NormalY=0 NormalZ=1 AngleXU=0 Radius=1.25 StartAngle=3.14159 EndAngle=4.71239
  constraints (20):
    c: PointOnObject(g0,g-1)
    c: Horizontal(g1)
    c: PointOnObject(g2,g0)
    c: DistanceX(g-1,g2) = 5
    c: DistanceX(g2,g0) = 2.6
    c: PointOnObject(g3,g1)
    c: DistanceX(g3,g1) = 2.6
    c: Vertical(g0,g1)
    c: PointOnObject(g4,g0)
    c: DistanceX(g4,g-1) = 5
    c: Vertical(g5)
    c: Tangent(g0,g6) = -1.5708
    c: Tangent(g5,g6) = -1.5708
    c: Tangent(g1,g7) = -1.5708
    c: Tangent(g5,g7) = -1.5708
    c: DistanceY(g1,g0) = 2.54
    c: PointOnObject(g0,g-1)
    c: Equal(g7,g6)
    c: Radius(g6) = 1.25
    c: DistanceX(g0,g4) = 0
FEATURE [Sketcher::SketchObject] Sketch127
  AttachmentOffset = pos=(0,0,0) rot=(0,0,1;-1.5708rad)
  MapMode = 5
  Placement = pos=(0,0,0) rot=(-0.57735,-0.57735,0.57735;4.18879rad)
  Support = -> [XZ_Plane083]
  expr: Constraints[1] = 3.5 / 2
  sketch-geometry (1):
    g0: Circle CenterX=0 CenterY=0 CenterZ=0 NormalX=0 NormalY=0 NormalZ=1 AngleXU=0 Radius=1.75
  constraints (2):
    c: Coincident(g0,g-1)
    c: Radius(g0) = 1.75
FEATURE [PartDesign::Pad] Pad035
  Length = 10
  Length2 = 100
  Midplane = true
  Placement = pos=(0,0,0) rot=(1,0,0;1.5708rad)
  Profile = -> Sketch127
  Type = 0
  expr: Length = 10
FEATURE [PartDesign::Body] Body081  label="1/8W_Body035"
  Group = -> [Sketch127,Pad035]
  Origin = -> Origin078
  Tip = -> Pad035
FEATURE [Sketcher::SketchObject] Sketch128
  AttachmentOffset = pos=(0,0,0) rot=(0,0,1;-1.5708rad)
  MapMode = 5
  Placement = pos=(0,0,0) rot=(-0.57735,-0.57735,0.57735;4.18879rad)
  Support = -> [XZ_Plane084]
  expr: Constraints[1] = 0.55 / 2
  sketch-geometry (1):
    g0: Circle CenterX=0 CenterY=0 CenterZ=0 NormalX=0 NormalY=0 NormalZ=1 AngleXU=0 Radius=0.275
  constraints (2):
    c: Coincident(g0,g-1)
    c: Radius(g0) = 0.275
FEATURE [Sketcher::SketchObject] Sketch129
  AttachmentOffset = pos=(0,0,0) rot=(0,0,1;-1.5708rad)
  MapMode = 5
  Placement = pos=(0,0,0) rot=(-0.57735,-0.57735,0.57735;4.18879rad)
  Support = -> [XZ_Plane082]
  expr: Constraints[1] = 3.5 / 2
  sketch-geometry (1):
    g0: Circle CenterX=0 CenterY=0 CenterZ=0 NormalX=0 NormalY=0 NormalZ=1 AngleXU=0 Radius=1.75
  constraints (2):
    c: Coincident(g0,g-1)
    c: Radius(g0) = 1.75
FEATURE [PartDesign::Pad] Pad037
  Length = 10
  Length2 = 100
  Midplane = true
  Placement = pos=(0,0,0) rot=(1,0,0;1.5708rad)
  Profile = -> Sketch129
  Type = 0
  expr: Length = 10
FEATURE [Sketcher::SketchObject] Sketch130
  AttachmentOffset = pos=(0,0,0) rot=(0,0,1;-1.5708rad)
  MapMode = 5
  Placement = pos=(0,0,0) rot=(-0.57735,-0.57735,0.57735;4.18879rad)
  Support = -> [XZ_Plane079]
  expr: Constraints[1] = 0.55 / 2
  sketch-geometry (1):
    g0: Circle CenterX=0 CenterY=0 CenterZ=0 NormalX=0 NormalY=0 NormalZ=1 AngleXU=0 Radius=0.275
  constraints (2):
    c: Coincident(g0,g-1)
    c: Radius(g0) = 0.275
FEATURE [PartDesign::Body] Body085  label="1/8W_Body037"
  Group = -> [Sketch129,Pad037]
  Origin = -> Origin083
  Tip = -> Pad037
FEATURE [PartDesign::AdditivePipe] AdditivePipe040
  AuxilleryCurvelinear = true
  AuxillerySpineTangent = false
  Binormal = (0,0,0)
  Mode = 0
  Placement = pos=(0,0,0) rot=(1,0,0;1.5708rad)
  Profile = -> Sketch128
  Refine = true
  Spine = -> Sketch126
  SpineTangent = false
  Transformation = 0
  Transition = 0
FEATURE [PartDesign::Body] Body084  label="1/8W_5.08_V007"
  Group = -> [Sketch126,Sketch128,AdditivePipe040]
  Origin = -> Origin082
  Tip = -> AdditivePipe040
FEATURE [Part::MultiFuse] Fusion033  label="R_CF50_P2.54_V"
  Placement = pos=(-2.54,0,1.75) rot=(0.57735,0.57735,-0.57735;4.18879rad)
  Shapes = -> [Body085,Body084]
FEATURE [PartDesign::AdditivePipe] AdditivePipe041
  AuxilleryCurvelinear = true
  AuxillerySpineTangent = false
  Binormal = (0,0,0)
  Mode = 0
  Placement = pos=(0,0,0) rot=(1,0,0;1.5708rad)
  Profile = -> Sketch130
  Refine = true
  Spine = -> Sketch121
  SpineTangent = false
  Transformation = 0
  Transition = 0
FEATURE [PartDesign::Body] Body078  label="1/8W_12.70_H005"
  Group = -> [Sketch121,Sketch130,AdditivePipe041]
  Origin = -> Origin080
  Tip = -> AdditivePipe041
FEATURE [Part::MultiFuse] Fusion036  label="R_CF50_P12.70_H"
  Placement = pos=(0,0,1) rot=(0,0,1;1.5708rad)
  Shapes = -> [Body080,Body078]
FEATURE [PartDesign::AdditivePipe] AdditivePipe042
  AuxilleryCurvelinear = true
  AuxillerySpineTangent = false
  Binormal = (0,0,0)
  Mode = 0
  Placement = pos=(0,0,0) rot=(1,0,0;1.5708rad)
  Profile = -> Sketch122
  Refine = true
  Spine = -> Sketch119
  SpineTangent = false
  Transformation = 0
  Transition = 0
FEATURE [PartDesign::Body] Body079  label="1/8W_15.24_H005"
  Group = -> [Sketch119,Sketch122,AdditivePipe042]
  Origin = -> Origin081
  Tip = -> AdditivePipe042
FEATURE [Part::MultiFuse] Fusion035  label="R_CF50_P15.24_H"
  Placement = pos=(0,0,1) rot=(0,0,-1;1.5708rad)
  Shapes = -> [Body081,Body079]
FEATURE [PartDesign::AdditivePipe] AdditivePipe043
  AuxilleryCurvelinear = true
  AuxillerySpineTangent = false
  Binormal = (0,0,0)
  Mode = 0
  Placement = pos=(0,0,0) rot=(1,0,0;1.5708rad)
  Profile = -> Sketch120
  Refine = true
  Spine = -> Sketch124
  SpineTangent = false
  Transformation = 0
  Transition = 0
FEATURE [PartDesign::Body] Body082  label="1/8W_5.08_V006"
  Group = -> [Sketch124,Sketch120,AdditivePipe043]
  Origin = -> Origin079
  Tip = -> AdditivePipe043
FEATURE [Part::MultiFuse] Fusion034  label="R_CF50_P5.08_V"
  Placement = pos=(-2.54,0,1.75) rot=(0.57735,0.57735,-0.57735;4.18879rad)
  Shapes = -> [Body083,Body082]
FEATURE [App::DocumentObjectGroup] Group006  label="1/2W_CF"
  Group = -> [Fusion034,Fusion036,Fusion035,Fusion033]
FEATURE [Sketcher::SketchObject] Sketch131
  AttachmentOffset = pos=(0,0,0) rot=(0,0,1;-1.5708rad)
  MapMode = 5
  Placement = pos=(0,0,0) rot=(-0.57735,-0.57735,0.57735;4.18879rad)
  Support = -> [XZ_Plane096]
  expr: Constraints[1] = 2.5 / 2
  sketch-geometry (1):
    g0: Circle CenterX=0 CenterY=0 CenterZ=0 NormalX=0 NormalY=0 NormalZ=1 AngleXU=0 Radius=1.25
  constraints (2):
    c: Coincident(g0,g-1)
    c: Radius(g0) = 1.25
FEATURE [Sketcher::SketchObject] Sketch132
  AttachmentOffset = pos=(0,0,0) rot=(0,0,1;-1.5708rad)
  MapMode = 5
  Placement = pos=(0,0,0) rot=(-0.57735,-0.57735,0.57735;4.18879rad)
  Support = -> [XZ_Plane094]
  expr: Constraints[1] = 0.55 / 2
  sketch-geometry (1):
    g0: Circle CenterX=0 CenterY=0 CenterZ=0 NormalX=0 NormalY=0 NormalZ=1 AngleXU=0 Radius=0.275
  constraints (2):
    c: Coincident(g0,g-1)
    c: Radius(g0) = 0.275
FEATURE [Sketcher::SketchObject] Sketch134
  MapMode = 5
  Placement = pos=(0,0,0) rot=(0.57735,0.57735,0.57735;2.0944rad)
  Support = -> [YZ_Plane087]
  expr: Constraints[18] = 2.5 / 2
  expr: Constraints[9] = 6.5 / 2
  expr: Constraints[3] = 6.5 / 2
  sketch-geometry (8):
    g0: LineSegment StartX=5.85 StartY=0 StartZ=0 EndX=-3.25 EndY=0 EndZ=0
    g1: LineSegment StartX=-3.25 StartY=-5.08 StartZ=0 EndX=5.85 EndY=-5.08 EndZ=0
    g2: GeomPoint X=3.25 Y=0 Z=0
    g3: GeomPoint X=3.25 Y=-5.08 Z=0
    g4: GeomPoint X=-3.25 Y=0 Z=0
    g5: LineSegment StartX=-4.5 StartY=-1.25 StartZ=0 EndX=-4.5 EndY=-3.83 EndZ=0
    g6: ArcOfCircle CenterX=-3.25 CenterY=-1.25 CenterZ=0 NormalX=0 NormalY=0 NormalZ=1 AngleXU=0 Radius=1.25 StartAngle=1.5708 EndAngle=3.14159
    g7: ArcOfCircle CenterX=-3.25 CenterY=-3.83 CenterZ=0 NormalX=0 NormalY=0 NormalZ=1 AngleXU=0 Radius=1.25 StartAngle=3.14159 EndAngle=4.71239
  constraints (20):
    c: PointOnObject(g0,g-1)
    c: Horizontal(g1)
    c: PointOnObject(g2,g0)
    c: DistanceX(g-1,g2) = 3.25
    c: DistanceX(g2,g0) = 2.6
    c: PointOnObject(g3,g1)
    c: DistanceX(g3,g1) = 2.6
    c: Vertical(g0,g1)
    c: PointOnObject(g4,g0)
    c: DistanceX(g4,g-1) = 3.25
    c: Vertical(g5)
    c: Tangent(g0,g6) = -1.5708
    c: Tangent(g5,g6) = -1.5708
    c: Tangent(g1,g7) = -1.5708
    c: Tangent(g5,g7) = -1.5708
    c: DistanceY(g1,g0) = 5.08
    c: PointOnObject(g0,g-1)
    c: Equal(g7,g6)
    c: Radius(g6) = 1.25
    c: DistanceX(g0,g4) = 0
FEATURE [Sketcher::SketchObject] Sketch135
  AttachmentOffset = pos=(0,0,0) rot=(0,0,1;-1.5708rad)
  MapMode = 5
  Placement = pos=(0,0,0) rot=(-0.57735,-0.57735,0.57735;4.18879rad)
  Support = -> [XZ_Plane092]
  expr: Constraints[1] = 2.5 / 2
  sketch-geometry (1):
    g0: Circle CenterX=0 CenterY=0 CenterZ=0 NormalX=0 NormalY=0 NormalZ=1 AngleXU=0 Radius=1.25
  constraints (2):
    c: Coincident(g0,g-1)
    c: Radius(g0) = 1.25
FEATURE [Sketcher::SketchObject] Sketch136
  AttachmentOffset = pos=(0,0,0) rot=(0,0,1;-1.5708rad)
  MapMode = 5
  Placement = pos=(0,0,0) rot=(-0.57735,-0.57735,0.57735;4.18879rad)
  Support = -> [XZ_Plane090]
  expr: Constraints[1] = 2.5 / 2
  sketch-geometry (1):
    g0: Circle CenterX=0 CenterY=0 CenterZ=0 NormalX=0 NormalY=0 NormalZ=1 AngleXU=0 Radius=1.25
  constraints (2):
    c: Coincident(g0,g-1)
    c: Radius(g0) = 1.25
FEATURE [Sketcher::SketchObject] Sketch138
  AttachmentOffset = pos=(0,0,0) rot=(0,0,1;-1.5708rad)
  MapMode = 5
  Placement = pos=(0,0,0) rot=(-0.57735,-0.57735,0.57735;4.18879rad)
  Support = -> [XZ_Plane088]
  expr: Constraints[1] = 0.55 / 2
  sketch-geometry (1):
    g0: Circle CenterX=0 CenterY=0 CenterZ=0 NormalX=0 NormalY=0 NormalZ=1 AngleXU=0 Radius=0.275
  constraints (2):
    c: Coincident(g0,g-1)
    c: Radius(g0) = 0.275
FEATURE [Sketcher::SketchObject] Sketch139
  AttachmentOffset = pos=(0,0,0) rot=(0,0,1;-1.5708rad)
  MapMode = 5
  Placement = pos=(0,0,0) rot=(-0.57735,-0.57735,0.57735;4.18879rad)
  Support = -> [XZ_Plane097]
  expr: Constraints[1] = 0.55 / 2
  sketch-geometry (1):
    g0: Circle CenterX=0 CenterY=0 CenterZ=0 NormalX=0 NormalY=0 NormalZ=1 AngleXU=0 Radius=0.275
  constraints (2):
    c: Coincident(g0,g-1)
    c: Radius(g0) = 0.275
FEATURE [Sketcher::SketchObject] Sketch140
  MapMode = 5
  Placement = pos=(0,0,0) rot=(0.57735,0.57735,0.57735;2.0944rad)
  Support = -> [YZ_Plane092]
  expr: Constraints[11] = 2.5 / 2
  expr: Constraints[10] = 4 * 2.54
  sketch-geometry (5):
    g0: LineSegment StartX=-3.83 StartY=0 StartZ=0 EndX=3.83 EndY=-1.3e-15 EndZ=0
    g1: LineSegment StartX=-5.08 StartY=-1.25 StartZ=0 EndX=-5.08 EndY=-3.85 EndZ=0
    g2: LineSegment StartX=5.08 StartY=-1.25 StartZ=0 EndX=5.08 EndY=-3.85 EndZ=0
    g3: ArcOfCircle CenterX=-3.83 CenterY=-1.25 CenterZ=0 NormalX=0 NormalY=0 NormalZ=1 AngleXU=0 Radius=1.25 StartAngle=1.5708 EndAngle=3.14159
    g4: ArcOfCircle CenterX=3.83 CenterY=-1.25 CenterZ=0 NormalX=0 NormalY=0 NormalZ=1 AngleXU=0 Radius=1.25 StartAngle=0 EndAngle=1.5708
  constraints (13):
    c: Vertical(g1)
    c: Vertical(g2)
    c: Equal(g2,g1)
    c: Tangent(g0,g3) = 1.5708
    c: Tangent(g1,g3) = -1.5708
    c: Tangent(g0,g4) = 1.5708
    c: Tangent(g2,g4) = 1.5708
    c: Symmetric(g0,g0,g-2)
    c: Equal(g4,g3)
    c: PointOnObject(g0,g-1)
    c: DistanceX(g1,g2) = 10.16
    c: DistanceY(g1,g0) = 1.25
    c: DistanceY(g1,g1) = 2.6
FEATURE [PartDesign::AdditivePipe] AdditivePipe047
  AuxilleryCurvelinear = true
  AuxillerySpineTangent = false
  Binormal = (0,0,0)
  Mode = 0
  Placement = pos=(0,0,0) rot=(1,0,0;1.5708rad)
  Profile = -> Sketch139
  Refine = true
  Spine = -> Sketch140
  SpineTangent = false
  Transformation = 0
  Transition = 0
FEATURE [Sketcher::SketchObject] Sketch142
  AttachmentOffset = pos=(0,0,0) rot=(0,0,1;-1.5708rad)
  MapMode = 5
  Placement = pos=(0,0,0) rot=(-0.57735,-0.57735,0.57735;4.18879rad)
  Support = -> [XZ_Plane091]
  expr: Constraints[1] = 0.55 / 2
  sketch-geometry (1):
    g0: Circle CenterX=0 CenterY=0 CenterZ=0 NormalX=0 NormalY=0 NormalZ=1 AngleXU=0 Radius=0.275
  constraints (2):
    c: Coincident(g0,g-1)
    c: Radius(g0) = 0.275
FEATURE [Sketcher::SketchObject] Sketch143
  MapMode = 5
  Placement = pos=(0,0,0) rot=(0.57735,0.57735,0.57735;2.0944rad)
  Support = -> [YZ_Plane089]
  expr: Constraints[11] = 2.5 / 2
  expr: Constraints[10] = 3 * 2.54
  sketch-geometry (5):
    g0: LineSegment StartX=-2.56 StartY=-9e-16 StartZ=0 EndX=2.56 EndY=-2.4e-15 EndZ=0
    g1: LineSegment StartX=-3.81 StartY=-1.25 StartZ=0 EndX=-3.81 EndY=-3.85 EndZ=0
    g2: LineSegment StartX=3.81 StartY=-1.25 StartZ=0 EndX=3.81 EndY=-3.85 EndZ=0
    g3: ArcOfCircle CenterX=-2.56 CenterY=-1.25 CenterZ=0 NormalX=0 NormalY=0 NormalZ=1 AngleXU=0 Radius=1.25 StartAngle=1.5708 EndAngle=3.14159
    g4: ArcOfCircle CenterX=2.56 CenterY=-1.25 CenterZ=0 NormalX=0 NormalY=0 NormalZ=1 AngleXU=0 Radius=1.25 StartAngle=0 EndAngle=1.5708
  constraints (13):
    c: Vertical(g1)
    c: Vertical(g2)
    c: Equal(g2,g1)
    c: Tangent(g0,g3) = 1.5708
    c: Tangent(g1,g3) = -1.5708
    c: Tangent(g0,g4) = 1.5708
    c: Tangent(g2,g4) = 1.5708
    c: Symmetric(g0,g0,g-2)
    c: Equal(g4,g3)
    c: PointOnObject(g0,g-1)
    c: DistanceX(g1,g2) = 7.62
    c: DistanceY(g1,g0) = 1.25
    c: DistanceY(g1,g1) = 2.6
FEATURE [PartDesign::AdditivePipe] AdditivePipe046
  AuxilleryCurvelinear = true
  AuxillerySpineTangent = false
  Binormal = (0,0,0)
  Mode = 0
  Placement = pos=(0,0,0) rot=(1,0,0;1.5708rad)
  Profile = -> Sketch132
  Refine = true
  Spine = -> Sketch143
  SpineTangent = false
  Transformation = 0
  Transition = 0
FEATURE [Sketcher::SketchObject] Sketch144
  MapMode = 5
  Placement = pos=(0,0,0) rot=(0.57735,0.57735,0.57735;2.0944rad)
  Support = -> [YZ_Plane090]
  expr: Constraints[24] = 2.54
  expr: Constraints[15] = 2.5 / 2
  expr: Constraints[10] = 6.5 / 2
  expr: Constraints[4] = 6.5 / 2
  sketch-geometry (9):
    g0: LineSegment StartX=5.85 StartY=0 StartZ=0 EndX=-3.25 EndY=0 EndZ=0
    g1: LineSegment StartX=-3.25 StartY=-2.54 StartZ=0 EndX=5.85 EndY=-2.54 EndZ=0
    g2: GeomPoint X=3.25 Y=0 Z=0
    g3: GeomPoint X=3.25 Y=-2.54 Z=0
    g4: GeomPoint X=-4.5 Y=-1.25 Z=0
    g5: GeomPoint X=-3.25 Y=0 Z=0
    g6: ArcOfCircle CenterX=-3.25 CenterY=-1.25 CenterZ=0 NormalX=0 NormalY=0 NormalZ=1 AngleXU=0 Radius=1.25 StartAngle=1.5708 EndAngle=3.14159
    g7: LineSegment StartX=-4.5 StartY=-1.25 StartZ=0 EndX=-4.5 EndY=-1.29 EndZ=0
    g8: ArcOfCircle CenterX=-3.25 CenterY=-1.29 CenterZ=0 NormalX=0 NormalY=0 NormalZ=1 AngleXU=0 Radius=1.25 StartAngle=3.14159 EndAngle=4.71239
  constraints (25):
    c: PointOnObject(g0,g-1)
    c: PointOnObject(g0,g-1)
    c: Horizontal(g1)
    c: PointOnObject(g2,g0)
    c: DistanceX(g-1,g2) = 3.25
    c: DistanceX(g2,g0) = 2.6
    c: PointOnObject(g3,g1)
    c: DistanceX(g3,g1) = 2.6
    c: Vertical(g0,g1)
    c: PointOnObject(g5,g0)
    c: DistanceX(g5,g-1) = 3.25
    c: DistanceX(g0,g5) = 0
    c: Coincident(g6,g0)
    c: Coincident(g6,g4)
    c: Horizontal(g6,g4)
    c: Radius(g6) = 1.25
    c: Vertical(g6,g0)
    c: Coincident(g7,g4)
    c: Vertical(g7)
    c: Coincident(g8,g7)
    c: Coincident(g8,g1)
    c: Equal(g8,g6)
    c: Horizontal(g8,g7)
    c: Vertical(g8,g1)
    c: DistanceY(g1,g0) = 2.54
FEATURE [PartDesign::AdditivePipe] AdditivePipe045
  AuxilleryCurvelinear = true
  AuxillerySpineTangent = false
  Binormal = (0,0,0)
  Mode = 0
  Placement = pos=(0,0,0) rot=(1,0,0;1.5708rad)
  Profile = -> Sketch142
  Refine = true
  Spine = -> Sketch144
  SpineTangent = false
  Transformation = 0
  Transition = 0
FEATURE [Sketcher::SketchObject] Sketch145
  MapMode = 5
  Placement = pos=(0,0,0) rot=(0.57735,0.57735,0.57735;2.0944rad)
  Support = -> [YZ_Plane094]
  expr: Constraints[11] = 2.5 / 2
  expr: Constraints[10] = 12.7
  sketch-geometry (5):
    g0: LineSegment StartX=-5.1 StartY=-2e-16 StartZ=0 EndX=5.1 EndY=-7e-16 EndZ=0
    g1: LineSegment StartX=-6.35 StartY=-1.25 StartZ=0 EndX=-6.35 EndY=-3.85 EndZ=0
    g2: LineSegment StartX=6.35 StartY=-1.25 StartZ=0 EndX=6.35 EndY=-3.85 EndZ=0
    g3: ArcOfCircle CenterX=-5.1 CenterY=-1.25 CenterZ=0 NormalX=0 NormalY=0 NormalZ=1 AngleXU=0 Radius=1.25 StartAngle=1.5708 EndAngle=3.14159
    g4: ArcOfCircle CenterX=5.1 CenterY=-1.25 CenterZ=0 NormalX=0 NormalY=0 NormalZ=1 AngleXU=0 Radius=1.25 StartAngle=0 EndAngle=1.5708
  constraints (13):
    c: Vertical(g1)
    c: Vertical(g2)
    c: Equal(g2,g1)
    c: Tangent(g0,g3) = 1.5708
    c: Tangent(g1,g3) = -1.5708
    c: Tangent(g0,g4) = 1.5708
    c: Tangent(g2,g4) = 1.5708
    c: Symmetric(g0,g0,g-2)
    c: Equal(g4,g3)
    c: PointOnObject(g0,g-1)
    c: DistanceX(g1,g2) = 12.7
    c: DistanceY(g1,g0) = 1.25
    c: DistanceY(g1,g1) = 2.6
FEATURE [PartDesign::AdditivePipe] AdditivePipe044
  AuxilleryCurvelinear = true
  AuxillerySpineTangent = false
  Binormal = (0,0,0)
  Mode = 0
  Placement = pos=(0,0,0) rot=(1,0,0;1.5708rad)
  Profile = -> Sketch138
  Refine = true
  Spine = -> Sketch145
  SpineTangent = false
  Transformation = 0
  Transition = 0
FEATURE [Sketcher::SketchObject] Sketch146
  AttachmentOffset = pos=(0,0,0) rot=(0,0,1;-1.5708rad)
  MapMode = 5
  Placement = pos=(0,0,0) rot=(-0.57735,-0.57735,0.57735;4.18879rad)
  Support = -> [XZ_Plane089]
  expr: Constraints[1] = 0.55 / 2
  sketch-geometry (1):
    g0: Circle CenterX=0 CenterY=0 CenterZ=0 NormalX=0 NormalY=0 NormalZ=1 AngleXU=0 Radius=0.275
  constraints (2):
    c: Coincident(g0,g-1)
    c: Radius(g0) = 0.275
FEATURE [Sketcher::SketchObject] Sketch147
  AttachmentOffset = pos=(0,0,0) rot=(0,0,1;-1.5708rad)
  MapMode = 5
  Placement = pos=(0,0,0) rot=(-0.57735,-0.57735,0.57735;4.18879rad)
  Support = -> [XZ_Plane086]
  expr: Constraints[1] = 2.5 / 2
  sketch-geometry (1):
    g0: Circle CenterX=0 CenterY=0 CenterZ=0 NormalX=0 NormalY=0 NormalZ=1 AngleXU=0 Radius=1.25
  constraints (2):
    c: Coincident(g0,g-1)
    c: Radius(g0) = 1.25
FEATURE [PartDesign::Pad] Pad038
  Length = 6.5
  Length2 = 100
  Midplane = true
  Placement = pos=(0,0,0) rot=(1,0,0;1.5708rad)
  Profile = -> Sketch147
  Type = 0
  expr: Length = 6.5
FEATURE [PartDesign::Pad] Pad039
  Length = 6.5
  Length2 = 100
  Midplane = true
  Placement = pos=(0,0,0) rot=(1,0,0;1.5708rad)
  Profile = -> Sketch135
  Type = 0
  expr: Length = 6.5
FEATURE [PartDesign::Pad] Pad041
  Length = 6.5
  Length2 = 100
  Midplane = true
  Placement = pos=(0,0,0) rot=(1,0,0;1.5708rad)
  Profile = -> Sketch131
  Type = 0
  expr: Length = 6.5
FEATURE [PartDesign::Pad] Pad043
  Length = 6.5
  Length2 = 100
  Midplane = true
  Placement = pos=(0,0,0) rot=(1,0,0;1.5708rad)
  Profile = -> Sketch136
  Type = 0
  expr: Length = 6.5
FEATURE [PartDesign::Body] Body086  label="1/8W_Body038"
  Group = -> [Sketch136,Pad043]
  Origin = -> Origin096
  Tip = -> Pad043
FEATURE [Sketcher::SketchObject] Sketch148
  AttachmentOffset = pos=(0,0,0) rot=(0,0,1;-1.5708rad)
  MapMode = 5
  Placement = pos=(0,0,0) rot=(-0.57735,-0.57735,0.57735;4.18879rad)
  Support = -> [XZ_Plane095]
  expr: Constraints[1] = 2.5 / 2
  sketch-geometry (1):
    g0: Circle CenterX=0 CenterY=0 CenterZ=0 NormalX=0 NormalY=0 NormalZ=1 AngleXU=0 Radius=1.25
  constraints (2):
    c: Coincident(g0,g-1)
    c: Radius(g0) = 1.25
FEATURE [PartDesign::Pad] Pad042
  Length = 6.5
  Length2 = 100
  Midplane = true
  Placement = pos=(0,0,0) rot=(1,0,0;1.5708rad)
  Profile = -> Sketch148
  Type = 0
  expr: Length = 6.5
FEATURE [PartDesign::Body] Body087  label="1/8W_Body039"
  Group = -> [Sketch148,Pad042]
  Origin = -> Origin093
  Tip = -> Pad042
FEATURE [PartDesign::Body] Body089  label="1/8W_Body040"
  Group = -> [Sketch135,Pad039]
  Origin = -> Origin092
  Tip = -> Pad039
FEATURE [PartDesign::Body] Body090  label="1/8W_12.70_H006"
  Group = -> [Sketch145,Sketch138,AdditivePipe044]
  Origin = -> Origin097
  Tip = -> AdditivePipe044
FEATURE [Part::MultiFuse] Fusion039  label="R_CC25_P12.70_H"
  Placement = pos=(0,0,1) rot=(0,0,1;1.5708rad)
  Shapes = -> [Body089,Body090]
FEATURE [PartDesign::Body] Body092  label="1/8W_7.62_H004"
  Group = -> [Sketch143,Sketch132,AdditivePipe046]
  Origin = -> Origin091
  Tip = -> AdditivePipe046
FEATURE [PartDesign::Body] Body094  label="1/8W_2.54_V004"
  Group = -> [Sketch144,Sketch142,AdditivePipe045]
  Origin = -> Origin094
  Tip = -> AdditivePipe045
FEATURE [PartDesign::Body] Body095  label="1/8W_10.16_H004"
  Group = -> [Sketch140,Sketch139,AdditivePipe047]
  Origin = -> Origin086
  Tip = -> AdditivePipe047
FEATURE [PartDesign::Body] Body096  label="1/8W_Body042"
  Group = -> [Sketch147,Pad038]
  Origin = -> Origin095
  Tip = -> Pad038
FEATURE [Part::MultiFuse] Fusion037  label="R_CC25_P2.54_V"
  Placement = pos=(-1.27,1e-15,1.75) rot=(0.57735,0.57735,-0.57735;4.18879rad)
  Shapes = -> [Body096,Body094]
FEATURE [PartDesign::Body] Body097  label="1/8W_Body043"
  Group = -> [Sketch131,Pad041]
  Origin = -> Origin087
  Tip = -> Pad041
FEATURE [Part::MultiFuse] Fusion038  label="R_CC25_P10.16_H"
  Placement = pos=(0,0,1) rot=(0,0,-1;1.5708rad)
  Shapes = -> [Body097,Body095]
FEATURE [Part::MultiFuse] Fusion041  label="R_CC25_P7.62_H"
  Placement = pos=(0,0,1) rot=(0,0,-1;1.5708rad)
  Shapes = -> [Body086,Body092]
FEATURE [PartDesign::AdditivePipe] AdditivePipe049
  AuxilleryCurvelinear = true
  AuxillerySpineTangent = false
  Binormal = (0,0,0)
  Mode = 0
  Placement = pos=(0,0,0) rot=(1,0,0;1.5708rad)
  Profile = -> Sketch146
  Refine = true
  Spine = -> Sketch134
  SpineTangent = false
  Transformation = 0
  Transition = 0
FEATURE [PartDesign::Body] Body088  label="1/8W_5.08_V008"
  Group = -> [Sketch134,Sketch146,AdditivePipe049]
  Origin = -> Origin088
  Tip = -> AdditivePipe049
FEATURE [Part::MultiFuse] Fusion042  label="R_CC25_P5.08_V"
  Placement = pos=(-2.54,0,1.75) rot=(0.57735,0.57735,-0.57735;4.18879rad)
  Shapes = -> [Body087,Body088]
FEATURE [App::DocumentObjectGroup] Group007  label="1/4W_CC"
  Group = -> [Fusion037,Fusion042,Fusion041,Fusion038,Fusion039]
FEATURE [Sketcher::SketchObject] Sketch149
  AttachmentOffset = pos=(0,0,0) rot=(0,0,1;-1.5708rad)
  MapMode = 5
  Placement = pos=(0,0,0) rot=(-0.57735,-0.57735,0.57735;4.18879rad)
  Support = -> [XZ_Plane101]
  expr: Constraints[1] = 3.5 / 2
  sketch-geometry (1):
    g0: Circle CenterX=0 CenterY=0 CenterZ=0 NormalX=0 NormalY=0 NormalZ=1 AngleXU=0 Radius=1.75
  constraints (2):
    c: Coincident(g0,g-1)
    c: Radius(g0) = 1.75
FEATURE [PartDesign::Pad] Pad046
  Length = 10
  Length2 = 100
  Midplane = true
  Placement = pos=(0,0,0) rot=(1,0,0;1.5708rad)
  Profile = -> Sketch149
  Type = 0
  expr: Length = 10
FEATURE [Sketcher::SketchObject] Sketch150
  AttachmentOffset = pos=(0,0,0) rot=(0,0,1;-1.5708rad)
  MapMode = 5
  Placement = pos=(0,0,0) rot=(-0.57735,-0.57735,0.57735;4.18879rad)
  Support = -> [XZ_Plane098]
  expr: Constraints[1] = 0.55 / 2
  sketch-geometry (1):
    g0: Circle CenterX=0 CenterY=0 CenterZ=0 NormalX=0 NormalY=0 NormalZ=1 AngleXU=0 Radius=0.275
  constraints (2):
    c: Coincident(g0,g-1)
    c: Radius(g0) = 0.275
FEATURE [Sketcher::SketchObject] Sketch151
  AttachmentOffset = pos=(0,0,0) rot=(0,0,1;-1.5708rad)
  MapMode = 5
  Placement = pos=(0,0,0) rot=(-0.57735,-0.57735,0.57735;4.18879rad)
  Support = -> [XZ_Plane100]
  expr: Constraints[1] = 3.5 / 2
  sketch-geometry (1):
    g0: Circle CenterX=0 CenterY=0 CenterZ=0 NormalX=0 NormalY=0 NormalZ=1 AngleXU=0 Radius=1.75
  constraints (2):
    c: Coincident(g0,g-1)
    c: Radius(g0) = 1.75
FEATURE [PartDesign::Pad] Pad047
  Length = 10
  Length2 = 100
  Midplane = true
  Placement = pos=(0,0,0) rot=(1,0,0;1.5708rad)
  Profile = -> Sketch151
  Type = 0
  expr: Length = 10
FEATURE [Sketcher::SketchObject] Sketch152
  AttachmentOffset = pos=(0,0,0) rot=(0,0,1;-1.5708rad)
  MapMode = 5
  Placement = pos=(0,0,0) rot=(-0.57735,-0.57735,0.57735;4.18879rad)
  Support = -> [XZ_Plane103]
  expr: Constraints[1] = 0.55 / 2
  sketch-geometry (1):
    g0: Circle CenterX=0 CenterY=0 CenterZ=0 NormalX=0 NormalY=0 NormalZ=1 AngleXU=0 Radius=0.275
  constraints (2):
    c: Coincident(g0,g-1)
    c: Radius(g0) = 0.275
FEATURE [Sketcher::SketchObject] Sketch153
  MapMode = 5
  Placement = pos=(0,0,0) rot=(0.57735,0.57735,0.57735;2.0944rad)
  Support = -> [YZ_Plane105]
  expr: Constraints[11] = 3.5 / 2
  expr: Constraints[10] = 12.7
  sketch-geometry (5):
    g0: LineSegment StartX=-4.6 StartY=0 StartZ=0 EndX=4.6 EndY=0 EndZ=0
    g1: LineSegment StartX=-6.35 StartY=-1.75 StartZ=0 EndX=-6.35 EndY=-4.35 EndZ=0
    g2: LineSegment StartX=6.35 StartY=-1.75 StartZ=0 EndX=6.35 EndY=-4.35 EndZ=0
    g3: ArcOfCircle CenterX=-4.6 CenterY=-1.75 CenterZ=0 NormalX=0 NormalY=0 NormalZ=1 AngleXU=0 Radius=1.75 StartAngle=1.5708 EndAngle=3.14159
    g4: ArcOfCircle CenterX=4.6 CenterY=-1.75 CenterZ=0 NormalX=0 NormalY=0 NormalZ=1 AngleXU=0 Radius=1.75 StartAngle=-1.084e-13 EndAngle=1.5708
  constraints (13):
    c: Vertical(g1)
    c: Vertical(g2)
    c: Equal(g2,g1)
    c: Tangent(g0,g3) = 1.5708
    c: Tangent(g1,g3) = -1.5708
    c: Tangent(g0,g4) = 1.5708
    c: Tangent(g2,g4) = 1.5708
    c: Symmetric(g0,g0,g-2)
    c: Equal(g4,g3)
    c: PointOnObject(g0,g-1)
    c: DistanceX(g1,g2) = 12.7
    c: DistanceY(g1,g0) = 1.75
    c: DistanceY(g1,g1) = 2.6
FEATURE [PartDesign::AdditivePipe] AdditivePipe052
  AuxilleryCurvelinear = true
  AuxillerySpineTangent = false
  Binormal = (0,0,0)
  Mode = 0
  Placement = pos=(0,0,0) rot=(1,0,0;1.5708rad)
  Profile = -> Sketch152
  Refine = true
  Spine = -> Sketch153
  SpineTangent = false
  Transformation = 0
  Transition = 0
FEATURE [Sketcher::SketchObject] Sketch154
  MapMode = 5
  Placement = pos=(0,0,0) rot=(0.57735,0.57735,0.57735;2.0944rad)
  Support = -> [YZ_Plane102]
  expr: Constraints[11] = 3.5 / 2
  expr: Constraints[10] = 15.24
  sketch-geometry (5):
    g0: LineSegment StartX=-5.87 StartY=-5.4e-14 StartZ=0 EndX=5.87 EndY=0 EndZ=0
    g1: LineSegment StartX=-7.62 StartY=-1.75 StartZ=0 EndX=-7.62 EndY=-4.35 EndZ=0
    g2: LineSegment StartX=7.62 StartY=-1.75 StartZ=0 EndX=7.62 EndY=-4.35 EndZ=0
    g3: ArcOfCircle CenterX=-5.87 CenterY=-1.75 CenterZ=0 NormalX=0 NormalY=0 NormalZ=1 AngleXU=0 Radius=1.75 StartAngle=1.5708 EndAngle=3.14159
    g4: ArcOfCircle CenterX=5.87 CenterY=-1.75 CenterZ=0 NormalX=0 NormalY=0 NormalZ=1 AngleXU=0 Radius=1.75 StartAngle=-6.93e-14 EndAngle=1.5708
  constraints (13):
    c: Vertical(g1)
    c: Vertical(g2)
    c: Equal(g2,g1)
    c: Tangent(g0,g3) = 1.5708
    c: Tangent(g1,g3) = -1.5708
    c: Tangent(g0,g4) = 1.5708
    c: Tangent(g2,g4) = 1.5708
    c: Symmetric(g0,g0,g-2)
    c: Equal(g4,g3)
    c: PointOnObject(g0,g-1)
    c: DistanceX(g1,g2) = 15.24
    c: DistanceY(g1,g0) = 1.75
    c: DistanceY(g1,g1) = 2.6
FEATURE [Sketcher::SketchObject] Sketch155
  AttachmentOffset = pos=(0,0,0) rot=(0,0,1;-1.5708rad)
  MapMode = 5
  Placement = pos=(0,0,0) rot=(-0.57735,-0.57735,0.57735;4.18879rad)
  Support = -> [XZ_Plane104]
  expr: Constraints[1] = 0.55 / 2
  sketch-geometry (1):
    g0: Circle CenterX=0 CenterY=0 CenterZ=0 NormalX=0 NormalY=0 NormalZ=1 AngleXU=0 Radius=0.275
  constraints (2):
    c: Coincident(g0,g-1)
    c: Radius(g0) = 0.275
FEATURE [Sketcher::SketchObject] Sketch156
  AttachmentOffset = pos=(0,0,0) rot=(0,0,1;-1.5708rad)
  MapMode = 5
  Placement = pos=(0,0,0) rot=(-0.57735,-0.57735,0.57735;4.18879rad)
  Support = -> [XZ_Plane105]
  expr: Constraints[1] = 0.55 / 2
  sketch-geometry (1):
    g0: Circle CenterX=0 CenterY=0 CenterZ=0 NormalX=0 NormalY=0 NormalZ=1 AngleXU=0 Radius=0.275
  constraints (2):
    c: Coincident(g0,g-1)
    c: Radius(g0) = 0.275
FEATURE [PartDesign::AdditivePipe] AdditivePipe053
  AuxilleryCurvelinear = true
  AuxillerySpineTangent = false
  Binormal = (0,0,0)
  Mode = 0
  Placement = pos=(0,0,0) rot=(1,0,0;1.5708rad)
  Profile = -> Sketch156
  Refine = true
  Spine = -> Sketch154
  SpineTangent = false
  Transformation = 0
  Transition = 0
FEATURE [Sketcher::SketchObject] Sketch157
  AttachmentOffset = pos=(0,0,0) rot=(0,0,1;-1.5708rad)
  MapMode = 5
  Placement = pos=(0,0,0) rot=(-0.57735,-0.57735,0.57735;4.18879rad)
  Support = -> [XZ_Plane099]
  expr: Constraints[1] = 3.5 / 2
  sketch-geometry (1):
    g0: Circle CenterX=0 CenterY=0 CenterZ=0 NormalX=0 NormalY=0 NormalZ=1 AngleXU=0 Radius=1.75
  constraints (2):
    c: Coincident(g0,g-1)
    c: Radius(g0) = 1.75
FEATURE [PartDesign::Pad] Pad044
  Length = 10
  Length2 = 100
  Midplane = true
  Placement = pos=(0,0,0) rot=(1,0,0;1.5708rad)
  Profile = -> Sketch157
  Type = 0
  expr: Length = 10
FEATURE [Sketcher::SketchObject] Sketch158
  MapMode = 5
  Placement = pos=(0,0,0) rot=(0.57735,0.57735,0.57735;2.0944rad)
  Support = -> [YZ_Plane104]
  expr: Constraints[18] = 3.5 / 2
  expr: Constraints[9] = 10 / 2
  expr: Constraints[3] = 10 / 2
  sketch-geometry (8):
    g0: LineSegment StartX=7.6 StartY=0 StartZ=0 EndX=-5 EndY=0 EndZ=0
    g1: LineSegment StartX=-5 StartY=-5.08 StartZ=0 EndX=7.6 EndY=-5.08 EndZ=0
    g2: GeomPoint X=5 Y=0 Z=0
    g3: GeomPoint X=5 Y=-5.08 Z=0
    g4: GeomPoint X=-5 Y=0 Z=0
    g5: LineSegment StartX=-6.75 StartY=-1.75 StartZ=0 EndX=-6.75 EndY=-3.33 EndZ=0
    g6: ArcOfCircle CenterX=-5 CenterY=-1.75 CenterZ=0 NormalX=0 NormalY=0 NormalZ=1 AngleXU=0 Radius=1.75 StartAngle=1.5708 EndAngle=3.14159
    g7: ArcOfCircle CenterX=-5 CenterY=-3.33 CenterZ=0 NormalX=0 NormalY=0 NormalZ=1 AngleXU=0 Radius=1.75 StartAngle=3.14159 EndAngle=4.71239
  constraints (20):
    c: PointOnObject(g0,g-1)
    c: Horizontal(g1)
    c: PointOnObject(g2,g0)
    c: DistanceX(g-1,g2) = 5
    c: DistanceX(g2,g0) = 2.6
    c: PointOnObject(g3,g1)
    c: DistanceX(g3,g1) = 2.6
    c: Vertical(g0,g1)
    c: PointOnObject(g4,g0)
    c: DistanceX(g4,g-1) = 5
    c: Vertical(g5)
    c: Tangent(g0,g6) = -1.5708
    c: Tangent(g5,g6) = -1.5708
    c: Tangent(g1,g7) = -1.5708
    c: Tangent(g5,g7) = -1.5708
    c: DistanceY(g1,g0) = 5.08
    c: PointOnObject(g0,g-1)
    c: Equal(g7,g6)
    c: Radius(g6) = 1.75
    c: DistanceX(g0,g4) = 0
FEATURE [PartDesign::AdditivePipe] AdditivePipe050
  AuxilleryCurvelinear = true
  AuxillerySpineTangent = false
  Binormal = (0,0,0)
  Mode = 0
  Placement = pos=(0,0,0) rot=(1,0,0;1.5708rad)
  Profile = -> Sketch155
  Refine = true
  Spine = -> Sketch158
  SpineTangent = false
  Transformation = 0
  Transition = 0
FEATURE [Sketcher::SketchObject] Sketch159
  AttachmentOffset = pos=(0,0,0) rot=(0,0,1;-1.5708rad)
  MapMode = 5
  Placement = pos=(0,0,0) rot=(-0.57735,-0.57735,0.57735;4.18879rad)
  Support = -> [XZ_Plane102]
  expr: Constraints[1] = 3.5 / 2
  sketch-geometry (1):
    g0: Circle CenterX=0 CenterY=0 CenterZ=0 NormalX=0 NormalY=0 NormalZ=1 AngleXU=0 Radius=1.75
  constraints (2):
    c: Coincident(g0,g-1)
    c: Radius(g0) = 1.75
FEATURE [PartDesign::Pad] Pad045
  Length = 10
  Length2 = 100
  Midplane = true
  Placement = pos=(0,0,0) rot=(1,0,0;1.5708rad)
  Profile = -> Sketch159
  Type = 0
  expr: Length = 10
FEATURE [Sketcher::SketchObject] Sketch160
  MapMode = 5
  Placement = pos=(0,0,0) rot=(0.57735,0.57735,0.57735;2.0944rad)
  Support = -> [YZ_Plane099]
  expr: Constraints[18] = 2.5 / 2
  expr: Constraints[9] = 10 / 2
  expr: Constraints[3] = 10 / 2
  sketch-geometry (8):
    g0: LineSegment StartX=7.6 StartY=0 StartZ=0 EndX=-5 EndY=0 EndZ=0
    g1: LineSegment StartX=-5 StartY=-2.54 StartZ=0 EndX=7.6 EndY=-2.54 EndZ=0
    g2: GeomPoint X=5 Y=-7e-16 Z=0
    g3: GeomPoint X=5 Y=-2.54 Z=0
    g4: GeomPoint X=-5 Y=0 Z=0
    g5: LineSegment StartX=-6.25 StartY=-1.25 StartZ=0 EndX=-6.25 EndY=-1.29 EndZ=0
    g6: ArcOfCircle CenterX=-5 CenterY=-1.25 CenterZ=0 NormalX=0 NormalY=0 NormalZ=1 AngleXU=0 Radius=1.25 StartAngle=1.5708 EndAngle=3.14159
    g7: ArcOfCircle CenterX=-5 CenterY=-1.29 CenterZ=0 NormalX=0 NormalY=0 NormalZ=1 AngleXU=0 Radius=1.25 StartAngle=3.14159 EndAngle=4.71239
  constraints (20):
    c: PointOnObject(g0,g-1)
    c: Horizontal(g1)
    c: PointOnObject(g2,g0)
    c: DistanceX(g-1,g2) = 5
    c: DistanceX(g2,g0) = 2.6
    c: PointOnObject(g3,g1)
    c: DistanceX(g3,g1) = 2.6
    c: Vertical(g0,g1)
    c: PointOnObject(g4,g0)
    c: DistanceX(g4,g-1) = 5
    c: Vertical(g5)
    c: Tangent(g0,g6) = -1.5708
    c: Tangent(g5,g6) = -1.5708
    c: Tangent(g1,g7) = -1.5708
    c: Tangent(g5,g7) = -1.5708
    c: DistanceY(g1,g0) = 2.54
    c: PointOnObject(g0,g-1)
    c: Equal(g7,g6)
    c: Radius(g6) = 1.25
    c: DistanceX(g0,g4) = 0
FEATURE [PartDesign::AdditivePipe] AdditivePipe051
  AuxilleryCurvelinear = true
  AuxillerySpineTangent = false
  Binormal = (0,0,0)
  Mode = 0
  Placement = pos=(0,0,0) rot=(1,0,0;1.5708rad)
  Profile = -> Sketch150
  Refine = true
  Spine = -> Sketch160
  SpineTangent = false
  Transformation = 0
  Transition = 0
FEATURE [PartDesign::Body] Body098  label="1/8W_Body044"
  Group = -> [Sketch159,Pad045]
  Origin = -> Origin105
  Tip = -> Pad045
FEATURE [PartDesign::Body] Body099  label="1/8W_5.08_V009"
  Group = -> [Sketch158,Sketch155,AdditivePipe050]
  Origin = -> Origin099
  Tip = -> AdditivePipe050
FEATURE [PartDesign::Body] Body100  label="1/8W_12.70_H007"
  Group = -> [Sketch153,Sketch152,AdditivePipe052]
  Origin = -> Origin100
  Tip = -> AdditivePipe052
FEATURE [Part::MultiFuse] Fusion045  label="R_CC50_P12.70_H"
  Placement = pos=(0,0,1) rot=(0,0,1;1.5708rad)
  Shapes = -> [Body098,Body100]
FEATURE [PartDesign::Body] Body101  label="1/8W_Body045"
  Group = -> [Sketch149,Pad046]
  Origin = -> Origin098
  Tip = -> Pad046
FEATURE [PartDesign::Body] Body102  label="1/8W_15.24_H006"
  Group = -> [Sketch154,Sketch156,AdditivePipe053]
  Origin = -> Origin101
  Tip = -> AdditivePipe053
FEATURE [Part::MultiFuse] Fusion044  label="R_CC50_P15.24_H"
  Placement = pos=(0,0,1) rot=(0,0,-1;1.5708rad)
  Shapes = -> [Body101,Body102]
FEATURE [PartDesign::Body] Body103  label="1/8W_Body046"
  Group = -> [Sketch157,Pad044]
  Origin = -> Origin103
  Tip = -> Pad044
FEATURE [Part::MultiFuse] Fusion046  label="R_CC50_P5.08_V"
  Placement = pos=(-2.54,0,1.75) rot=(0.57735,0.57735,-0.57735;4.18879rad)
  Shapes = -> [Body103,Body099]
FEATURE [PartDesign::Body] Body104  label="1/8W_5.08_V010"
  Group = -> [Sketch160,Sketch150,AdditivePipe051]
  Origin = -> Origin104
  Tip = -> AdditivePipe051
FEATURE [PartDesign::Body] Body105  label="1/8W_Body047"
  Group = -> [Sketch151,Pad047]
  Origin = -> Origin102
  Tip = -> Pad047
FEATURE [Part::MultiFuse] Fusion043  label="R_CC50_P2.54_V"
  Placement = pos=(-2.54,0,1.75) rot=(0.57735,0.57735,-0.57735;4.18879rad)
  Shapes = -> [Body105,Body104]
FEATURE [App::DocumentObjectGroup] Group008  label="1/2W_CC"
  Group = -> [Fusion046,Fusion045,Fusion044,Fusion043]
